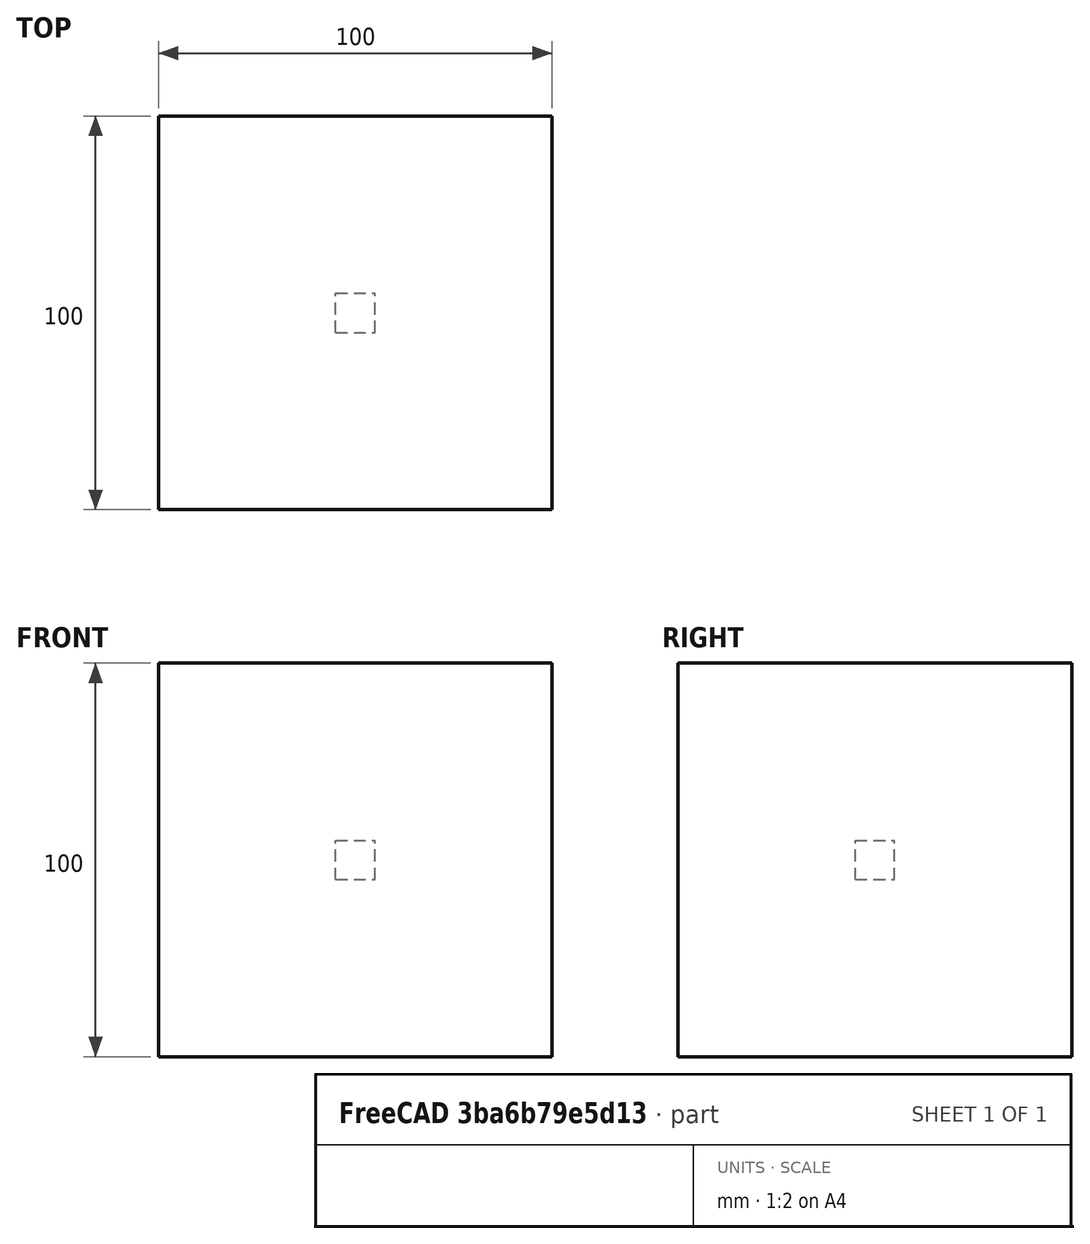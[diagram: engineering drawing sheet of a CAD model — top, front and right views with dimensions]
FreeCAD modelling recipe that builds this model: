
FCSTD DOCUMENT  (FreeCAD 0.20R29603 (Git))
Label: testCase
License: All rights reserved
LicenseURL: http://en.wikipedia.org/wiki/All_rights_reserved
objects: App::DocumentObjectGroupPython×1251, Part::FeaturePython×3, App::Part×2
note: 2 computed .brp shape members not serialized (recipe doc carries the construction recipe); baked Part::Feature solids carry a one-line shape summary decoded from their .brp

FEATURE [App::DocumentObjectGroupPython] HALFPI  # scripted group (container) (typed FeaturePython)
  name = HALFPI
  value = pi/2.
FEATURE [App::DocumentObjectGroupPython] PI  # scripted group (container) (typed FeaturePython)
  name = PI
  value = 1.*pi
FEATURE [App::DocumentObjectGroupPython] TWOPI  # scripted group (container) (typed FeaturePython)
  name = TWOPI
  value = 2.*pi
FEATURE [App::DocumentObjectGroupPython] Constants  # scripted group (container) (typed FeaturePython)
  Group = -> [HALFPI,PI,TWOPI]
FEATURE [App::DocumentObjectGroupPython] Variables  # scripted group (container) (typed FeaturePython)
FEATURE [App::DocumentObjectGroupPython] Quantities  # scripted group (container) (typed FeaturePython)
FEATURE [App::DocumentObjectGroupPython] Isotopes  # scripted group (container) (typed FeaturePython)
FEATURE [App::DocumentObjectGroupPython] Elements  # scripted group (container) (typed FeaturePython)
FEATURE [App::DocumentObjectGroupPython] Matrix  # scripted group (container) (typed FeaturePython)
FEATURE [App::DocumentObjectGroupPython] Surfaces  # scripted group (container) (typed FeaturePython)
FEATURE [App::DocumentObjectGroupPython] Opticals  # scripted group (container) (typed FeaturePython)
  Group = -> [Matrix,Surfaces]
FEATURE [App::DocumentObjectGroupPython] G4Isotopes  # scripted group (container) (typed FeaturePython)
FEATURE [App::DocumentObjectGroupPython] H_element  # scripted group (container) (typed FeaturePython)
  Z = 1
  atom_value = 1.008
  formula = H
  name = H_element
FEATURE [App::DocumentObjectGroupPython] He_element  # scripted group (container) (typed FeaturePython)
  Z = 2
  atom_value = 4.0026
  formula = He
  name = He_element
FEATURE [App::DocumentObjectGroupPython] Li_element  # scripted group (container) (typed FeaturePython)
  Z = 3
  atom_value = 6.94
  formula = Li
  name = Li_element
FEATURE [App::DocumentObjectGroupPython] Be_element  # scripted group (container) (typed FeaturePython)
  Z = 4
  atom_value = 9.01218
  formula = Be
  name = Be_element
FEATURE [App::DocumentObjectGroupPython] B_element  # scripted group (container) (typed FeaturePython)
  Z = 5
  atom_value = 10.81
  formula = B
  name = B_element
FEATURE [App::DocumentObjectGroupPython] C_element  # scripted group (container) (typed FeaturePython)
  Z = 6
  atom_value = 12.011
  formula = C
  name = C_element
FEATURE [App::DocumentObjectGroupPython] N_element  # scripted group (container) (typed FeaturePython)
  Z = 7
  atom_value = 14.007
  formula = N
  name = N_element
FEATURE [App::DocumentObjectGroupPython] O_element  # scripted group (container) (typed FeaturePython)
  Z = 8
  atom_value = 15.999
  formula = O
  name = O_element
FEATURE [App::DocumentObjectGroupPython] F_element  # scripted group (container) (typed FeaturePython)
  Z = 9
  atom_value = 18.9984
  formula = F
  name = F_element
FEATURE [App::DocumentObjectGroupPython] Ne_element  # scripted group (container) (typed FeaturePython)
  Z = 10
  atom_value = 20.1797
  formula = Ne
  name = Ne_element
FEATURE [App::DocumentObjectGroupPython] Na_element  # scripted group (container) (typed FeaturePython)
  Z = 11
  atom_value = 22.9898
  formula = Na
  name = Na_element
FEATURE [App::DocumentObjectGroupPython] Mg_element  # scripted group (container) (typed FeaturePython)
  Z = 12
  atom_value = 24.305
  formula = Mg
  name = Mg_element
FEATURE [App::DocumentObjectGroupPython] Al_element  # scripted group (container) (typed FeaturePython)
  Z = 13
  atom_value = 26.9815
  formula = Al
  name = Al_element
FEATURE [App::DocumentObjectGroupPython] Si_element  # scripted group (container) (typed FeaturePython)
  Z = 14
  atom_value = 28.085
  formula = Si
  name = Si_element
FEATURE [App::DocumentObjectGroupPython] P_element  # scripted group (container) (typed FeaturePython)
  Z = 15
  atom_value = 30.9738
  formula = P
  name = P_element
FEATURE [App::DocumentObjectGroupPython] S_element  # scripted group (container) (typed FeaturePython)
  Z = 16
  atom_value = 32.06
  formula = S
  name = S_element
FEATURE [App::DocumentObjectGroupPython] Cl_element  # scripted group (container) (typed FeaturePython)
  Z = 17
  atom_value = 35.45
  formula = Cl
  name = Cl_element
FEATURE [App::DocumentObjectGroupPython] Ar_element  # scripted group (container) (typed FeaturePython)
  Z = 18
  atom_value = 39.95
  formula = Ar
  name = Ar_element
FEATURE [App::DocumentObjectGroupPython] K_element  # scripted group (container) (typed FeaturePython)
  Z = 19
  atom_value = 39.0983
  formula = K
  name = K_element
FEATURE [App::DocumentObjectGroupPython] Ca_element  # scripted group (container) (typed FeaturePython)
  Z = 20
  atom_value = 40.078
  formula = Ca
  name = Ca_element
FEATURE [App::DocumentObjectGroupPython] Sc_element  # scripted group (container) (typed FeaturePython)
  Z = 21
  atom_value = 44.9559
  formula = Sc
  name = Sc_element
FEATURE [App::DocumentObjectGroupPython] Ti_element  # scripted group (container) (typed FeaturePython)
  Z = 22
  atom_value = 47.867
  formula = Ti
  name = Ti_element
FEATURE [App::DocumentObjectGroupPython] V_element  # scripted group (container) (typed FeaturePython)
  Z = 23
  atom_value = 50.9415
  formula = V
  name = V_element
FEATURE [App::DocumentObjectGroupPython] Cr_element  # scripted group (container) (typed FeaturePython)
  Z = 24
  atom_value = 51.9961
  formula = Cr
  name = Cr_element
FEATURE [App::DocumentObjectGroupPython] Mn_element  # scripted group (container) (typed FeaturePython)
  Z = 25
  atom_value = 54.938
  formula = Mn
  name = Mn_element
FEATURE [App::DocumentObjectGroupPython] Fe_element  # scripted group (container) (typed FeaturePython)
  Z = 26
  atom_value = 55.845
  formula = Fe
  name = Fe_element
FEATURE [App::DocumentObjectGroupPython] Co_element  # scripted group (container) (typed FeaturePython)
  Z = 27
  atom_value = 58.9332
  formula = Co
  name = Co_element
FEATURE [App::DocumentObjectGroupPython] Ni_element  # scripted group (container) (typed FeaturePython)
  Z = 28
  atom_value = 58.6934
  formula = Ni
  name = Ni_element
FEATURE [App::DocumentObjectGroupPython] Cu_element  # scripted group (container) (typed FeaturePython)
  Z = 29
  atom_value = 63.546
  formula = Cu
  name = Cu_element
FEATURE [App::DocumentObjectGroupPython] Zn_element  # scripted group (container) (typed FeaturePython)
  Z = 30
  atom_value = 65.38
  formula = Zn
  name = Zn_element
FEATURE [App::DocumentObjectGroupPython] Ga_element  # scripted group (container) (typed FeaturePython)
  Z = 31
  atom_value = 69.723
  formula = Ga
  name = Ga_element
FEATURE [App::DocumentObjectGroupPython] Ge_element  # scripted group (container) (typed FeaturePython)
  Z = 32
  atom_value = 72.63
  formula = Ge
  name = Ge_element
FEATURE [App::DocumentObjectGroupPython] As_element  # scripted group (container) (typed FeaturePython)
  Z = 33
  atom_value = 74.9216
  formula = As
  name = As_element
FEATURE [App::DocumentObjectGroupPython] Se_element  # scripted group (container) (typed FeaturePython)
  Z = 34
  atom_value = 78.971
  formula = Se
  name = Se_element
FEATURE [App::DocumentObjectGroupPython] Br_element  # scripted group (container) (typed FeaturePython)
  Z = 35
  atom_value = 79.904
  formula = Br
  name = Br_element
FEATURE [App::DocumentObjectGroupPython] Kr_element  # scripted group (container) (typed FeaturePython)
  Z = 36
  atom_value = 83.798
  formula = Kr
  name = Kr_element
FEATURE [App::DocumentObjectGroupPython] Rb_element  # scripted group (container) (typed FeaturePython)
  Z = 37
  atom_value = 85.4678
  formula = Rb
  name = Rb_element
FEATURE [App::DocumentObjectGroupPython] Sr_element  # scripted group (container) (typed FeaturePython)
  Z = 38
  atom_value = 87.62
  formula = Sr
  name = Sr_element
FEATURE [App::DocumentObjectGroupPython] Y_element  # scripted group (container) (typed FeaturePython)
  Z = 39
  atom_value = 88.9058
  formula = Y
  name = Y_element
FEATURE [App::DocumentObjectGroupPython] Zr_element  # scripted group (container) (typed FeaturePython)
  Z = 40
  atom_value = 91.224
  formula = Zr
  name = Zr_element
FEATURE [App::DocumentObjectGroupPython] Nb_element  # scripted group (container) (typed FeaturePython)
  Z = 41
  atom_value = 92.9064
  formula = Nb
  name = Nb_element
FEATURE [App::DocumentObjectGroupPython] Mo_element  # scripted group (container) (typed FeaturePython)
  Z = 42
  atom_value = 95.95
  formula = Mo
  name = Mo_element
FEATURE [App::DocumentObjectGroupPython] Tc_element  # scripted group (container) (typed FeaturePython)
  Z = 43
  atom_value = 97
  formula = Tc
  name = Tc_element
FEATURE [App::DocumentObjectGroupPython] Ru_element  # scripted group (container) (typed FeaturePython)
  Z = 44
  atom_value = 101.07
  formula = Ru
  name = Ru_element
FEATURE [App::DocumentObjectGroupPython] Rh_element  # scripted group (container) (typed FeaturePython)
  Z = 45
  atom_value = 102.905
  formula = Rh
  name = Rh_element
FEATURE [App::DocumentObjectGroupPython] Pd_element  # scripted group (container) (typed FeaturePython)
  Z = 46
  atom_value = 106.42
  formula = Pd
  name = Pd_element
FEATURE [App::DocumentObjectGroupPython] Ag_element  # scripted group (container) (typed FeaturePython)
  Z = 47
  atom_value = 107.868
  formula = Ag
  name = Ag_element
FEATURE [App::DocumentObjectGroupPython] Cd_element  # scripted group (container) (typed FeaturePython)
  Z = 48
  atom_value = 112.414
  formula = Cd
  name = Cd_element
FEATURE [App::DocumentObjectGroupPython] In_element  # scripted group (container) (typed FeaturePython)
  Z = 49
  atom_value = 114.818
  formula = In
  name = In_element
FEATURE [App::DocumentObjectGroupPython] Sn_element  # scripted group (container) (typed FeaturePython)
  Z = 50
  atom_value = 118.71
  formula = Sn
  name = Sn_element
FEATURE [App::DocumentObjectGroupPython] Sb_element  # scripted group (container) (typed FeaturePython)
  Z = 51
  atom_value = 121.76
  formula = Sb
  name = Sb_element
FEATURE [App::DocumentObjectGroupPython] Te_element  # scripted group (container) (typed FeaturePython)
  Z = 52
  atom_value = 127.6
  formula = Te
  name = Te_element
FEATURE [App::DocumentObjectGroupPython] I_element  # scripted group (container) (typed FeaturePython)
  Z = 53
  atom_value = 126.904
  formula = I
  name = I_element
FEATURE [App::DocumentObjectGroupPython] Xe_element  # scripted group (container) (typed FeaturePython)
  Z = 54
  atom_value = 131.293
  formula = Xe
  name = Xe_element
FEATURE [App::DocumentObjectGroupPython] Cs_element  # scripted group (container) (typed FeaturePython)
  Z = 55
  atom_value = 132.905
  formula = Cs
  name = Cs_element
FEATURE [App::DocumentObjectGroupPython] Ba_element  # scripted group (container) (typed FeaturePython)
  Z = 56
  atom_value = 137.327
  formula = Ba
  name = Ba_element
FEATURE [App::DocumentObjectGroupPython] La_element  # scripted group (container) (typed FeaturePython)
  Z = 57
  atom_value = 138.905
  formula = La
  name = La_element
FEATURE [App::DocumentObjectGroupPython] Ce_element  # scripted group (container) (typed FeaturePython)
  Z = 58
  atom_value = 140.116
  formula = Ce
  name = Ce_element
FEATURE [App::DocumentObjectGroupPython] Pr_element  # scripted group (container) (typed FeaturePython)
  Z = 59
  atom_value = 140.908
  formula = Pr
  name = Pr_element
FEATURE [App::DocumentObjectGroupPython] Nd_element  # scripted group (container) (typed FeaturePython)
  Z = 60
  atom_value = 144.242
  formula = Nd
  name = Nd_element
FEATURE [App::DocumentObjectGroupPython] Pm_element  # scripted group (container) (typed FeaturePython)
  Z = 61
  atom_value = 145
  formula = Pm
  name = Pm_element
FEATURE [App::DocumentObjectGroupPython] Sm_element  # scripted group (container) (typed FeaturePython)
  Z = 62
  atom_value = 150.36
  formula = Sm
  name = Sm_element
FEATURE [App::DocumentObjectGroupPython] Eu_element  # scripted group (container) (typed FeaturePython)
  Z = 63
  atom_value = 151.964
  formula = Eu
  name = Eu_element
FEATURE [App::DocumentObjectGroupPython] Gd_element  # scripted group (container) (typed FeaturePython)
  Z = 64
  atom_value = 157.25
  formula = Gd
  name = Gd_element
FEATURE [App::DocumentObjectGroupPython] Tb_element  # scripted group (container) (typed FeaturePython)
  Z = 65
  atom_value = 158.925
  formula = Tb
  name = Tb_element
FEATURE [App::DocumentObjectGroupPython] Dy_element  # scripted group (container) (typed FeaturePython)
  Z = 66
  atom_value = 162.5
  formula = Dy
  name = Dy_element
FEATURE [App::DocumentObjectGroupPython] Ho_element  # scripted group (container) (typed FeaturePython)
  Z = 67
  atom_value = 164.93
  formula = Ho
  name = Ho_element
FEATURE [App::DocumentObjectGroupPython] Er_element  # scripted group (container) (typed FeaturePython)
  Z = 68
  atom_value = 167.259
  formula = Er
  name = Er_element
FEATURE [App::DocumentObjectGroupPython] Tm_element  # scripted group (container) (typed FeaturePython)
  Z = 69
  atom_value = 168.934
  formula = Tm
  name = Tm_element
FEATURE [App::DocumentObjectGroupPython] Yb_element  # scripted group (container) (typed FeaturePython)
  Z = 70
  atom_value = 173.045
  formula = Yb
  name = Yb_element
FEATURE [App::DocumentObjectGroupPython] Lu_element  # scripted group (container) (typed FeaturePython)
  Z = 71
  atom_value = 174.967
  formula = Lu
  name = Lu_element
FEATURE [App::DocumentObjectGroupPython] Hf_element  # scripted group (container) (typed FeaturePython)
  Z = 72
  atom_value = 178.49
  formula = Hf
  name = Hf_element
FEATURE [App::DocumentObjectGroupPython] Ta_element  # scripted group (container) (typed FeaturePython)
  Z = 73
  atom_value = 180.948
  formula = Ta
  name = Ta_element
FEATURE [App::DocumentObjectGroupPython] W_element  # scripted group (container) (typed FeaturePython)
  Z = 74
  atom_value = 183.84
  formula = W
  name = W_element
FEATURE [App::DocumentObjectGroupPython] Re_element  # scripted group (container) (typed FeaturePython)
  Z = 75
  atom_value = 186.207
  formula = Re
  name = Re_element
FEATURE [App::DocumentObjectGroupPython] Os_element  # scripted group (container) (typed FeaturePython)
  Z = 76
  atom_value = 190.23
  formula = Os
  name = Os_element
FEATURE [App::DocumentObjectGroupPython] Ir_element  # scripted group (container) (typed FeaturePython)
  Z = 77
  atom_value = 192.217
  formula = Ir
  name = Ir_element
FEATURE [App::DocumentObjectGroupPython] Pt_element  # scripted group (container) (typed FeaturePython)
  Z = 78
  atom_value = 195.084
  formula = Pt
  name = Pt_element
FEATURE [App::DocumentObjectGroupPython] Au_element  # scripted group (container) (typed FeaturePython)
  Z = 79
  atom_value = 196.967
  formula = Au
  name = Au_element
FEATURE [App::DocumentObjectGroupPython] Hg_element  # scripted group (container) (typed FeaturePython)
  Z = 80
  atom_value = 200.592
  formula = Hg
  name = Hg_element
FEATURE [App::DocumentObjectGroupPython] Tl_element  # scripted group (container) (typed FeaturePython)
  Z = 81
  atom_value = 204.38
  formula = Tl
  name = Tl_element
FEATURE [App::DocumentObjectGroupPython] Pb_element  # scripted group (container) (typed FeaturePython)
  Z = 82
  atom_value = 207.2
  formula = Pb
  name = Pb_element
FEATURE [App::DocumentObjectGroupPython] Bi_element  # scripted group (container) (typed FeaturePython)
  Z = 83
  atom_value = 208.98
  formula = Bi
  name = Bi_element
FEATURE [App::DocumentObjectGroupPython] Po_element  # scripted group (container) (typed FeaturePython)
  Z = 84
  atom_value = 209
  formula = Po
  name = Po_element
FEATURE [App::DocumentObjectGroupPython] At_element  # scripted group (container) (typed FeaturePython)
  Z = 85
  atom_value = 210
  formula = At
  name = At_element
FEATURE [App::DocumentObjectGroupPython] Rn_element  # scripted group (container) (typed FeaturePython)
  Z = 86
  atom_value = 222
  formula = Rn
  name = Rn_element
FEATURE [App::DocumentObjectGroupPython] Fr_element  # scripted group (container) (typed FeaturePython)
  Z = 87
  atom_value = 223
  formula = Fr
  name = Fr_element
FEATURE [App::DocumentObjectGroupPython] Ra_element  # scripted group (container) (typed FeaturePython)
  Z = 88
  atom_value = 226
  formula = Ra
  name = Ra_element
FEATURE [App::DocumentObjectGroupPython] Ac_element  # scripted group (container) (typed FeaturePython)
  Z = 89
  atom_value = 227
  formula = Ac
  name = Ac_element
FEATURE [App::DocumentObjectGroupPython] Th_element  # scripted group (container) (typed FeaturePython)
  Z = 90
  atom_value = 232.038
  formula = Th
  name = Th_element
FEATURE [App::DocumentObjectGroupPython] Pa_element  # scripted group (container) (typed FeaturePython)
  Z = 91
  atom_value = 231.036
  formula = Pa
  name = Pa_element
FEATURE [App::DocumentObjectGroupPython] U_element  # scripted group (container) (typed FeaturePython)
  Z = 92
  atom_value = 238.029
  formula = U
  name = U_element
FEATURE [App::DocumentObjectGroupPython] Np_element  # scripted group (container) (typed FeaturePython)
  Z = 93
  atom_value = 237
  formula = Np
  name = Np_element
FEATURE [App::DocumentObjectGroupPython] Pu_element  # scripted group (container) (typed FeaturePython)
  Z = 94
  atom_value = 244
  formula = Pu
  name = Pu_element
FEATURE [App::DocumentObjectGroupPython] Am_element  # scripted group (container) (typed FeaturePython)
  Z = 95
  atom_value = 243
  formula = Am
  name = Am_element
FEATURE [App::DocumentObjectGroupPython] Cm_element  # scripted group (container) (typed FeaturePython)
  Z = 96
  atom_value = 247
  formula = Cm
  name = Cm_element
FEATURE [App::DocumentObjectGroupPython] Bk_element  # scripted group (container) (typed FeaturePython)
  Z = 97
  atom_value = 247
  formula = Bk
  name = Bk_element
FEATURE [App::DocumentObjectGroupPython] Cf_element  # scripted group (container) (typed FeaturePython)
  Z = 98
  atom_value = 251
  formula = Cf
  name = Cf_element
FEATURE [App::DocumentObjectGroupPython] G4Elements  # scripted group (container) (typed FeaturePython)
  Group = -> [H_element,He_element,Li_element,Be_element,B_element,C_element,N_element,O_element,F_element,Ne_element,Na_element,Mg_element,Al_element,Si_element,P_element,S_element,Cl_element,Ar_element,K_element,Ca_element,Sc_element,Ti_element,V_element,Cr_element,Mn_element,Fe_element,Co_element,Ni_element,Cu_element,Zn_element,Ga_element,Ge_element,As_element,Se_element,Br_element,Kr_element,Rb_element,+61 more]
FEATURE [App::DocumentObjectGroupPython] H_element001  label="H_element : 0.101"  # scripted group (container) (typed FeaturePython)
  n = 0.101327
FEATURE [App::DocumentObjectGroupPython] C_element001  label="C_element : 0.775"  # scripted group (container) (typed FeaturePython)
  n = 0.7755
FEATURE [App::DocumentObjectGroupPython] N_element001  label="N_element : 0.035"  # scripted group (container) (typed FeaturePython)
  n = 0.035057
FEATURE [App::DocumentObjectGroupPython] O_element001  label="O_element : 0.052"  # scripted group (container) (typed FeaturePython)
  n = 0.0523159
FEATURE [App::DocumentObjectGroupPython] F_element001  label="F_element : 0.017"  # scripted group (container) (typed FeaturePython)
  n = 0.017422
FEATURE [App::DocumentObjectGroupPython] Ca_element001  label="Ca_element : 0.018"  # scripted group (container) (typed FeaturePython)
  n = 0.018378
FEATURE [App::DocumentObjectGroupPython] G4_A_150_TISSUE  label="G4_A-150_TISSUE"  # scripted group (container) (typed FeaturePython)
  Dunit = g/cm3
  Dvalue = 1.127
  Group = -> [H_element001,C_element001,N_element001,O_element001,F_element001,Ca_element001]
  conduct = 2
  density = 1
  expand = 3
  formula = G4_A-150_TISSUE
  name = G4_A-150_TISSUE
  specific = 4
FEATURE [App::DocumentObjectGroupPython] C_element002  label="C_element : 3"  # scripted group (container) (typed FeaturePython)
  n = 3
  ref = C_element
FEATURE [App::DocumentObjectGroupPython] H_element002  label="H_element : 6"  # scripted group (container) (typed FeaturePython)
  n = 6
  ref = H_element
FEATURE [App::DocumentObjectGroupPython] O_element002  label="O_element : 1"  # scripted group (container) (typed FeaturePython)
  n = 1
  ref = O_element
FEATURE [App::DocumentObjectGroupPython] G4_ACETONE  # scripted group (container) (typed FeaturePython)
  Dunit = g/cm3
  Dvalue = 0.7899
  Group = -> [C_element002,H_element002,O_element002]
  conduct = 2
  density = 1
  expand = 3
  formula = G4_ACETONE
  name = G4_ACETONE
  specific = 4
FEATURE [App::DocumentObjectGroupPython] C_element003  label="C_element : 2"  # scripted group (container) (typed FeaturePython)
  n = 2
  ref = C_element
FEATURE [App::DocumentObjectGroupPython] H_element003  label="H_element : 2"  # scripted group (container) (typed FeaturePython)
  n = 2
  ref = H_element
FEATURE [App::DocumentObjectGroupPython] G4_ACETYLENE  # scripted group (container) (typed FeaturePython)
  Dunit = g/cm3
  Dvalue = 0.0010967
  Group = -> [C_element003,H_element003]
  conduct = 2
  density = 1
  expand = 3
  formula = G4_ACETYLENE
  name = G4_ACETYLENE
  specific = 4
FEATURE [App::DocumentObjectGroupPython] C_element004  label="C_element : 5"  # scripted group (container) (typed FeaturePython)
  n = 5
  ref = C_element
FEATURE [App::DocumentObjectGroupPython] H_element004  label="H_element : 5"  # scripted group (container) (typed FeaturePython)
  n = 5
  ref = H_element
FEATURE [App::DocumentObjectGroupPython] N_element002  label="N_element : 5"  # scripted group (container) (typed FeaturePython)
  n = 5
  ref = N_element
FEATURE [App::DocumentObjectGroupPython] G4_ADENINE  # scripted group (container) (typed FeaturePython)
  Dunit = g/cm3
  Dvalue = 1.6
  Group = -> [C_element004,H_element004,N_element002]
  conduct = 2
  density = 1
  expand = 3
  formula = G4_ADENINE
  name = G4_ADENINE
  specific = 4
FEATURE [App::DocumentObjectGroupPython] H_element005  label="H_element : 0.114"  # scripted group (container) (typed FeaturePython)
  n = 0.114
FEATURE [App::DocumentObjectGroupPython] C_element005  label="C_element : 0.598"  # scripted group (container) (typed FeaturePython)
  n = 0.598
FEATURE [App::DocumentObjectGroupPython] N_element003  label="N_element : 0.007"  # scripted group (container) (typed FeaturePython)
  n = 0.007
FEATURE [App::DocumentObjectGroupPython] O_element003  label="O_element : 0.278"  # scripted group (container) (typed FeaturePython)
  n = 0.278
FEATURE [App::DocumentObjectGroupPython] Na_element001  label="Na_element : 0.001"  # scripted group (container) (typed FeaturePython)
  n = 0.001
FEATURE [App::DocumentObjectGroupPython] S_element001  label="S_element : 0.001"  # scripted group (container) (typed FeaturePython)
  n = 0.001
FEATURE [App::DocumentObjectGroupPython] Cl_element001  label="Cl_element : 0.001"  # scripted group (container) (typed FeaturePython)
  n = 0.001
FEATURE [App::DocumentObjectGroupPython] G4_ADIPOSE_TISSUE_ICRP  # scripted group (container) (typed FeaturePython)
  Dunit = g/cm3
  Dvalue = 0.95
  Group = -> [H_element005,C_element005,N_element003,O_element003,Na_element001,S_element001,Cl_element001]
  conduct = 2
  density = 1
  expand = 3
  formula = G4_ADIPOSE_TISSUE_ICRP
  name = G4_ADIPOSE_TISSUE_ICRP
  specific = 4
FEATURE [App::DocumentObjectGroupPython] C_element006  label="C_element : 0.000"  # scripted group (container) (typed FeaturePython)
  n = 0.000124
FEATURE [App::DocumentObjectGroupPython] N_element004  label="N_element : 0.755"  # scripted group (container) (typed FeaturePython)
  n = 0.755268
FEATURE [App::DocumentObjectGroupPython] O_element004  label="O_element : 0.232"  # scripted group (container) (typed FeaturePython)
  n = 0.231781
FEATURE [App::DocumentObjectGroupPython] Ar_element001  label="Ar_element : 0.013"  # scripted group (container) (typed FeaturePython)
  n = 0.012827
FEATURE [App::DocumentObjectGroupPython] G4_AIR  # scripted group (container) (typed FeaturePython)
  Dunit = g/cm3
  Dvalue = 0.00120479
  Group = -> [C_element006,N_element004,O_element004,Ar_element001]
  conduct = 2
  density = 1
  expand = 3
  formula = G4_AIR
  name = G4_AIR
  specific = 4
FEATURE [App::DocumentObjectGroupPython] C_element007  label="C_element : 006"  # scripted group (container) (typed FeaturePython)
  n = 3
  ref = C_element
FEATURE [App::DocumentObjectGroupPython] H_element006  label="H_element : 7"  # scripted group (container) (typed FeaturePython)
  n = 7
  ref = H_element
FEATURE [App::DocumentObjectGroupPython] N_element005  label="N_element : 1"  # scripted group (container) (typed FeaturePython)
  n = 1
  ref = N_element
FEATURE [App::DocumentObjectGroupPython] O_element005  label="O_element : 2"  # scripted group (container) (typed FeaturePython)
  n = 2
  ref = O_element
FEATURE [App::DocumentObjectGroupPython] G4_ALANINE  # scripted group (container) (typed FeaturePython)
  Dunit = g/cm3
  Dvalue = 1.42
  Group = -> [C_element007,H_element006,N_element005,O_element005]
  conduct = 2
  density = 1
  expand = 3
  formula = G4_ALANINE
  name = G4_ALANINE
  specific = 4
FEATURE [App::DocumentObjectGroupPython] Al_element001  label="Al_element : 2"  # scripted group (container) (typed FeaturePython)
  n = 2
  ref = Al_element
FEATURE [App::DocumentObjectGroupPython] O_element006  label="O_element : 3"  # scripted group (container) (typed FeaturePython)
  n = 3
  ref = O_element
FEATURE [App::DocumentObjectGroupPython] G4_ALUMINUM_OXIDE  # scripted group (container) (typed FeaturePython)
  Dunit = g/cm3
  Dvalue = 3.97
  Group = -> [Al_element001,O_element006]
  conduct = 2
  density = 1
  expand = 3
  formula = G4_ALUMINUM_OXIDE
  name = G4_ALUMINUM_OXIDE
  specific = 4
FEATURE [App::DocumentObjectGroupPython] H_element007  label="H_element : 0.106"  # scripted group (container) (typed FeaturePython)
  n = 0.10593
FEATURE [App::DocumentObjectGroupPython] C_element008  label="C_element : 0.789"  # scripted group (container) (typed FeaturePython)
  n = 0.788974
FEATURE [App::DocumentObjectGroupPython] O_element007  label="O_element : 0.105"  # scripted group (container) (typed FeaturePython)
  n = 0.105096
FEATURE [App::DocumentObjectGroupPython] G4_AMBER  # scripted group (container) (typed FeaturePython)
  Dunit = g/cm3
  Dvalue = 1.1
  Group = -> [H_element007,C_element008,O_element007]
  conduct = 2
  density = 1
  expand = 3
  formula = G4_AMBER
  name = G4_AMBER
  specific = 4
FEATURE [App::DocumentObjectGroupPython] N_element006  label="N_element : 006"  # scripted group (container) (typed FeaturePython)
  n = 1
  ref = N_element
FEATURE [App::DocumentObjectGroupPython] H_element008  label="H_element : 3"  # scripted group (container) (typed FeaturePython)
  n = 3
  ref = H_element
FEATURE [App::DocumentObjectGroupPython] G4_AMMONIA  # scripted group (container) (typed FeaturePython)
  Dunit = g/cm3
  Dvalue = 0.000826019
  Group = -> [N_element006,H_element008]
  conduct = 2
  density = 1
  expand = 3
  formula = G4_AMMONIA
  name = G4_AMMONIA
  specific = 4
FEATURE [App::DocumentObjectGroupPython] C_element009  label="C_element : 6"  # scripted group (container) (typed FeaturePython)
  n = 6
  ref = C_element
FEATURE [App::DocumentObjectGroupPython] H_element009  label="H_element : 008"  # scripted group (container) (typed FeaturePython)
  n = 7
  ref = H_element
FEATURE [App::DocumentObjectGroupPython] N_element007  label="N_element : 007"  # scripted group (container) (typed FeaturePython)
  n = 1
  ref = N_element
FEATURE [App::DocumentObjectGroupPython] G4_ANILINE  # scripted group (container) (typed FeaturePython)
  Dunit = g/cm3
  Dvalue = 1.0235
  Group = -> [C_element009,H_element009,N_element007]
  conduct = 2
  density = 1
  expand = 3
  formula = G4_ANILINE
  name = G4_ANILINE
  specific = 4
FEATURE [App::DocumentObjectGroupPython] C_element010  label="C_element : 14"  # scripted group (container) (typed FeaturePython)
  n = 14
  ref = C_element
FEATURE [App::DocumentObjectGroupPython] H_element010  label="H_element : 10"  # scripted group (container) (typed FeaturePython)
  n = 10
  ref = H_element
FEATURE [App::DocumentObjectGroupPython] G4_ANTHRACENE  # scripted group (container) (typed FeaturePython)
  Dunit = g/cm3
  Dvalue = 1.283
  Group = -> [C_element010,H_element010]
  conduct = 2
  density = 1
  expand = 3
  formula = G4_ANTHRACENE
  name = G4_ANTHRACENE
  specific = 4
FEATURE [App::DocumentObjectGroupPython] H_element011  label="H_element : 0.065"  # scripted group (container) (typed FeaturePython)
  n = 0.0654709
FEATURE [App::DocumentObjectGroupPython] C_element011  label="C_element : 0.537"  # scripted group (container) (typed FeaturePython)
  n = 0.536944
FEATURE [App::DocumentObjectGroupPython] N_element008  label="N_element : 0.021"  # scripted group (container) (typed FeaturePython)
  n = 0.0215
FEATURE [App::DocumentObjectGroupPython] O_element008  label="O_element : 0.032"  # scripted group (container) (typed FeaturePython)
  n = 0.032085
FEATURE [App::DocumentObjectGroupPython] F_element002  label="F_element : 0.167"  # scripted group (container) (typed FeaturePython)
  n = 0.167411
FEATURE [App::DocumentObjectGroupPython] Ca_element002  label="Ca_element : 0.177"  # scripted group (container) (typed FeaturePython)
  n = 0.176589
FEATURE [App::DocumentObjectGroupPython] G4_B_100_BONE  label="G4_B-100_BONE"  # scripted group (container) (typed FeaturePython)
  Dunit = g/cm3
  Dvalue = 1.45
  Group = -> [H_element011,C_element011,N_element008,O_element008,F_element002,Ca_element002]
  conduct = 2
  density = 1
  expand = 3
  formula = G4_B-100_BONE
  name = G4_B-100_BONE
  specific = 4
FEATURE [App::DocumentObjectGroupPython] H_element012  label="H_element : 0.057"  # scripted group (container) (typed FeaturePython)
  n = 0.057441
FEATURE [App::DocumentObjectGroupPython] C_element012  label="C_element : 0.790"  # scripted group (container) (typed FeaturePython)
  n = 0.774591
FEATURE [App::DocumentObjectGroupPython] O_element009  label="O_element : 0.168"  # scripted group (container) (typed FeaturePython)
  n = 0.167968
FEATURE [App::DocumentObjectGroupPython] G4_BAKELITE  # scripted group (container) (typed FeaturePython)
  Dunit = g/cm3
  Dvalue = 1.25
  Group = -> [H_element012,C_element012,O_element009]
  conduct = 2
  density = 1
  expand = 3
  formula = G4_BAKELITE
  name = G4_BAKELITE
  specific = 4
FEATURE [App::DocumentObjectGroupPython] Ba_element001  label="Ba_element : 1"  # scripted group (container) (typed FeaturePython)
  n = 1
  ref = Ba_element
FEATURE [App::DocumentObjectGroupPython] F_element003  label="F_element : 2"  # scripted group (container) (typed FeaturePython)
  n = 2
  ref = F_element
FEATURE [App::DocumentObjectGroupPython] G4_BARIUM_FLUORIDE  # scripted group (container) (typed FeaturePython)
  Dunit = g/cm3
  Dvalue = 4.89
  Group = -> [Ba_element001,F_element003]
  conduct = 2
  density = 1
  expand = 3
  formula = G4_BARIUM_FLUORIDE
  name = G4_BARIUM_FLUORIDE
  specific = 4
FEATURE [App::DocumentObjectGroupPython] Ba_element002  label="Ba_element : 002"  # scripted group (container) (typed FeaturePython)
  n = 1
  ref = Ba_element
FEATURE [App::DocumentObjectGroupPython] S_element002  label="S_element : 1"  # scripted group (container) (typed FeaturePython)
  n = 1
  ref = S_element
FEATURE [App::DocumentObjectGroupPython] O_element010  label="O_element : 4"  # scripted group (container) (typed FeaturePython)
  n = 4
  ref = O_element
FEATURE [App::DocumentObjectGroupPython] G4_BARIUM_SULFATE  # scripted group (container) (typed FeaturePython)
  Dunit = g/cm3
  Dvalue = 4.5
  Group = -> [Ba_element002,S_element002,O_element010]
  conduct = 2
  density = 1
  expand = 3
  formula = G4_BARIUM_SULFATE
  name = G4_BARIUM_SULFATE
  specific = 4
FEATURE [App::DocumentObjectGroupPython] C_element013  label="C_element : 007"  # scripted group (container) (typed FeaturePython)
  n = 6
  ref = C_element
FEATURE [App::DocumentObjectGroupPython] H_element013  label="H_element : 009"  # scripted group (container) (typed FeaturePython)
  n = 6
  ref = H_element
FEATURE [App::DocumentObjectGroupPython] G4_BENZENE  # scripted group (container) (typed FeaturePython)
  Dunit = g/cm3
  Dvalue = 0.87865
  Group = -> [C_element013,H_element013]
  conduct = 2
  density = 1
  expand = 3
  formula = G4_BENZENE
  name = G4_BENZENE
  specific = 4
FEATURE [App::DocumentObjectGroupPython] Be_element001  label="Be_element : 1"  # scripted group (container) (typed FeaturePython)
  n = 1
  ref = Be_element
FEATURE [App::DocumentObjectGroupPython] O_element011  label="O_element : 005"  # scripted group (container) (typed FeaturePython)
  n = 1
  ref = O_element
FEATURE [App::DocumentObjectGroupPython] G4_BERYLLIUM_OXIDE  # scripted group (container) (typed FeaturePython)
  Dunit = g/cm3
  Dvalue = 3.01
  Group = -> [Be_element001,O_element011]
  conduct = 2
  density = 1
  expand = 3
  formula = G4_BERYLLIUM_OXIDE
  name = G4_BERYLLIUM_OXIDE
  specific = 4
FEATURE [App::DocumentObjectGroupPython] Bi_element001  label="Bi_element : 4"  # scripted group (container) (typed FeaturePython)
  n = 4
  ref = Bi_element
FEATURE [App::DocumentObjectGroupPython] Ge_element001  label="Ge_element : 3"  # scripted group (container) (typed FeaturePython)
  n = 3
  ref = Ge_element
FEATURE [App::DocumentObjectGroupPython] O_element012  label="O_element : 12"  # scripted group (container) (typed FeaturePython)
  n = 12
  ref = O_element
FEATURE [App::DocumentObjectGroupPython] G4_BGO  # scripted group (container) (typed FeaturePython)
  Dunit = g/cm3
  Dvalue = 7.13
  Group = -> [Bi_element001,Ge_element001,O_element012]
  conduct = 2
  density = 1
  expand = 3
  formula = G4_BGO
  name = G4_BGO
  specific = 4
FEATURE [App::DocumentObjectGroupPython] H_element014  label="H_element : 0.102"  # scripted group (container) (typed FeaturePython)
  n = 0.102
FEATURE [App::DocumentObjectGroupPython] C_element014  label="C_element : 0.110"  # scripted group (container) (typed FeaturePython)
  n = 0.11
FEATURE [App::DocumentObjectGroupPython] N_element009  label="N_element : 0.033"  # scripted group (container) (typed FeaturePython)
  n = 0.033
FEATURE [App::DocumentObjectGroupPython] O_element013  label="O_element : 0.745"  # scripted group (container) (typed FeaturePython)
  n = 0.745
FEATURE [App::DocumentObjectGroupPython] Na_element002  label="Na_element : 0.002"  # scripted group (container) (typed FeaturePython)
  n = 0.001
FEATURE [App::DocumentObjectGroupPython] P_element001  label="P_element : 0.001"  # scripted group (container) (typed FeaturePython)
  n = 0.001
FEATURE [App::DocumentObjectGroupPython] S_element003  label="S_element : 0.002"  # scripted group (container) (typed FeaturePython)
  n = 0.002
FEATURE [App::DocumentObjectGroupPython] Cl_element002  label="Cl_element : 0.003"  # scripted group (container) (typed FeaturePython)
  n = 0.003
FEATURE [App::DocumentObjectGroupPython] K_element001  label="K_element : 0.002"  # scripted group (container) (typed FeaturePython)
  n = 0.002
FEATURE [App::DocumentObjectGroupPython] Fe_element001  label="Fe_element : 0.001"  # scripted group (container) (typed FeaturePython)
  n = 0.001
FEATURE [App::DocumentObjectGroupPython] G4_BLOOD_ICRP  # scripted group (container) (typed FeaturePython)
  Dunit = g/cm3
  Dvalue = 1.06
  Group = -> [H_element014,C_element014,N_element009,O_element013,Na_element002,P_element001,S_element003,Cl_element002,K_element001,Fe_element001]
  conduct = 2
  density = 1
  expand = 3
  formula = G4_BLOOD_ICRP
  name = G4_BLOOD_ICRP
  specific = 4
FEATURE [App::DocumentObjectGroupPython] H_element015  label="H_element : 0.064"  # scripted group (container) (typed FeaturePython)
  n = 0.064
FEATURE [App::DocumentObjectGroupPython] C_element015  label="C_element : 0.278"  # scripted group (container) (typed FeaturePython)
  n = 0.278
FEATURE [App::DocumentObjectGroupPython] N_element010  label="N_element : 0.027"  # scripted group (container) (typed FeaturePython)
  n = 0.027
FEATURE [App::DocumentObjectGroupPython] O_element014  label="O_element : 0.410"  # scripted group (container) (typed FeaturePython)
  n = 0.41
FEATURE [App::DocumentObjectGroupPython] Mg_element001  label="Mg_element : 0.002"  # scripted group (container) (typed FeaturePython)
  n = 0.002
FEATURE [App::DocumentObjectGroupPython] P_element002  label="P_element : 0.070"  # scripted group (container) (typed FeaturePython)
  n = 0.07
FEATURE [App::DocumentObjectGroupPython] S_element004  label="S_element : 0.003"  # scripted group (container) (typed FeaturePython)
  n = 0.002
FEATURE [App::DocumentObjectGroupPython] Ca_element003  label="Ca_element : 0.147"  # scripted group (container) (typed FeaturePython)
  n = 0.147
FEATURE [App::DocumentObjectGroupPython] G4_BONE_COMPACT_ICRU  # scripted group (container) (typed FeaturePython)
  Dunit = g/cm3
  Dvalue = 1.85
  Group = -> [H_element015,C_element015,N_element010,O_element014,Mg_element001,P_element002,S_element004,Ca_element003]
  conduct = 2
  density = 1
  expand = 3
  formula = G4_BONE_COMPACT_ICRU
  name = G4_BONE_COMPACT_ICRU
  specific = 4
FEATURE [App::DocumentObjectGroupPython] H_element016  label="H_element : 0.034"  # scripted group (container) (typed FeaturePython)
  n = 0.034
FEATURE [App::DocumentObjectGroupPython] C_element016  label="C_element : 0.155"  # scripted group (container) (typed FeaturePython)
  n = 0.155
FEATURE [App::DocumentObjectGroupPython] N_element011  label="N_element : 0.042"  # scripted group (container) (typed FeaturePython)
  n = 0.042
FEATURE [App::DocumentObjectGroupPython] O_element015  label="O_element : 0.435"  # scripted group (container) (typed FeaturePython)
  n = 0.435
FEATURE [App::DocumentObjectGroupPython] Na_element003  label="Na_element : 0.003"  # scripted group (container) (typed FeaturePython)
  n = 0.001
FEATURE [App::DocumentObjectGroupPython] Mg_element002  label="Mg_element : 0.003"  # scripted group (container) (typed FeaturePython)
  n = 0.002
FEATURE [App::DocumentObjectGroupPython] P_element003  label="P_element : 0.103"  # scripted group (container) (typed FeaturePython)
  n = 0.103
FEATURE [App::DocumentObjectGroupPython] S_element005  label="S_element : 0.004"  # scripted group (container) (typed FeaturePython)
  n = 0.003
FEATURE [App::DocumentObjectGroupPython] Ca_element004  label="Ca_element : 0.225"  # scripted group (container) (typed FeaturePython)
  n = 0.225
FEATURE [App::DocumentObjectGroupPython] G4_BONE_CORTICAL_ICRP  # scripted group (container) (typed FeaturePython)
  Dunit = g/cm3
  Dvalue = 1.92
  Group = -> [H_element016,C_element016,N_element011,O_element015,Na_element003,Mg_element002,P_element003,S_element005,Ca_element004]
  conduct = 2
  density = 1
  expand = 3
  formula = G4_BONE_CORTICAL_ICRP
  name = G4_BONE_CORTICAL_ICRP
  specific = 4
FEATURE [App::DocumentObjectGroupPython] B_element001  label="B_element : 4"  # scripted group (container) (typed FeaturePython)
  n = 4
  ref = B_element
FEATURE [App::DocumentObjectGroupPython] C_element017  label="C_element : 1"  # scripted group (container) (typed FeaturePython)
  n = 1
  ref = C_element
FEATURE [App::DocumentObjectGroupPython] G4_BORON_CARBIDE  # scripted group (container) (typed FeaturePython)
  Dunit = g/cm3
  Dvalue = 2.52
  Group = -> [B_element001,C_element017]
  conduct = 2
  density = 1
  expand = 3
  formula = G4_BORON_CARBIDE
  name = G4_BORON_CARBIDE
  specific = 4
FEATURE [App::DocumentObjectGroupPython] B_element002  label="B_element : 2"  # scripted group (container) (typed FeaturePython)
  n = 2
  ref = B_element
FEATURE [App::DocumentObjectGroupPython] O_element016  label="O_element : 006"  # scripted group (container) (typed FeaturePython)
  n = 3
  ref = O_element
FEATURE [App::DocumentObjectGroupPython] G4_BORON_OXIDE  # scripted group (container) (typed FeaturePython)
  Dunit = g/cm3
  Dvalue = 1.812
  Group = -> [B_element002,O_element016]
  conduct = 2
  density = 1
  expand = 3
  formula = G4_BORON_OXIDE
  name = G4_BORON_OXIDE
  specific = 4
FEATURE [App::DocumentObjectGroupPython] H_element017  label="H_element : 0.107"  # scripted group (container) (typed FeaturePython)
  n = 0.107
FEATURE [App::DocumentObjectGroupPython] C_element018  label="C_element : 0.145"  # scripted group (container) (typed FeaturePython)
  n = 0.145
FEATURE [App::DocumentObjectGroupPython] N_element012  label="N_element : 0.022"  # scripted group (container) (typed FeaturePython)
  n = 0.022
FEATURE [App::DocumentObjectGroupPython] O_element017  label="O_element : 0.712"  # scripted group (container) (typed FeaturePython)
  n = 0.712
FEATURE [App::DocumentObjectGroupPython] Na_element004  label="Na_element : 0.004"  # scripted group (container) (typed FeaturePython)
  n = 0.002
FEATURE [App::DocumentObjectGroupPython] P_element004  label="P_element : 0.004"  # scripted group (container) (typed FeaturePython)
  n = 0.004
FEATURE [App::DocumentObjectGroupPython] S_element006  label="S_element : 0.005"  # scripted group (container) (typed FeaturePython)
  n = 0.002
FEATURE [App::DocumentObjectGroupPython] Cl_element003  label="Cl_element : 0.004"  # scripted group (container) (typed FeaturePython)
  n = 0.003
FEATURE [App::DocumentObjectGroupPython] K_element002  label="K_element : 0.003"  # scripted group (container) (typed FeaturePython)
  n = 0.003
FEATURE [App::DocumentObjectGroupPython] G4_BRAIN_ICRP  # scripted group (container) (typed FeaturePython)
  Dunit = g/cm3
  Dvalue = 1.04
  Group = -> [H_element017,C_element018,N_element012,O_element017,Na_element004,P_element004,S_element006,Cl_element003,K_element002]
  conduct = 2
  density = 1
  expand = 3
  formula = G4_BRAIN_ICRP
  name = G4_BRAIN_ICRP
  specific = 4
FEATURE [App::DocumentObjectGroupPython] C_element019  label="C_element : 4"  # scripted group (container) (typed FeaturePython)
  n = 4
  ref = C_element
FEATURE [App::DocumentObjectGroupPython] H_element018  label="H_element : 010"  # scripted group (container) (typed FeaturePython)
  n = 10
  ref = H_element
FEATURE [App::DocumentObjectGroupPython] G4_BUTANE  # scripted group (container) (typed FeaturePython)
  Dunit = g/cm3
  Dvalue = 0.00249343
  Group = -> [C_element019,H_element018]
  conduct = 2
  density = 1
  expand = 3
  formula = G4_BUTANE
  name = G4_BUTANE
  specific = 4
FEATURE [App::DocumentObjectGroupPython] C_element020  label="C_element : 008"  # scripted group (container) (typed FeaturePython)
  n = 4
  ref = C_element
FEATURE [App::DocumentObjectGroupPython] H_element019  label="H_element : 011"  # scripted group (container) (typed FeaturePython)
  n = 10
  ref = H_element
FEATURE [App::DocumentObjectGroupPython] O_element018  label="O_element : 007"  # scripted group (container) (typed FeaturePython)
  n = 1
  ref = O_element
FEATURE [App::DocumentObjectGroupPython] G4_N_BUTYL_ALCOHOL  label="G4_N-BUTYL_ALCOHOL"  # scripted group (container) (typed FeaturePython)
  Dunit = g/cm3
  Dvalue = 0.8098
  Group = -> [C_element020,H_element019,O_element018]
  conduct = 2
  density = 1
  expand = 3
  formula = G4_N-BUTYL_ALCOHOL
  name = G4_N-BUTYL_ALCOHOL
  specific = 4
FEATURE [App::DocumentObjectGroupPython] H_element020  label="H_element : 0.025"  # scripted group (container) (typed FeaturePython)
  n = 0.02468
FEATURE [App::DocumentObjectGroupPython] C_element021  label="C_element : 0.502"  # scripted group (container) (typed FeaturePython)
  n = 0.501611
FEATURE [App::DocumentObjectGroupPython] O_element019  label="O_element : 0.005"  # scripted group (container) (typed FeaturePython)
  n = 0.004527
FEATURE [App::DocumentObjectGroupPython] F_element004  label="F_element : 0.465"  # scripted group (container) (typed FeaturePython)
  n = 0.465209
FEATURE [App::DocumentObjectGroupPython] Si_element001  label="Si_element : 0.004"  # scripted group (container) (typed FeaturePython)
  n = 0.003973
FEATURE [App::DocumentObjectGroupPython] G4_C_552  label="G4_C-552"  # scripted group (container) (typed FeaturePython)
  Dunit = g/cm3
  Dvalue = 1.76
  Group = -> [H_element020,C_element021,O_element019,F_element004,Si_element001]
  conduct = 2
  density = 1
  expand = 3
  formula = G4_C-552
  name = G4_C-552
  specific = 4
FEATURE [App::DocumentObjectGroupPython] Cd_element001  label="Cd_element : 1"  # scripted group (container) (typed FeaturePython)
  n = 1
  ref = Cd_element
FEATURE [App::DocumentObjectGroupPython] Te_element001  label="Te_element : 1"  # scripted group (container) (typed FeaturePython)
  n = 1
  ref = Te_element
FEATURE [App::DocumentObjectGroupPython] G4_CADMIUM_TELLURIDE  # scripted group (container) (typed FeaturePython)
  Dunit = g/cm3
  Dvalue = 6.2
  Group = -> [Cd_element001,Te_element001]
  conduct = 2
  density = 1
  expand = 3
  formula = G4_CADMIUM_TELLURIDE
  name = G4_CADMIUM_TELLURIDE
  specific = 4
FEATURE [App::DocumentObjectGroupPython] Cd_element002  label="Cd_element : 002"  # scripted group (container) (typed FeaturePython)
  n = 1
  ref = Cd_element
FEATURE [App::DocumentObjectGroupPython] W_element001  label="W_element : 1"  # scripted group (container) (typed FeaturePython)
  n = 1
  ref = W_element
FEATURE [App::DocumentObjectGroupPython] O_element020  label="O_element : 008"  # scripted group (container) (typed FeaturePython)
  n = 4
  ref = O_element
FEATURE [App::DocumentObjectGroupPython] G4_CADMIUM_TUNGSTATE  # scripted group (container) (typed FeaturePython)
  Dunit = g/cm3
  Dvalue = 7.9
  Group = -> [Cd_element002,W_element001,O_element020]
  conduct = 2
  density = 1
  expand = 3
  formula = G4_CADMIUM_TUNGSTATE
  name = G4_CADMIUM_TUNGSTATE
  specific = 4
FEATURE [App::DocumentObjectGroupPython] Ca_element005  label="Ca_element : 1"  # scripted group (container) (typed FeaturePython)
  n = 1
  ref = Ca_element
FEATURE [App::DocumentObjectGroupPython] C_element022  label="C_element : 009"  # scripted group (container) (typed FeaturePython)
  n = 1
  ref = C_element
FEATURE [App::DocumentObjectGroupPython] O_element021  label="O_element : 009"  # scripted group (container) (typed FeaturePython)
  n = 3
  ref = O_element
FEATURE [App::DocumentObjectGroupPython] G4_CALCIUM_CARBONATE  # scripted group (container) (typed FeaturePython)
  Dunit = g/cm3
  Dvalue = 2.8
  Group = -> [Ca_element005,C_element022,O_element021]
  conduct = 2
  density = 1
  expand = 3
  formula = G4_CALCIUM_CARBONATE
  name = G4_CALCIUM_CARBONATE
  specific = 4
FEATURE [App::DocumentObjectGroupPython] Ca_element006  label="Ca_element : 002"  # scripted group (container) (typed FeaturePython)
  n = 1
  ref = Ca_element
FEATURE [App::DocumentObjectGroupPython] F_element005  label="F_element : 003"  # scripted group (container) (typed FeaturePython)
  n = 2
  ref = F_element
FEATURE [App::DocumentObjectGroupPython] G4_CALCIUM_FLUORIDE  # scripted group (container) (typed FeaturePython)
  Dunit = g/cm3
  Dvalue = 3.18
  Group = -> [Ca_element006,F_element005]
  conduct = 2
  density = 1
  expand = 3
  formula = G4_CALCIUM_FLUORIDE
  name = G4_CALCIUM_FLUORIDE
  specific = 4
FEATURE [App::DocumentObjectGroupPython] Ca_element007  label="Ca_element : 003"  # scripted group (container) (typed FeaturePython)
  n = 1
  ref = Ca_element
FEATURE [App::DocumentObjectGroupPython] O_element022  label="O_element : 010"  # scripted group (container) (typed FeaturePython)
  n = 1
  ref = O_element
FEATURE [App::DocumentObjectGroupPython] G4_CALCIUM_OXIDE  # scripted group (container) (typed FeaturePython)
  Dunit = g/cm3
  Dvalue = 3.3
  Group = -> [Ca_element007,O_element022]
  conduct = 2
  density = 1
  expand = 3
  formula = G4_CALCIUM_OXIDE
  name = G4_CALCIUM_OXIDE
  specific = 4
FEATURE [App::DocumentObjectGroupPython] Ca_element008  label="Ca_element : 004"  # scripted group (container) (typed FeaturePython)
  n = 1
  ref = Ca_element
FEATURE [App::DocumentObjectGroupPython] S_element007  label="S_element : 002"  # scripted group (container) (typed FeaturePython)
  n = 1
  ref = S_element
FEATURE [App::DocumentObjectGroupPython] O_element023  label="O_element : 011"  # scripted group (container) (typed FeaturePython)
  n = 4
  ref = O_element
FEATURE [App::DocumentObjectGroupPython] G4_CALCIUM_SULFATE  # scripted group (container) (typed FeaturePython)
  Dunit = g/cm3
  Dvalue = 2.96
  Group = -> [Ca_element008,S_element007,O_element023]
  conduct = 2
  density = 1
  expand = 3
  formula = G4_CALCIUM_SULFATE
  name = G4_CALCIUM_SULFATE
  specific = 4
FEATURE [App::DocumentObjectGroupPython] Ca_element009  label="Ca_element : 005"  # scripted group (container) (typed FeaturePython)
  n = 1
  ref = Ca_element
FEATURE [App::DocumentObjectGroupPython] W_element002  label="W_element : 002"  # scripted group (container) (typed FeaturePython)
  n = 1
  ref = W_element
FEATURE [App::DocumentObjectGroupPython] O_element024  label="O_element : 012"  # scripted group (container) (typed FeaturePython)
  n = 4
  ref = O_element
FEATURE [App::DocumentObjectGroupPython] G4_CALCIUM_TUNGSTATE  # scripted group (container) (typed FeaturePython)
  Dunit = g/cm3
  Dvalue = 6.062
  Group = -> [Ca_element009,W_element002,O_element024]
  conduct = 2
  density = 1
  expand = 3
  formula = G4_CALCIUM_TUNGSTATE
  name = G4_CALCIUM_TUNGSTATE
  specific = 4
FEATURE [App::DocumentObjectGroupPython] C_element023  label="C_element : 010"  # scripted group (container) (typed FeaturePython)
  n = 1
  ref = C_element
FEATURE [App::DocumentObjectGroupPython] O_element025  label="O_element : 013"  # scripted group (container) (typed FeaturePython)
  n = 2
  ref = O_element
FEATURE [App::DocumentObjectGroupPython] G4_CARBON_DIOXIDE  # scripted group (container) (typed FeaturePython)
  Dunit = g/cm3
  Dvalue = 0.00184212
  Group = -> [C_element023,O_element025]
  conduct = 2
  density = 1
  expand = 3
  formula = G4_CARBON_DIOXIDE
  name = G4_CARBON_DIOXIDE
  specific = 4
FEATURE [App::DocumentObjectGroupPython] C_element024  label="C_element : 011"  # scripted group (container) (typed FeaturePython)
  n = 1
  ref = C_element
FEATURE [App::DocumentObjectGroupPython] Cl_element004  label="Cl_element : 4"  # scripted group (container) (typed FeaturePython)
  n = 4
  ref = Cl_element
FEATURE [App::DocumentObjectGroupPython] G4_CARBON_TETRACHLORIDE  # scripted group (container) (typed FeaturePython)
  Dunit = g/cm3
  Dvalue = 1.594
  Group = -> [C_element024,Cl_element004]
  conduct = 2
  density = 1
  expand = 3
  formula = G4_CARBON_TETRACHLORIDE
  name = G4_CARBON_TETRACHLORIDE
  specific = 4
FEATURE [App::DocumentObjectGroupPython] C_element025  label="C_element : 012"  # scripted group (container) (typed FeaturePython)
  n = 6
  ref = C_element
FEATURE [App::DocumentObjectGroupPython] H_element021  label="H_element : 012"  # scripted group (container) (typed FeaturePython)
  n = 10
  ref = H_element
FEATURE [App::DocumentObjectGroupPython] O_element026  label="O_element : 5"  # scripted group (container) (typed FeaturePython)
  n = 5
  ref = O_element
FEATURE [App::DocumentObjectGroupPython] G4_CELLULOSE_CELLOPHANE  # scripted group (container) (typed FeaturePython)
  Dunit = g/cm3
  Dvalue = 1.42
  Group = -> [C_element025,H_element021,O_element026]
  conduct = 2
  density = 1
  expand = 3
  formula = G4_CELLULOSE_CELLOPHANE
  name = G4_CELLULOSE_CELLOPHANE
  specific = 4
FEATURE [App::DocumentObjectGroupPython] H_element022  label="H_element : 0.067"  # scripted group (container) (typed FeaturePython)
  n = 0.067125
FEATURE [App::DocumentObjectGroupPython] C_element026  label="C_element : 0.545"  # scripted group (container) (typed FeaturePython)
  n = 0.545403
FEATURE [App::DocumentObjectGroupPython] O_element027  label="O_element : 0.387"  # scripted group (container) (typed FeaturePython)
  n = 0.387472
FEATURE [App::DocumentObjectGroupPython] G4_CELLULOSE_BUTYRATE  # scripted group (container) (typed FeaturePython)
  Dunit = g/cm3
  Dvalue = 1.2
  Group = -> [H_element022,C_element026,O_element027]
  conduct = 2
  density = 1
  expand = 3
  formula = G4_CELLULOSE_BUTYRATE
  name = G4_CELLULOSE_BUTYRATE
  specific = 4
FEATURE [App::DocumentObjectGroupPython] H_element023  label="H_element : 0.029"  # scripted group (container) (typed FeaturePython)
  n = 0.029216
FEATURE [App::DocumentObjectGroupPython] C_element027  label="C_element : 0.271"  # scripted group (container) (typed FeaturePython)
  n = 0.271296
FEATURE [App::DocumentObjectGroupPython] N_element013  label="N_element : 0.121"  # scripted group (container) (typed FeaturePython)
  n = 0.121276
FEATURE [App::DocumentObjectGroupPython] O_element028  label="O_element : 0.578"  # scripted group (container) (typed FeaturePython)
  n = 0.578212
FEATURE [App::DocumentObjectGroupPython] G4_CELLULOSE_NITRATE  # scripted group (container) (typed FeaturePython)
  Dunit = g/cm3
  Dvalue = 1.49
  Group = -> [H_element023,C_element027,N_element013,O_element028]
  conduct = 2
  density = 1
  expand = 3
  formula = G4_CELLULOSE_NITRATE
  name = G4_CELLULOSE_NITRATE
  specific = 4
FEATURE [App::DocumentObjectGroupPython] H_element024  label="H_element : 0.108"  # scripted group (container) (typed FeaturePython)
  n = 0.107596
FEATURE [App::DocumentObjectGroupPython] N_element014  label="N_element : 0.001"  # scripted group (container) (typed FeaturePython)
  n = 0.0008
FEATURE [App::DocumentObjectGroupPython] O_element029  label="O_element : 0.875"  # scripted group (container) (typed FeaturePython)
  n = 0.874976
FEATURE [App::DocumentObjectGroupPython] S_element008  label="S_element : 0.015"  # scripted group (container) (typed FeaturePython)
  n = 0.014627
FEATURE [App::DocumentObjectGroupPython] Ce_element001  label="Ce_element : 0.002"  # scripted group (container) (typed FeaturePython)
  n = 0.002001
FEATURE [App::DocumentObjectGroupPython] G4_CERIC_SULFATE  # scripted group (container) (typed FeaturePython)
  Dunit = g/cm3
  Dvalue = 1.03
  Group = -> [H_element024,N_element014,O_element029,S_element008,Ce_element001]
  conduct = 2
  density = 1
  expand = 3
  formula = G4_CERIC_SULFATE
  name = G4_CERIC_SULFATE
  specific = 4
FEATURE [App::DocumentObjectGroupPython] Cs_element001  label="Cs_element : 1"  # scripted group (container) (typed FeaturePython)
  n = 1
  ref = Cs_element
FEATURE [App::DocumentObjectGroupPython] F_element006  label="F_element : 1"  # scripted group (container) (typed FeaturePython)
  n = 1
  ref = F_element
FEATURE [App::DocumentObjectGroupPython] G4_CESIUM_FLUORIDE  # scripted group (container) (typed FeaturePython)
  Dunit = g/cm3
  Dvalue = 4.115
  Group = -> [Cs_element001,F_element006]
  conduct = 2
  density = 1
  expand = 3
  formula = G4_CESIUM_FLUORIDE
  name = G4_CESIUM_FLUORIDE
  specific = 4
FEATURE [App::DocumentObjectGroupPython] Cs_element002  label="Cs_element : 002"  # scripted group (container) (typed FeaturePython)
  n = 1
  ref = Cs_element
FEATURE [App::DocumentObjectGroupPython] I_element001  label="I_element : 1"  # scripted group (container) (typed FeaturePython)
  n = 1
  ref = I_element
FEATURE [App::DocumentObjectGroupPython] G4_CESIUM_IODIDE  # scripted group (container) (typed FeaturePython)
  Dunit = g/cm3
  Dvalue = 4.51
  Group = -> [Cs_element002,I_element001]
  conduct = 2
  density = 1
  expand = 3
  formula = G4_CESIUM_IODIDE
  name = G4_CESIUM_IODIDE
  specific = 4
FEATURE [App::DocumentObjectGroupPython] C_element028  label="C_element : 013"  # scripted group (container) (typed FeaturePython)
  n = 6
  ref = C_element
FEATURE [App::DocumentObjectGroupPython] H_element025  label="H_element : 013"  # scripted group (container) (typed FeaturePython)
  n = 5
  ref = H_element
FEATURE [App::DocumentObjectGroupPython] Cl_element005  label="Cl_element : 1"  # scripted group (container) (typed FeaturePython)
  n = 1
  ref = Cl_element
FEATURE [App::DocumentObjectGroupPython] G4_CHLOROBENZENE  # scripted group (container) (typed FeaturePython)
  Dunit = g/cm3
  Dvalue = 1.1058
  Group = -> [C_element028,H_element025,Cl_element005]
  conduct = 2
  density = 1
  expand = 3
  formula = G4_CHLOROBENZENE
  name = G4_CHLOROBENZENE
  specific = 4
FEATURE [App::DocumentObjectGroupPython] C_element029  label="C_element : 014"  # scripted group (container) (typed FeaturePython)
  n = 1
  ref = C_element
FEATURE [App::DocumentObjectGroupPython] H_element026  label="H_element : 1"  # scripted group (container) (typed FeaturePython)
  n = 1
  ref = H_element
FEATURE [App::DocumentObjectGroupPython] Cl_element006  label="Cl_element : 3"  # scripted group (container) (typed FeaturePython)
  n = 3
  ref = Cl_element
FEATURE [App::DocumentObjectGroupPython] G4_CHLOROFORM  # scripted group (container) (typed FeaturePython)
  Dunit = g/cm3
  Dvalue = 1.4832
  Group = -> [C_element029,H_element026,Cl_element006]
  conduct = 2
  density = 1
  expand = 3
  formula = G4_CHLOROFORM
  name = G4_CHLOROFORM
  specific = 4
FEATURE [App::DocumentObjectGroupPython] H_element027  label="H_element : 0.010"  # scripted group (container) (typed FeaturePython)
  n = 0.01
FEATURE [App::DocumentObjectGroupPython] C_element030  label="C_element : 0.001"  # scripted group (container) (typed FeaturePython)
  n = 0.001
FEATURE [App::DocumentObjectGroupPython] O_element030  label="O_element : 0.529"  # scripted group (container) (typed FeaturePython)
  n = 0.529107
FEATURE [App::DocumentObjectGroupPython] Na_element005  label="Na_element : 0.016"  # scripted group (container) (typed FeaturePython)
  n = 0.016
FEATURE [App::DocumentObjectGroupPython] Mg_element003  label="Mg_element : 0.004"  # scripted group (container) (typed FeaturePython)
  n = 0.002
FEATURE [App::DocumentObjectGroupPython] Al_element002  label="Al_element : 0.034"  # scripted group (container) (typed FeaturePython)
  n = 0.033872
FEATURE [App::DocumentObjectGroupPython] Si_element002  label="Si_element : 0.337"  # scripted group (container) (typed FeaturePython)
  n = 0.337021
FEATURE [App::DocumentObjectGroupPython] K_element003  label="K_element : 0.013"  # scripted group (container) (typed FeaturePython)
  n = 0.013
FEATURE [App::DocumentObjectGroupPython] Ca_element010  label="Ca_element : 0.044"  # scripted group (container) (typed FeaturePython)
  n = 0.044
FEATURE [App::DocumentObjectGroupPython] Fe_element002  label="Fe_element : 0.014"  # scripted group (container) (typed FeaturePython)
  n = 0.014
FEATURE [App::DocumentObjectGroupPython] G4_CONCRETE  # scripted group (container) (typed FeaturePython)
  Dunit = g/cm3
  Dvalue = 2.3
  Group = -> [H_element027,C_element030,O_element030,Na_element005,Mg_element003,Al_element002,Si_element002,K_element003,Ca_element010,Fe_element002]
  conduct = 2
  density = 1
  expand = 3
  formula = G4_CONCRETE
  name = G4_CONCRETE
  specific = 4
FEATURE [App::DocumentObjectGroupPython] C_element031  label="C_element : 015"  # scripted group (container) (typed FeaturePython)
  n = 6
  ref = C_element
FEATURE [App::DocumentObjectGroupPython] H_element028  label="H_element : 12"  # scripted group (container) (typed FeaturePython)
  n = 12
  ref = H_element
FEATURE [App::DocumentObjectGroupPython] G4_CYCLOHEXANE  # scripted group (container) (typed FeaturePython)
  Dunit = g/cm3
  Dvalue = 0.779
  Group = -> [C_element031,H_element028]
  conduct = 2
  density = 1
  expand = 3
  formula = G4_CYCLOHEXANE
  name = G4_CYCLOHEXANE
  specific = 4
FEATURE [App::DocumentObjectGroupPython] C_element032  label="C_element : 016"  # scripted group (container) (typed FeaturePython)
  n = 6
  ref = C_element
FEATURE [App::DocumentObjectGroupPython] H_element029  label="H_element : 4"  # scripted group (container) (typed FeaturePython)
  n = 4
  ref = H_element
FEATURE [App::DocumentObjectGroupPython] Cl_element007  label="Cl_element : 2"  # scripted group (container) (typed FeaturePython)
  n = 2
  ref = Cl_element
FEATURE [App::DocumentObjectGroupPython] G4_1_2_DICHLOROBENZENE  label="G4_1.2-DICHLOROBENZENE"  # scripted group (container) (typed FeaturePython)
  Dunit = g/cm3
  Dvalue = 1.3048
  Group = -> [C_element032,H_element029,Cl_element007]
  conduct = 2
  density = 1
  expand = 3
  formula = G4_1.2-DICHLOROBENZENE
  name = G4_1.2-DICHLOROBENZENE
  specific = 4
FEATURE [App::DocumentObjectGroupPython] C_element033  label="C_element : 017"  # scripted group (container) (typed FeaturePython)
  n = 4
  ref = C_element
FEATURE [App::DocumentObjectGroupPython] H_element030  label="H_element : 8"  # scripted group (container) (typed FeaturePython)
  n = 8
  ref = H_element
FEATURE [App::DocumentObjectGroupPython] O_element031  label="O_element : 014"  # scripted group (container) (typed FeaturePython)
  n = 1
  ref = O_element
FEATURE [App::DocumentObjectGroupPython] Cl_element008  label="Cl_element : 005"  # scripted group (container) (typed FeaturePython)
  n = 2
  ref = Cl_element
FEATURE [App::DocumentObjectGroupPython] G4_DICHLORODIETHYL_ETHER  # scripted group (container) (typed FeaturePython)
  Dunit = g/cm3
  Dvalue = 1.2199
  Group = -> [C_element033,H_element030,O_element031,Cl_element008]
  conduct = 2
  density = 1
  expand = 3
  formula = G4_DICHLORODIETHYL_ETHER
  name = G4_DICHLORODIETHYL_ETHER
  specific = 4
FEATURE [App::DocumentObjectGroupPython] C_element034  label="C_element : 018"  # scripted group (container) (typed FeaturePython)
  n = 2
  ref = C_element
FEATURE [App::DocumentObjectGroupPython] H_element031  label="H_element : 014"  # scripted group (container) (typed FeaturePython)
  n = 4
  ref = H_element
FEATURE [App::DocumentObjectGroupPython] Cl_element009  label="Cl_element : 006"  # scripted group (container) (typed FeaturePython)
  n = 2
  ref = Cl_element
FEATURE [App::DocumentObjectGroupPython] G4_1_2_DICHLOROETHANE  label="G4_1.2-DICHLOROETHANE"  # scripted group (container) (typed FeaturePython)
  Dunit = g/cm3
  Dvalue = 1.2351
  Group = -> [C_element034,H_element031,Cl_element009]
  conduct = 2
  density = 1
  expand = 3
  formula = G4_1.2-DICHLOROETHANE
  name = G4_1.2-DICHLOROETHANE
  specific = 4
FEATURE [App::DocumentObjectGroupPython] C_element035  label="C_element : 019"  # scripted group (container) (typed FeaturePython)
  n = 4
  ref = C_element
FEATURE [App::DocumentObjectGroupPython] H_element032  label="H_element : 015"  # scripted group (container) (typed FeaturePython)
  n = 10
  ref = H_element
FEATURE [App::DocumentObjectGroupPython] O_element032  label="O_element : 015"  # scripted group (container) (typed FeaturePython)
  n = 1
  ref = O_element
FEATURE [App::DocumentObjectGroupPython] G4_DIETHYL_ETHER  # scripted group (container) (typed FeaturePython)
  Dunit = g/cm3
  Dvalue = 0.71378
  Group = -> [C_element035,H_element032,O_element032]
  conduct = 2
  density = 1
  expand = 3
  formula = G4_DIETHYL_ETHER
  name = G4_DIETHYL_ETHER
  specific = 4
FEATURE [App::DocumentObjectGroupPython] C_element036  label="C_element : 020"  # scripted group (container) (typed FeaturePython)
  n = 3
  ref = C_element
FEATURE [App::DocumentObjectGroupPython] H_element033  label="H_element : 016"  # scripted group (container) (typed FeaturePython)
  n = 7
  ref = H_element
FEATURE [App::DocumentObjectGroupPython] N_element015  label="N_element : 008"  # scripted group (container) (typed FeaturePython)
  n = 1
  ref = N_element
FEATURE [App::DocumentObjectGroupPython] O_element033  label="O_element : 016"  # scripted group (container) (typed FeaturePython)
  n = 1
  ref = O_element
FEATURE [App::DocumentObjectGroupPython] G4_N_N_DIMETHYL_FORMAMIDE  label="G4_N.N-DIMETHYL_FORMAMIDE"  # scripted group (container) (typed FeaturePython)
  Dunit = g/cm3
  Dvalue = 0.9487
  Group = -> [C_element036,H_element033,N_element015,O_element033]
  conduct = 2
  density = 1
  expand = 3
  formula = G4_N.N-DIMETHYL_FORMAMIDE
  name = G4_N.N-DIMETHYL_FORMAMIDE
  specific = 4
FEATURE [App::DocumentObjectGroupPython] C_element037  label="C_element : 021"  # scripted group (container) (typed FeaturePython)
  n = 2
  ref = C_element
FEATURE [App::DocumentObjectGroupPython] H_element034  label="H_element : 017"  # scripted group (container) (typed FeaturePython)
  n = 6
  ref = H_element
FEATURE [App::DocumentObjectGroupPython] O_element034  label="O_element : 017"  # scripted group (container) (typed FeaturePython)
  n = 1
  ref = O_element
FEATURE [App::DocumentObjectGroupPython] S_element009  label="S_element : 003"  # scripted group (container) (typed FeaturePython)
  n = 1
  ref = S_element
FEATURE [App::DocumentObjectGroupPython] G4_DIMETHYL_SULFOXIDE  # scripted group (container) (typed FeaturePython)
  Dunit = g/cm3
  Dvalue = 1.1014
  Group = -> [C_element037,H_element034,O_element034,S_element009]
  conduct = 2
  density = 1
  expand = 3
  formula = G4_DIMETHYL_SULFOXIDE
  name = G4_DIMETHYL_SULFOXIDE
  specific = 4
FEATURE [App::DocumentObjectGroupPython] C_element038  label="C_element : 022"  # scripted group (container) (typed FeaturePython)
  n = 2
  ref = C_element
FEATURE [App::DocumentObjectGroupPython] H_element035  label="H_element : 018"  # scripted group (container) (typed FeaturePython)
  n = 6
  ref = H_element
FEATURE [App::DocumentObjectGroupPython] G4_ETHANE  # scripted group (container) (typed FeaturePython)
  Dunit = g/cm3
  Dvalue = 0.00125324
  Group = -> [C_element038,H_element035]
  conduct = 2
  density = 1
  expand = 3
  formula = G4_ETHANE
  name = G4_ETHANE
  specific = 4
FEATURE [App::DocumentObjectGroupPython] C_element039  label="C_element : 023"  # scripted group (container) (typed FeaturePython)
  n = 2
  ref = C_element
FEATURE [App::DocumentObjectGroupPython] H_element036  label="H_element : 019"  # scripted group (container) (typed FeaturePython)
  n = 6
  ref = H_element
FEATURE [App::DocumentObjectGroupPython] O_element035  label="O_element : 018"  # scripted group (container) (typed FeaturePython)
  n = 1
  ref = O_element
FEATURE [App::DocumentObjectGroupPython] G4_ETHYL_ALCOHOL  # scripted group (container) (typed FeaturePython)
  Dunit = g/cm3
  Dvalue = 0.7893
  Group = -> [C_element039,H_element036,O_element035]
  conduct = 2
  density = 1
  expand = 3
  formula = G4_ETHYL_ALCOHOL
  name = G4_ETHYL_ALCOHOL
  specific = 4
FEATURE [App::DocumentObjectGroupPython] H_element037  label="H_element : 0.090"  # scripted group (container) (typed FeaturePython)
  n = 0.090027
FEATURE [App::DocumentObjectGroupPython] C_element040  label="C_element : 0.585"  # scripted group (container) (typed FeaturePython)
  n = 0.585182
FEATURE [App::DocumentObjectGroupPython] O_element036  label="O_element : 0.325"  # scripted group (container) (typed FeaturePython)
  n = 0.324791
FEATURE [App::DocumentObjectGroupPython] G4_ETHYL_CELLULOSE  # scripted group (container) (typed FeaturePython)
  Dunit = g/cm3
  Dvalue = 1.13
  Group = -> [H_element037,C_element040,O_element036]
  conduct = 2
  density = 1
  expand = 3
  formula = G4_ETHYL_CELLULOSE
  name = G4_ETHYL_CELLULOSE
  specific = 4
FEATURE [App::DocumentObjectGroupPython] C_element041  label="C_element : 024"  # scripted group (container) (typed FeaturePython)
  n = 2
  ref = C_element
FEATURE [App::DocumentObjectGroupPython] H_element038  label="H_element : 020"  # scripted group (container) (typed FeaturePython)
  n = 4
  ref = H_element
FEATURE [App::DocumentObjectGroupPython] G4_ETHYLENE  # scripted group (container) (typed FeaturePython)
  Dunit = g/cm3
  Dvalue = 0.00117497
  Group = -> [C_element041,H_element038]
  conduct = 2
  density = 1
  expand = 3
  formula = G4_ETHYLENE
  name = G4_ETHYLENE
  specific = 4
FEATURE [App::DocumentObjectGroupPython] H_element039  label="H_element : 0.096"  # scripted group (container) (typed FeaturePython)
  n = 0.096
FEATURE [App::DocumentObjectGroupPython] C_element042  label="C_element : 0.195"  # scripted group (container) (typed FeaturePython)
  n = 0.195
FEATURE [App::DocumentObjectGroupPython] N_element016  label="N_element : 0.057"  # scripted group (container) (typed FeaturePython)
  n = 0.057
FEATURE [App::DocumentObjectGroupPython] O_element037  label="O_element : 0.646"  # scripted group (container) (typed FeaturePython)
  n = 0.646
FEATURE [App::DocumentObjectGroupPython] Na_element006  label="Na_element : 0.017"  # scripted group (container) (typed FeaturePython)
  n = 0.001
FEATURE [App::DocumentObjectGroupPython] P_element005  label="P_element : 0.104"  # scripted group (container) (typed FeaturePython)
  n = 0.001
FEATURE [App::DocumentObjectGroupPython] S_element010  label="S_element : 0.016"  # scripted group (container) (typed FeaturePython)
  n = 0.003
FEATURE [App::DocumentObjectGroupPython] Cl_element010  label="Cl_element : 0.005"  # scripted group (container) (typed FeaturePython)
  n = 0.001
FEATURE [App::DocumentObjectGroupPython] G4_EYE_LENS_ICRP  # scripted group (container) (typed FeaturePython)
  Dunit = g/cm3
  Dvalue = 1.07
  Group = -> [H_element039,C_element042,N_element016,O_element037,Na_element006,P_element005,S_element010,Cl_element010]
  conduct = 2
  density = 1
  expand = 3
  formula = G4_EYE_LENS_ICRP
  name = G4_EYE_LENS_ICRP
  specific = 4
FEATURE [App::DocumentObjectGroupPython] Fe_element003  label="Fe_element : 2"  # scripted group (container) (typed FeaturePython)
  n = 2
  ref = Fe_element
FEATURE [App::DocumentObjectGroupPython] O_element038  label="O_element : 019"  # scripted group (container) (typed FeaturePython)
  n = 3
  ref = O_element
FEATURE [App::DocumentObjectGroupPython] G4_FERRIC_OXIDE  # scripted group (container) (typed FeaturePython)
  Dunit = g/cm3
  Dvalue = 5.2
  Group = -> [Fe_element003,O_element038]
  conduct = 2
  density = 1
  expand = 3
  formula = G4_FERRIC_OXIDE
  name = G4_FERRIC_OXIDE
  specific = 4
FEATURE [App::DocumentObjectGroupPython] Fe_element004  label="Fe_element : 1"  # scripted group (container) (typed FeaturePython)
  n = 1
  ref = Fe_element
FEATURE [App::DocumentObjectGroupPython] B_element003  label="B_element : 1"  # scripted group (container) (typed FeaturePython)
  n = 1
  ref = B_element
FEATURE [App::DocumentObjectGroupPython] G4_FERROBORIDE  # scripted group (container) (typed FeaturePython)
  Dunit = g/cm3
  Dvalue = 7.15
  Group = -> [Fe_element004,B_element003]
  conduct = 2
  density = 1
  expand = 3
  formula = G4_FERROBORIDE
  name = G4_FERROBORIDE
  specific = 4
FEATURE [App::DocumentObjectGroupPython] Fe_element005  label="Fe_element : 003"  # scripted group (container) (typed FeaturePython)
  n = 1
  ref = Fe_element
FEATURE [App::DocumentObjectGroupPython] O_element039  label="O_element : 020"  # scripted group (container) (typed FeaturePython)
  n = 1
  ref = O_element
FEATURE [App::DocumentObjectGroupPython] G4_FERROUS_OXIDE  # scripted group (container) (typed FeaturePython)
  Dunit = g/cm3
  Dvalue = 5.7
  Group = -> [Fe_element005,O_element039]
  conduct = 2
  density = 1
  expand = 3
  formula = G4_FERROUS_OXIDE
  name = G4_FERROUS_OXIDE
  specific = 4
FEATURE [App::DocumentObjectGroupPython] H_element040  label="H_element : 0.115"  # scripted group (container) (typed FeaturePython)
  n = 0.108259
FEATURE [App::DocumentObjectGroupPython] N_element017  label="N_element : 0.000"  # scripted group (container) (typed FeaturePython)
  n = 2.7e-05
FEATURE [App::DocumentObjectGroupPython] O_element040  label="O_element : 0.879"  # scripted group (container) (typed FeaturePython)
  n = 0.878636
FEATURE [App::DocumentObjectGroupPython] Na_element007  label="Na_element : 0.000"  # scripted group (container) (typed FeaturePython)
  n = 2.2e-05
FEATURE [App::DocumentObjectGroupPython] S_element011  label="S_element : 0.013"  # scripted group (container) (typed FeaturePython)
  n = 0.012968
FEATURE [App::DocumentObjectGroupPython] Cl_element011  label="Cl_element : 0.000"  # scripted group (container) (typed FeaturePython)
  n = 3.4e-05
FEATURE [App::DocumentObjectGroupPython] Fe_element006  label="Fe_element : 0.000"  # scripted group (container) (typed FeaturePython)
  n = 5.4e-05
FEATURE [App::DocumentObjectGroupPython] G4_FERROUS_SULFATE  # scripted group (container) (typed FeaturePython)
  Dunit = g/cm3
  Dvalue = 1.024
  Group = -> [H_element040,N_element017,O_element040,Na_element007,S_element011,Cl_element011,Fe_element006]
  conduct = 2
  density = 1
  expand = 3
  formula = G4_FERROUS_SULFATE
  name = G4_FERROUS_SULFATE
  specific = 4
FEATURE [App::DocumentObjectGroupPython] C_element043  label="C_element : 0.099"  # scripted group (container) (typed FeaturePython)
  n = 0.099335
FEATURE [App::DocumentObjectGroupPython] F_element007  label="F_element : 0.314"  # scripted group (container) (typed FeaturePython)
  n = 0.314247
FEATURE [App::DocumentObjectGroupPython] Cl_element012  label="Cl_element : 0.586"  # scripted group (container) (typed FeaturePython)
  n = 0.586418
FEATURE [App::DocumentObjectGroupPython] G4_FREON_12  label="G4_FREON-12"  # scripted group (container) (typed FeaturePython)
  Dunit = g/cm3
  Dvalue = 1.12
  Group = -> [C_element043,F_element007,Cl_element012]
  conduct = 2
  density = 1
  expand = 3
  formula = G4_FREON-12
  name = G4_FREON-12
  specific = 4
FEATURE [App::DocumentObjectGroupPython] C_element044  label="C_element : 0.057"  # scripted group (container) (typed FeaturePython)
  n = 0.057245
FEATURE [App::DocumentObjectGroupPython] F_element008  label="F_element : 0.181"  # scripted group (container) (typed FeaturePython)
  n = 0.181096
FEATURE [App::DocumentObjectGroupPython] Br_element001  label="Br_element : 0.762"  # scripted group (container) (typed FeaturePython)
  n = 0.761659
FEATURE [App::DocumentObjectGroupPython] G4_FREON_12B2  label="G4_FREON-12B2"  # scripted group (container) (typed FeaturePython)
  Dunit = g/cm3
  Dvalue = 1.8
  Group = -> [C_element044,F_element008,Br_element001]
  conduct = 2
  density = 1
  expand = 3
  formula = G4_FREON-12B2
  name = G4_FREON-12B2
  specific = 4
FEATURE [App::DocumentObjectGroupPython] C_element045  label="C_element : 0.115"  # scripted group (container) (typed FeaturePython)
  n = 0.114983
FEATURE [App::DocumentObjectGroupPython] F_element009  label="F_element : 0.546"  # scripted group (container) (typed FeaturePython)
  n = 0.545621
FEATURE [App::DocumentObjectGroupPython] Cl_element013  label="Cl_element : 0.339"  # scripted group (container) (typed FeaturePython)
  n = 0.339396
FEATURE [App::DocumentObjectGroupPython] G4_FREON_13  label="G4_FREON-13"  # scripted group (container) (typed FeaturePython)
  Dunit = g/cm3
  Dvalue = 0.95
  Group = -> [C_element045,F_element009,Cl_element013]
  conduct = 2
  density = 1
  expand = 3
  formula = G4_FREON-13
  name = G4_FREON-13
  specific = 4
FEATURE [App::DocumentObjectGroupPython] C_element046  label="C_element : 025"  # scripted group (container) (typed FeaturePython)
  n = 1
  ref = C_element
FEATURE [App::DocumentObjectGroupPython] F_element010  label="F_element : 3"  # scripted group (container) (typed FeaturePython)
  n = 3
  ref = F_element
FEATURE [App::DocumentObjectGroupPython] Br_element002  label="Br_element : 1"  # scripted group (container) (typed FeaturePython)
  n = 1
  ref = Br_element
FEATURE [App::DocumentObjectGroupPython] G4_FREON_13B1  label="G4_FREON-13B1"  # scripted group (container) (typed FeaturePython)
  Dunit = g/cm3
  Dvalue = 1.5
  Group = -> [C_element046,F_element010,Br_element002]
  conduct = 2
  density = 1
  expand = 3
  formula = G4_FREON-13B1
  name = G4_FREON-13B1
  specific = 4
FEATURE [App::DocumentObjectGroupPython] C_element047  label="C_element : 0.061"  # scripted group (container) (typed FeaturePython)
  n = 0.061309
FEATURE [App::DocumentObjectGroupPython] F_element011  label="F_element : 0.291"  # scripted group (container) (typed FeaturePython)
  n = 0.290924
FEATURE [App::DocumentObjectGroupPython] I_element002  label="I_element : 0.648"  # scripted group (container) (typed FeaturePython)
  n = 0.647767
FEATURE [App::DocumentObjectGroupPython] G4_FREON_13I1  label="G4_FREON-13I1"  # scripted group (container) (typed FeaturePython)
  Dunit = g/cm3
  Dvalue = 1.8
  Group = -> [C_element047,F_element011,I_element002]
  conduct = 2
  density = 1
  expand = 3
  formula = G4_FREON-13I1
  name = G4_FREON-13I1
  specific = 4
FEATURE [App::DocumentObjectGroupPython] Gd_element001  label="Gd_element : 2"  # scripted group (container) (typed FeaturePython)
  n = 2
  ref = Gd_element
FEATURE [App::DocumentObjectGroupPython] O_element041  label="O_element : 021"  # scripted group (container) (typed FeaturePython)
  n = 2
  ref = O_element
FEATURE [App::DocumentObjectGroupPython] S_element012  label="S_element : 004"  # scripted group (container) (typed FeaturePython)
  n = 1
  ref = S_element
FEATURE [App::DocumentObjectGroupPython] G4_GADOLINIUM_OXYSULFIDE  # scripted group (container) (typed FeaturePython)
  Dunit = g/cm3
  Dvalue = 7.44
  Group = -> [Gd_element001,O_element041,S_element012]
  conduct = 2
  density = 1
  expand = 3
  formula = G4_GADOLINIUM_OXYSULFIDE
  name = G4_GADOLINIUM_OXYSULFIDE
  specific = 4
FEATURE [App::DocumentObjectGroupPython] Ga_element001  label="Ga_element : 1"  # scripted group (container) (typed FeaturePython)
  n = 1
  ref = Ga_element
FEATURE [App::DocumentObjectGroupPython] As_element001  label="As_element : 1"  # scripted group (container) (typed FeaturePython)
  n = 1
  ref = As_element
FEATURE [App::DocumentObjectGroupPython] G4_GALLIUM_ARSENIDE  # scripted group (container) (typed FeaturePython)
  Dunit = g/cm3
  Dvalue = 5.31
  Group = -> [Ga_element001,As_element001]
  conduct = 2
  density = 1
  expand = 3
  formula = G4_GALLIUM_ARSENIDE
  name = G4_GALLIUM_ARSENIDE
  specific = 4
FEATURE [App::DocumentObjectGroupPython] H_element041  label="H_element : 0.081"  # scripted group (container) (typed FeaturePython)
  n = 0.08118
FEATURE [App::DocumentObjectGroupPython] C_element048  label="C_element : 0.416"  # scripted group (container) (typed FeaturePython)
  n = 0.41606
FEATURE [App::DocumentObjectGroupPython] N_element018  label="N_element : 0.111"  # scripted group (container) (typed FeaturePython)
  n = 0.11124
FEATURE [App::DocumentObjectGroupPython] O_element042  label="O_element : 0.381"  # scripted group (container) (typed FeaturePython)
  n = 0.38064
FEATURE [App::DocumentObjectGroupPython] S_element013  label="S_element : 0.011"  # scripted group (container) (typed FeaturePython)
  n = 0.01088
FEATURE [App::DocumentObjectGroupPython] G4_GEL_PHOTO_EMULSION  # scripted group (container) (typed FeaturePython)
  Dunit = g/cm3
  Dvalue = 1.2914
  Group = -> [H_element041,C_element048,N_element018,O_element042,S_element013]
  conduct = 2
  density = 1
  expand = 3
  formula = G4_GEL_PHOTO_EMULSION
  name = G4_GEL_PHOTO_EMULSION
  specific = 4
FEATURE [App::DocumentObjectGroupPython] B_element004  label="B_element : 0.040"  # scripted group (container) (typed FeaturePython)
  n = 0.0400639
FEATURE [App::DocumentObjectGroupPython] O_element043  label="O_element : 0.540"  # scripted group (container) (typed FeaturePython)
  n = 0.539561
FEATURE [App::DocumentObjectGroupPython] Na_element008  label="Na_element : 0.028"  # scripted group (container) (typed FeaturePython)
  n = 0.0281909
FEATURE [App::DocumentObjectGroupPython] Al_element003  label="Al_element : 0.012"  # scripted group (container) (typed FeaturePython)
  n = 0.011644
FEATURE [App::DocumentObjectGroupPython] Si_element003  label="Si_element : 0.377"  # scripted group (container) (typed FeaturePython)
  n = 0.377219
FEATURE [App::DocumentObjectGroupPython] K_element004  label="K_element : 0.014"  # scripted group (container) (typed FeaturePython)
  n = 0.00332099
FEATURE [App::DocumentObjectGroupPython] G4_Pyrex_Glass  # scripted group (container) (typed FeaturePython)
  Dunit = g/cm3
  Dvalue = 2.23
  Group = -> [B_element004,O_element043,Na_element008,Al_element003,Si_element003,K_element004]
  conduct = 2
  density = 1
  expand = 3
  formula = G4_Pyrex_Glass
  name = G4_Pyrex_Glass
  specific = 4
FEATURE [App::DocumentObjectGroupPython] O_element044  label="O_element : 0.156"  # scripted group (container) (typed FeaturePython)
  n = 0.156453
FEATURE [App::DocumentObjectGroupPython] Si_element004  label="Si_element : 0.081"  # scripted group (container) (typed FeaturePython)
  n = 0.080866
FEATURE [App::DocumentObjectGroupPython] Ti_element001  label="Ti_element : 0.008"  # scripted group (container) (typed FeaturePython)
  n = 0.008092
FEATURE [App::DocumentObjectGroupPython] As_element002  label="As_element : 0.003"  # scripted group (container) (typed FeaturePython)
  n = 0.002651
FEATURE [App::DocumentObjectGroupPython] Pb_element001  label="Pb_element : 0.752"  # scripted group (container) (typed FeaturePython)
  n = 0.751938
FEATURE [App::DocumentObjectGroupPython] G4_GLASS_LEAD  # scripted group (container) (typed FeaturePython)
  Dunit = g/cm3
  Dvalue = 6.22
  Group = -> [O_element044,Si_element004,Ti_element001,As_element002,Pb_element001]
  conduct = 2
  density = 1
  expand = 3
  formula = G4_GLASS_LEAD
  name = G4_GLASS_LEAD
  specific = 4
FEATURE [App::DocumentObjectGroupPython] O_element045  label="O_element : 0.460"  # scripted group (container) (typed FeaturePython)
  n = 0.4598
FEATURE [App::DocumentObjectGroupPython] Na_element009  label="Na_element : 0.096"  # scripted group (container) (typed FeaturePython)
  n = 0.0964411
FEATURE [App::DocumentObjectGroupPython] Si_element005  label="Si_element : 0.378"  # scripted group (container) (typed FeaturePython)
  n = 0.336553
FEATURE [App::DocumentObjectGroupPython] Ca_element011  label="Ca_element : 0.107"  # scripted group (container) (typed FeaturePython)
  n = 0.107205
FEATURE [App::DocumentObjectGroupPython] G4_GLASS_PLATE  # scripted group (container) (typed FeaturePython)
  Dunit = g/cm3
  Dvalue = 2.4
  Group = -> [O_element045,Na_element009,Si_element005,Ca_element011]
  conduct = 2
  density = 1
  expand = 3
  formula = G4_GLASS_PLATE
  name = G4_GLASS_PLATE
  specific = 4
FEATURE [App::DocumentObjectGroupPython] C_element049  label="C_element : 026"  # scripted group (container) (typed FeaturePython)
  n = 5
  ref = C_element
FEATURE [App::DocumentObjectGroupPython] H_element042  label="H_element : 021"  # scripted group (container) (typed FeaturePython)
  n = 10
  ref = H_element
FEATURE [App::DocumentObjectGroupPython] N_element019  label="N_element : 2"  # scripted group (container) (typed FeaturePython)
  n = 2
  ref = N_element
FEATURE [App::DocumentObjectGroupPython] O_element046  label="O_element : 022"  # scripted group (container) (typed FeaturePython)
  n = 3
  ref = O_element
FEATURE [App::DocumentObjectGroupPython] G4_GLUTAMINE  # scripted group (container) (typed FeaturePython)
  Dunit = g/cm3
  Dvalue = 1.46
  Group = -> [C_element049,H_element042,N_element019,O_element046]
  conduct = 2
  density = 1
  expand = 3
  formula = G4_GLUTAMINE
  name = G4_GLUTAMINE
  specific = 4
FEATURE [App::DocumentObjectGroupPython] C_element050  label="C_element : 027"  # scripted group (container) (typed FeaturePython)
  n = 3
  ref = C_element
FEATURE [App::DocumentObjectGroupPython] H_element043  label="H_element : 022"  # scripted group (container) (typed FeaturePython)
  n = 8
  ref = H_element
FEATURE [App::DocumentObjectGroupPython] O_element047  label="O_element : 023"  # scripted group (container) (typed FeaturePython)
  n = 3
  ref = O_element
FEATURE [App::DocumentObjectGroupPython] G4_GLYCEROL  # scripted group (container) (typed FeaturePython)
  Dunit = g/cm3
  Dvalue = 1.2613
  Group = -> [C_element050,H_element043,O_element047]
  conduct = 2
  density = 1
  expand = 3
  formula = G4_GLYCEROL
  name = G4_GLYCEROL
  specific = 4
FEATURE [App::DocumentObjectGroupPython] C_element051  label="C_element : 028"  # scripted group (container) (typed FeaturePython)
  n = 5
  ref = C_element
FEATURE [App::DocumentObjectGroupPython] H_element044  label="H_element : 023"  # scripted group (container) (typed FeaturePython)
  n = 5
  ref = H_element
FEATURE [App::DocumentObjectGroupPython] N_element020  label="N_element : 009"  # scripted group (container) (typed FeaturePython)
  n = 5
  ref = N_element
FEATURE [App::DocumentObjectGroupPython] O_element048  label="O_element : 024"  # scripted group (container) (typed FeaturePython)
  n = 1
  ref = O_element
FEATURE [App::DocumentObjectGroupPython] G4_GUANINE  # scripted group (container) (typed FeaturePython)
  Dunit = g/cm3
  Dvalue = 2.2
  Group = -> [C_element051,H_element044,N_element020,O_element048]
  conduct = 2
  density = 1
  expand = 3
  formula = G4_GUANINE
  name = G4_GUANINE
  specific = 4
FEATURE [App::DocumentObjectGroupPython] Ca_element012  label="Ca_element : 006"  # scripted group (container) (typed FeaturePython)
  n = 1
  ref = Ca_element
FEATURE [App::DocumentObjectGroupPython] S_element014  label="S_element : 005"  # scripted group (container) (typed FeaturePython)
  n = 1
  ref = S_element
FEATURE [App::DocumentObjectGroupPython] O_element049  label="O_element : 6"  # scripted group (container) (typed FeaturePython)
  n = 6
  ref = O_element
FEATURE [App::DocumentObjectGroupPython] H_element045  label="H_element : 024"  # scripted group (container) (typed FeaturePython)
  n = 4
  ref = H_element
FEATURE [App::DocumentObjectGroupPython] G4_GYPSUM  # scripted group (container) (typed FeaturePython)
  Dunit = g/cm3
  Dvalue = 2.32
  Group = -> [Ca_element012,S_element014,O_element049,H_element045]
  conduct = 2
  density = 1
  expand = 3
  formula = G4_GYPSUM
  name = G4_GYPSUM
  specific = 4
FEATURE [App::DocumentObjectGroupPython] C_element052  label="C_element : 7"  # scripted group (container) (typed FeaturePython)
  n = 7
  ref = C_element
FEATURE [App::DocumentObjectGroupPython] H_element046  label="H_element : 16"  # scripted group (container) (typed FeaturePython)
  n = 16
  ref = H_element
FEATURE [App::DocumentObjectGroupPython] G4_N_HEPTANE  label="G4_N-HEPTANE"  # scripted group (container) (typed FeaturePython)
  Dunit = g/cm3
  Dvalue = 0.68376
  Group = -> [C_element052,H_element046]
  conduct = 2
  density = 1
  expand = 3
  formula = G4_N-HEPTANE
  name = G4_N-HEPTANE
  specific = 4
FEATURE [App::DocumentObjectGroupPython] C_element053  label="C_element : 029"  # scripted group (container) (typed FeaturePython)
  n = 6
  ref = C_element
FEATURE [App::DocumentObjectGroupPython] H_element047  label="H_element : 14"  # scripted group (container) (typed FeaturePython)
  n = 14
  ref = H_element
FEATURE [App::DocumentObjectGroupPython] G4_N_HEXANE  label="G4_N-HEXANE"  # scripted group (container) (typed FeaturePython)
  Dunit = g/cm3
  Dvalue = 0.6603
  Group = -> [C_element053,H_element047]
  conduct = 2
  density = 1
  expand = 3
  formula = G4_N-HEXANE
  name = G4_N-HEXANE
  specific = 4
FEATURE [App::DocumentObjectGroupPython] C_element054  label="C_element : 22"  # scripted group (container) (typed FeaturePython)
  n = 22
  ref = C_element
FEATURE [App::DocumentObjectGroupPython] H_element048  label="H_element : 025"  # scripted group (container) (typed FeaturePython)
  n = 10
  ref = H_element
FEATURE [App::DocumentObjectGroupPython] N_element021  label="N_element : 010"  # scripted group (container) (typed FeaturePython)
  n = 2
  ref = N_element
FEATURE [App::DocumentObjectGroupPython] O_element050  label="O_element : 025"  # scripted group (container) (typed FeaturePython)
  n = 5
  ref = O_element
FEATURE [App::DocumentObjectGroupPython] G4_KAPTON  # scripted group (container) (typed FeaturePython)
  Dunit = g/cm3
  Dvalue = 1.42
  Group = -> [C_element054,H_element048,N_element021,O_element050]
  conduct = 2
  density = 1
  expand = 3
  formula = G4_KAPTON
  name = G4_KAPTON
  specific = 4
FEATURE [App::DocumentObjectGroupPython] La_element001  label="La_element : 1"  # scripted group (container) (typed FeaturePython)
  n = 1
  ref = La_element
FEATURE [App::DocumentObjectGroupPython] Br_element003  label="Br_element : 002"  # scripted group (container) (typed FeaturePython)
  n = 1
  ref = Br_element
FEATURE [App::DocumentObjectGroupPython] O_element051  label="O_element : 026"  # scripted group (container) (typed FeaturePython)
  n = 1
  ref = O_element
FEATURE [App::DocumentObjectGroupPython] G4_LANTHANUM_OXYBROMIDE  # scripted group (container) (typed FeaturePython)
  Dunit = g/cm3
  Dvalue = 6.28
  Group = -> [La_element001,Br_element003,O_element051]
  conduct = 2
  density = 1
  expand = 3
  formula = G4_LANTHANUM_OXYBROMIDE
  name = G4_LANTHANUM_OXYBROMIDE
  specific = 4
FEATURE [App::DocumentObjectGroupPython] La_element002  label="La_element : 2"  # scripted group (container) (typed FeaturePython)
  n = 2
  ref = La_element
FEATURE [App::DocumentObjectGroupPython] O_element052  label="O_element : 027"  # scripted group (container) (typed FeaturePython)
  n = 2
  ref = O_element
FEATURE [App::DocumentObjectGroupPython] S_element015  label="S_element : 006"  # scripted group (container) (typed FeaturePython)
  n = 1
  ref = S_element
FEATURE [App::DocumentObjectGroupPython] G4_LANTHANUM_OXYSULFIDE  # scripted group (container) (typed FeaturePython)
  Dunit = g/cm3
  Dvalue = 5.86
  Group = -> [La_element002,O_element052,S_element015]
  conduct = 2
  density = 1
  expand = 3
  formula = G4_LANTHANUM_OXYSULFIDE
  name = G4_LANTHANUM_OXYSULFIDE
  specific = 4
FEATURE [App::DocumentObjectGroupPython] O_element053  label="O_element : 0.072"  # scripted group (container) (typed FeaturePython)
  n = 0.071682
FEATURE [App::DocumentObjectGroupPython] Pb_element002  label="Pb_element : 0.928"  # scripted group (container) (typed FeaturePython)
  n = 0.928318
FEATURE [App::DocumentObjectGroupPython] G4_LEAD_OXIDE  # scripted group (container) (typed FeaturePython)
  Dunit = g/cm3
  Dvalue = 9.53
  Group = -> [O_element053,Pb_element002]
  conduct = 2
  density = 1
  expand = 3
  formula = G4_LEAD_OXIDE
  name = G4_LEAD_OXIDE
  specific = 4
FEATURE [App::DocumentObjectGroupPython] Li_element001  label="Li_element : 1"  # scripted group (container) (typed FeaturePython)
  n = 1
  ref = Li_element
FEATURE [App::DocumentObjectGroupPython] N_element022  label="N_element : 011"  # scripted group (container) (typed FeaturePython)
  n = 1
  ref = N_element
FEATURE [App::DocumentObjectGroupPython] H_element049  label="H_element : 026"  # scripted group (container) (typed FeaturePython)
  n = 2
  ref = H_element
FEATURE [App::DocumentObjectGroupPython] G4_LITHIUM_AMIDE  # scripted group (container) (typed FeaturePython)
  Dunit = g/cm3
  Dvalue = 1.178
  Group = -> [Li_element001,N_element022,H_element049]
  conduct = 2
  density = 1
  expand = 3
  formula = G4_LITHIUM_AMIDE
  name = G4_LITHIUM_AMIDE
  specific = 4
FEATURE [App::DocumentObjectGroupPython] Li_element002  label="Li_element : 2"  # scripted group (container) (typed FeaturePython)
  n = 2
  ref = Li_element
FEATURE [App::DocumentObjectGroupPython] C_element055  label="C_element : 030"  # scripted group (container) (typed FeaturePython)
  n = 1
  ref = C_element
FEATURE [App::DocumentObjectGroupPython] O_element054  label="O_element : 028"  # scripted group (container) (typed FeaturePython)
  n = 3
  ref = O_element
FEATURE [App::DocumentObjectGroupPython] G4_LITHIUM_CARBONATE  # scripted group (container) (typed FeaturePython)
  Dunit = g/cm3
  Dvalue = 2.11
  Group = -> [Li_element002,C_element055,O_element054]
  conduct = 2
  density = 1
  expand = 3
  formula = G4_LITHIUM_CARBONATE
  name = G4_LITHIUM_CARBONATE
  specific = 4
FEATURE [App::DocumentObjectGroupPython] Li_element003  label="Li_element : 003"  # scripted group (container) (typed FeaturePython)
  n = 1
  ref = Li_element
FEATURE [App::DocumentObjectGroupPython] F_element012  label="F_element : 004"  # scripted group (container) (typed FeaturePython)
  n = 1
  ref = F_element
FEATURE [App::DocumentObjectGroupPython] G4_LITHIUM_FLUORIDE  # scripted group (container) (typed FeaturePython)
  Dunit = g/cm3
  Dvalue = 2.635
  Group = -> [Li_element003,F_element012]
  conduct = 2
  density = 1
  expand = 3
  formula = G4_LITHIUM_FLUORIDE
  name = G4_LITHIUM_FLUORIDE
  specific = 4
FEATURE [App::DocumentObjectGroupPython] Li_element004  label="Li_element : 004"  # scripted group (container) (typed FeaturePython)
  n = 1
  ref = Li_element
FEATURE [App::DocumentObjectGroupPython] H_element050  label="H_element : 027"  # scripted group (container) (typed FeaturePython)
  n = 1
  ref = H_element
FEATURE [App::DocumentObjectGroupPython] G4_LITHIUM_HYDRIDE  # scripted group (container) (typed FeaturePython)
  Dunit = g/cm3
  Dvalue = 0.82
  Group = -> [Li_element004,H_element050]
  conduct = 2
  density = 1
  expand = 3
  formula = G4_LITHIUM_HYDRIDE
  name = G4_LITHIUM_HYDRIDE
  specific = 4
FEATURE [App::DocumentObjectGroupPython] Li_element005  label="Li_element : 005"  # scripted group (container) (typed FeaturePython)
  n = 1
  ref = Li_element
FEATURE [App::DocumentObjectGroupPython] I_element003  label="I_element : 002"  # scripted group (container) (typed FeaturePython)
  n = 1
  ref = I_element
FEATURE [App::DocumentObjectGroupPython] G4_LITHIUM_IODIDE  # scripted group (container) (typed FeaturePython)
  Dunit = g/cm3
  Dvalue = 3.494
  Group = -> [Li_element005,I_element003]
  conduct = 2
  density = 1
  expand = 3
  formula = G4_LITHIUM_IODIDE
  name = G4_LITHIUM_IODIDE
  specific = 4
FEATURE [App::DocumentObjectGroupPython] Li_element006  label="Li_element : 006"  # scripted group (container) (typed FeaturePython)
  n = 2
  ref = Li_element
FEATURE [App::DocumentObjectGroupPython] O_element055  label="O_element : 029"  # scripted group (container) (typed FeaturePython)
  n = 1
  ref = O_element
FEATURE [App::DocumentObjectGroupPython] G4_LITHIUM_OXIDE  # scripted group (container) (typed FeaturePython)
  Dunit = g/cm3
  Dvalue = 2.013
  Group = -> [Li_element006,O_element055]
  conduct = 2
  density = 1
  expand = 3
  formula = G4_LITHIUM_OXIDE
  name = G4_LITHIUM_OXIDE
  specific = 4
FEATURE [App::DocumentObjectGroupPython] Li_element007  label="Li_element : 007"  # scripted group (container) (typed FeaturePython)
  n = 2
  ref = Li_element
FEATURE [App::DocumentObjectGroupPython] B_element005  label="B_element : 005"  # scripted group (container) (typed FeaturePython)
  n = 4
  ref = B_element
FEATURE [App::DocumentObjectGroupPython] O_element056  label="O_element : 7"  # scripted group (container) (typed FeaturePython)
  n = 7
  ref = O_element
FEATURE [App::DocumentObjectGroupPython] G4_LITHIUM_TETRABORATE  # scripted group (container) (typed FeaturePython)
  Dunit = g/cm3
  Dvalue = 2.44
  Group = -> [Li_element007,B_element005,O_element056]
  conduct = 2
  density = 1
  expand = 3
  formula = G4_LITHIUM_TETRABORATE
  name = G4_LITHIUM_TETRABORATE
  specific = 4
FEATURE [App::DocumentObjectGroupPython] H_element051  label="H_element : 0.105"  # scripted group (container) (typed FeaturePython)
  n = 0.105
FEATURE [App::DocumentObjectGroupPython] C_element056  label="C_element : 0.083"  # scripted group (container) (typed FeaturePython)
  n = 0.083
FEATURE [App::DocumentObjectGroupPython] N_element023  label="N_element : 0.023"  # scripted group (container) (typed FeaturePython)
  n = 0.023
FEATURE [App::DocumentObjectGroupPython] O_element057  label="O_element : 0.779"  # scripted group (container) (typed FeaturePython)
  n = 0.779
FEATURE [App::DocumentObjectGroupPython] Na_element010  label="Na_element : 0.097"  # scripted group (container) (typed FeaturePython)
  n = 0.002
FEATURE [App::DocumentObjectGroupPython] P_element006  label="P_element : 0.105"  # scripted group (container) (typed FeaturePython)
  n = 0.001
FEATURE [App::DocumentObjectGroupPython] S_element016  label="S_element : 0.017"  # scripted group (container) (typed FeaturePython)
  n = 0.002
FEATURE [App::DocumentObjectGroupPython] Cl_element014  label="Cl_element : 0.587"  # scripted group (container) (typed FeaturePython)
  n = 0.003
FEATURE [App::DocumentObjectGroupPython] K_element005  label="K_element : 0.015"  # scripted group (container) (typed FeaturePython)
  n = 0.002
FEATURE [App::DocumentObjectGroupPython] G4_LUNG_ICRP  # scripted group (container) (typed FeaturePython)
  Dunit = g/cm3
  Dvalue = 1.04
  Group = -> [H_element051,C_element056,N_element023,O_element057,Na_element010,P_element006,S_element016,Cl_element014,K_element005]
  conduct = 2
  density = 1
  expand = 3
  formula = G4_LUNG_ICRP
  name = G4_LUNG_ICRP
  specific = 4
FEATURE [App::DocumentObjectGroupPython] H_element052  label="H_element : 0.116"  # scripted group (container) (typed FeaturePython)
  n = 0.114318
FEATURE [App::DocumentObjectGroupPython] C_element057  label="C_element : 0.656"  # scripted group (container) (typed FeaturePython)
  n = 0.655824
FEATURE [App::DocumentObjectGroupPython] O_element058  label="O_element : 0.092"  # scripted group (container) (typed FeaturePython)
  n = 0.0921831
FEATURE [App::DocumentObjectGroupPython] Mg_element004  label="Mg_element : 0.135"  # scripted group (container) (typed FeaturePython)
  n = 0.134792
FEATURE [App::DocumentObjectGroupPython] Ca_element013  label="Ca_element : 0.003"  # scripted group (container) (typed FeaturePython)
  n = 0.002883
FEATURE [App::DocumentObjectGroupPython] G4_M3_WAX  # scripted group (container) (typed FeaturePython)
  Dunit = g/cm3
  Dvalue = 1.05
  Group = -> [H_element052,C_element057,O_element058,Mg_element004,Ca_element013]
  conduct = 2
  density = 1
  expand = 3
  formula = G4_M3_WAX
  name = G4_M3_WAX
  specific = 4
FEATURE [App::DocumentObjectGroupPython] Mg_element005  label="Mg_element : 1"  # scripted group (container) (typed FeaturePython)
  n = 1
  ref = Mg_element
FEATURE [App::DocumentObjectGroupPython] C_element058  label="C_element : 031"  # scripted group (container) (typed FeaturePython)
  n = 1
  ref = C_element
FEATURE [App::DocumentObjectGroupPython] O_element059  label="O_element : 030"  # scripted group (container) (typed FeaturePython)
  n = 3
  ref = O_element
FEATURE [App::DocumentObjectGroupPython] G4_MAGNESIUM_CARBONATE  # scripted group (container) (typed FeaturePython)
  Dunit = g/cm3
  Dvalue = 2.958
  Group = -> [Mg_element005,C_element058,O_element059]
  conduct = 2
  density = 1
  expand = 3
  formula = G4_MAGNESIUM_CARBONATE
  name = G4_MAGNESIUM_CARBONATE
  specific = 4
FEATURE [App::DocumentObjectGroupPython] Mg_element006  label="Mg_element : 002"  # scripted group (container) (typed FeaturePython)
  n = 1
  ref = Mg_element
FEATURE [App::DocumentObjectGroupPython] F_element013  label="F_element : 005"  # scripted group (container) (typed FeaturePython)
  n = 2
  ref = F_element
FEATURE [App::DocumentObjectGroupPython] G4_MAGNESIUM_FLUORIDE  # scripted group (container) (typed FeaturePython)
  Dunit = g/cm3
  Dvalue = 3
  Group = -> [Mg_element006,F_element013]
  conduct = 2
  density = 1
  expand = 3
  formula = G4_MAGNESIUM_FLUORIDE
  name = G4_MAGNESIUM_FLUORIDE
  specific = 4
FEATURE [App::DocumentObjectGroupPython] Mg_element007  label="Mg_element : 003"  # scripted group (container) (typed FeaturePython)
  n = 1
  ref = Mg_element
FEATURE [App::DocumentObjectGroupPython] O_element060  label="O_element : 031"  # scripted group (container) (typed FeaturePython)
  n = 1
  ref = O_element
FEATURE [App::DocumentObjectGroupPython] G4_MAGNESIUM_OXIDE  # scripted group (container) (typed FeaturePython)
  Dunit = g/cm3
  Dvalue = 3.58
  Group = -> [Mg_element007,O_element060]
  conduct = 2
  density = 1
  expand = 3
  formula = G4_MAGNESIUM_OXIDE
  name = G4_MAGNESIUM_OXIDE
  specific = 4
FEATURE [App::DocumentObjectGroupPython] Mg_element008  label="Mg_element : 004"  # scripted group (container) (typed FeaturePython)
  n = 1
  ref = Mg_element
FEATURE [App::DocumentObjectGroupPython] B_element006  label="B_element : 006"  # scripted group (container) (typed FeaturePython)
  n = 4
  ref = B_element
FEATURE [App::DocumentObjectGroupPython] O_element061  label="O_element : 032"  # scripted group (container) (typed FeaturePython)
  n = 7
  ref = O_element
FEATURE [App::DocumentObjectGroupPython] G4_MAGNESIUM_TETRABORATE  # scripted group (container) (typed FeaturePython)
  Dunit = g/cm3
  Dvalue = 2.53
  Group = -> [Mg_element008,B_element006,O_element061]
  conduct = 2
  density = 1
  expand = 3
  formula = G4_MAGNESIUM_TETRABORATE
  name = G4_MAGNESIUM_TETRABORATE
  specific = 4
FEATURE [App::DocumentObjectGroupPython] Hg_element001  label="Hg_element : 1"  # scripted group (container) (typed FeaturePython)
  n = 1
  ref = Hg_element
FEATURE [App::DocumentObjectGroupPython] I_element004  label="I_element : 2"  # scripted group (container) (typed FeaturePython)
  n = 2
  ref = I_element
FEATURE [App::DocumentObjectGroupPython] G4_MERCURIC_IODIDE  # scripted group (container) (typed FeaturePython)
  Dunit = g/cm3
  Dvalue = 6.36
  Group = -> [Hg_element001,I_element004]
  conduct = 2
  density = 1
  expand = 3
  formula = G4_MERCURIC_IODIDE
  name = G4_MERCURIC_IODIDE
  specific = 4
FEATURE [App::DocumentObjectGroupPython] C_element059  label="C_element : 032"  # scripted group (container) (typed FeaturePython)
  n = 1
  ref = C_element
FEATURE [App::DocumentObjectGroupPython] H_element053  label="H_element : 028"  # scripted group (container) (typed FeaturePython)
  n = 4
  ref = H_element
FEATURE [App::DocumentObjectGroupPython] G4_METHANE  # scripted group (container) (typed FeaturePython)
  Dunit = g/cm3
  Dvalue = 0.000667151
  Group = -> [C_element059,H_element053]
  conduct = 2
  density = 1
  expand = 3
  formula = G4_METHANE
  name = G4_METHANE
  specific = 4
FEATURE [App::DocumentObjectGroupPython] C_element060  label="C_element : 033"  # scripted group (container) (typed FeaturePython)
  n = 1
  ref = C_element
FEATURE [App::DocumentObjectGroupPython] H_element054  label="H_element : 029"  # scripted group (container) (typed FeaturePython)
  n = 4
  ref = H_element
FEATURE [App::DocumentObjectGroupPython] O_element062  label="O_element : 033"  # scripted group (container) (typed FeaturePython)
  n = 1
  ref = O_element
FEATURE [App::DocumentObjectGroupPython] G4_METHANOL  # scripted group (container) (typed FeaturePython)
  Dunit = g/cm3
  Dvalue = 0.7914
  Group = -> [C_element060,H_element054,O_element062]
  conduct = 2
  density = 1
  expand = 3
  formula = G4_METHANOL
  name = G4_METHANOL
  specific = 4
FEATURE [App::DocumentObjectGroupPython] H_element055  label="H_element : 0.134"  # scripted group (container) (typed FeaturePython)
  n = 0.13404
FEATURE [App::DocumentObjectGroupPython] C_element061  label="C_element : 0.778"  # scripted group (container) (typed FeaturePython)
  n = 0.77796
FEATURE [App::DocumentObjectGroupPython] O_element063  label="O_element : 0.035"  # scripted group (container) (typed FeaturePython)
  n = 0.03502
FEATURE [App::DocumentObjectGroupPython] Mg_element009  label="Mg_element : 0.039"  # scripted group (container) (typed FeaturePython)
  n = 0.038594
FEATURE [App::DocumentObjectGroupPython] Ti_element002  label="Ti_element : 0.014"  # scripted group (container) (typed FeaturePython)
  n = 0.014386
FEATURE [App::DocumentObjectGroupPython] G4_MIX_D_WAX  # scripted group (container) (typed FeaturePython)
  Dunit = g/cm3
  Dvalue = 0.99
  Group = -> [H_element055,C_element061,O_element063,Mg_element009,Ti_element002]
  conduct = 2
  density = 1
  expand = 3
  formula = G4_MIX_D_WAX
  name = G4_MIX_D_WAX
  specific = 4
FEATURE [App::DocumentObjectGroupPython] H_element056  label="H_element : 0.135"  # scripted group (container) (typed FeaturePython)
  n = 0.081192
FEATURE [App::DocumentObjectGroupPython] C_element062  label="C_element : 0.583"  # scripted group (container) (typed FeaturePython)
  n = 0.583442
FEATURE [App::DocumentObjectGroupPython] N_element024  label="N_element : 0.018"  # scripted group (container) (typed FeaturePython)
  n = 0.017798
FEATURE [App::DocumentObjectGroupPython] O_element064  label="O_element : 0.186"  # scripted group (container) (typed FeaturePython)
  n = 0.186381
FEATURE [App::DocumentObjectGroupPython] Mg_element010  label="Mg_element : 0.130"  # scripted group (container) (typed FeaturePython)
  n = 0.130287
FEATURE [App::DocumentObjectGroupPython] Cl_element015  label="Cl_element : 0.588"  # scripted group (container) (typed FeaturePython)
  n = 0.0009
FEATURE [App::DocumentObjectGroupPython] G4_MS20_TISSUE  # scripted group (container) (typed FeaturePython)
  Dunit = g/cm3
  Dvalue = 1
  Group = -> [H_element056,C_element062,N_element024,O_element064,Mg_element010,Cl_element015]
  conduct = 2
  density = 1
  expand = 3
  formula = G4_MS20_TISSUE
  name = G4_MS20_TISSUE
  specific = 4
FEATURE [App::DocumentObjectGroupPython] H_element057  label="H_element : 0.136"  # scripted group (container) (typed FeaturePython)
  n = 0.102
FEATURE [App::DocumentObjectGroupPython] C_element063  label="C_element : 0.143"  # scripted group (container) (typed FeaturePython)
  n = 0.143
FEATURE [App::DocumentObjectGroupPython] N_element025  label="N_element : 0.034"  # scripted group (container) (typed FeaturePython)
  n = 0.034
FEATURE [App::DocumentObjectGroupPython] O_element065  label="O_element : 0.710"  # scripted group (container) (typed FeaturePython)
  n = 0.71
FEATURE [App::DocumentObjectGroupPython] Na_element011  label="Na_element : 0.098"  # scripted group (container) (typed FeaturePython)
  n = 0.001
FEATURE [App::DocumentObjectGroupPython] P_element007  label="P_element : 0.002"  # scripted group (container) (typed FeaturePython)
  n = 0.002
FEATURE [App::DocumentObjectGroupPython] S_element017  label="S_element : 0.018"  # scripted group (container) (typed FeaturePython)
  n = 0.003
FEATURE [App::DocumentObjectGroupPython] Cl_element016  label="Cl_element : 0.589"  # scripted group (container) (typed FeaturePython)
  n = 0.001
FEATURE [App::DocumentObjectGroupPython] K_element006  label="K_element : 0.004"  # scripted group (container) (typed FeaturePython)
  n = 0.004
FEATURE [App::DocumentObjectGroupPython] G4_MUSCLE_SKELETAL_ICRP  # scripted group (container) (typed FeaturePython)
  Dunit = g/cm3
  Dvalue = 1.05
  Group = -> [H_element057,C_element063,N_element025,O_element065,Na_element011,P_element007,S_element017,Cl_element016,K_element006]
  conduct = 2
  density = 1
  expand = 3
  formula = G4_MUSCLE_SKELETAL_ICRP
  name = G4_MUSCLE_SKELETAL_ICRP
  specific = 4
FEATURE [App::DocumentObjectGroupPython] H_element058  label="H_element : 0.137"  # scripted group (container) (typed FeaturePython)
  n = 0.102102
FEATURE [App::DocumentObjectGroupPython] C_element064  label="C_element : 0.123"  # scripted group (container) (typed FeaturePython)
  n = 0.123123
FEATURE [App::DocumentObjectGroupPython] N_element026  label="N_element : 0.756"  # scripted group (container) (typed FeaturePython)
  n = 0.035035
FEATURE [App::DocumentObjectGroupPython] O_element066  label="O_element : 0.730"  # scripted group (container) (typed FeaturePython)
  n = 0.72973
FEATURE [App::DocumentObjectGroupPython] Na_element012  label="Na_element : 0.099"  # scripted group (container) (typed FeaturePython)
  n = 0.001001
FEATURE [App::DocumentObjectGroupPython] P_element008  label="P_element : 0.106"  # scripted group (container) (typed FeaturePython)
  n = 0.002002
FEATURE [App::DocumentObjectGroupPython] S_element018  label="S_element : 0.019"  # scripted group (container) (typed FeaturePython)
  n = 0.004004
FEATURE [App::DocumentObjectGroupPython] K_element007  label="K_element : 0.016"  # scripted group (container) (typed FeaturePython)
  n = 0.003003
FEATURE [App::DocumentObjectGroupPython] G4_MUSCLE_STRIATED_ICRU  # scripted group (container) (typed FeaturePython)
  Dunit = g/cm3
  Dvalue = 1.04
  Group = -> [H_element058,C_element064,N_element026,O_element066,Na_element012,P_element008,S_element018,K_element007]
  conduct = 2
  density = 1
  expand = 3
  formula = G4_MUSCLE_STRIATED_ICRU
  name = G4_MUSCLE_STRIATED_ICRU
  specific = 4
FEATURE [App::DocumentObjectGroupPython] H_element059  label="H_element : 0.098"  # scripted group (container) (typed FeaturePython)
  n = 0.0982341
FEATURE [App::DocumentObjectGroupPython] C_element065  label="C_element : 0.156"  # scripted group (container) (typed FeaturePython)
  n = 0.156214
FEATURE [App::DocumentObjectGroupPython] N_element027  label="N_element : 0.757"  # scripted group (container) (typed FeaturePython)
  n = 0.035451
FEATURE [App::DocumentObjectGroupPython] O_element067  label="O_element : 0.880"  # scripted group (container) (typed FeaturePython)
  n = 0.710101
FEATURE [App::DocumentObjectGroupPython] G4_MUSCLE_WITH_SUCROSE  # scripted group (container) (typed FeaturePython)
  Dunit = g/cm3
  Dvalue = 1.11
  Group = -> [H_element059,C_element065,N_element027,O_element067]
  conduct = 2
  density = 1
  expand = 3
  formula = G4_MUSCLE_WITH_SUCROSE
  name = G4_MUSCLE_WITH_SUCROSE
  specific = 4
FEATURE [App::DocumentObjectGroupPython] H_element060  label="H_element : 0.138"  # scripted group (container) (typed FeaturePython)
  n = 0.101969
FEATURE [App::DocumentObjectGroupPython] C_element066  label="C_element : 0.120"  # scripted group (container) (typed FeaturePython)
  n = 0.120058
FEATURE [App::DocumentObjectGroupPython] N_element028  label="N_element : 0.758"  # scripted group (container) (typed FeaturePython)
  n = 0.035451
FEATURE [App::DocumentObjectGroupPython] O_element068  label="O_element : 0.743"  # scripted group (container) (typed FeaturePython)
  n = 0.742522
FEATURE [App::DocumentObjectGroupPython] G4_MUSCLE_WITHOUT_SUCROSE  # scripted group (container) (typed FeaturePython)
  Dunit = g/cm3
  Dvalue = 1.07
  Group = -> [H_element060,C_element066,N_element028,O_element068]
  conduct = 2
  density = 1
  expand = 3
  formula = G4_MUSCLE_WITHOUT_SUCROSE
  name = G4_MUSCLE_WITHOUT_SUCROSE
  specific = 4
FEATURE [App::DocumentObjectGroupPython] C_element067  label="C_element : 10"  # scripted group (container) (typed FeaturePython)
  n = 10
  ref = C_element
FEATURE [App::DocumentObjectGroupPython] H_element061  label="H_element : 030"  # scripted group (container) (typed FeaturePython)
  n = 8
  ref = H_element
FEATURE [App::DocumentObjectGroupPython] G4_NAPHTHALENE  # scripted group (container) (typed FeaturePython)
  Dunit = g/cm3
  Dvalue = 1.145
  Group = -> [C_element067,H_element061]
  conduct = 2
  density = 1
  expand = 3
  formula = G4_NAPHTHALENE
  name = G4_NAPHTHALENE
  specific = 4
FEATURE [App::DocumentObjectGroupPython] C_element068  label="C_element : 034"  # scripted group (container) (typed FeaturePython)
  n = 6
  ref = C_element
FEATURE [App::DocumentObjectGroupPython] H_element062  label="H_element : 031"  # scripted group (container) (typed FeaturePython)
  n = 5
  ref = H_element
FEATURE [App::DocumentObjectGroupPython] N_element029  label="N_element : 012"  # scripted group (container) (typed FeaturePython)
  n = 1
  ref = N_element
FEATURE [App::DocumentObjectGroupPython] O_element069  label="O_element : 034"  # scripted group (container) (typed FeaturePython)
  n = 2
  ref = O_element
FEATURE [App::DocumentObjectGroupPython] G4_NITROBENZENE  # scripted group (container) (typed FeaturePython)
  Dunit = g/cm3
  Dvalue = 1.19867
  Group = -> [C_element068,H_element062,N_element029,O_element069]
  conduct = 2
  density = 1
  expand = 3
  formula = G4_NITROBENZENE
  name = G4_NITROBENZENE
  specific = 4
FEATURE [App::DocumentObjectGroupPython] N_element030  label="N_element : 013"  # scripted group (container) (typed FeaturePython)
  n = 2
  ref = N_element
FEATURE [App::DocumentObjectGroupPython] O_element070  label="O_element : 035"  # scripted group (container) (typed FeaturePython)
  n = 1
  ref = O_element
FEATURE [App::DocumentObjectGroupPython] G4_NITROUS_OXIDE  # scripted group (container) (typed FeaturePython)
  Dunit = g/cm3
  Dvalue = 0.00183094
  Group = -> [N_element030,O_element070]
  conduct = 2
  density = 1
  expand = 3
  formula = G4_NITROUS_OXIDE
  name = G4_NITROUS_OXIDE
  specific = 4
FEATURE [App::DocumentObjectGroupPython] H_element063  label="H_element : 0.104"  # scripted group (container) (typed FeaturePython)
  n = 0.103509
FEATURE [App::DocumentObjectGroupPython] C_element069  label="C_element : 0.648"  # scripted group (container) (typed FeaturePython)
  n = 0.648416
FEATURE [App::DocumentObjectGroupPython] N_element031  label="N_element : 0.100"  # scripted group (container) (typed FeaturePython)
  n = 0.0995361
FEATURE [App::DocumentObjectGroupPython] O_element071  label="O_element : 0.149"  # scripted group (container) (typed FeaturePython)
  n = 0.148539
FEATURE [App::DocumentObjectGroupPython] G4_NYLON_8062  label="G4_NYLON-8062"  # scripted group (container) (typed FeaturePython)
  Dunit = g/cm3
  Dvalue = 1.08
  Group = -> [H_element063,C_element069,N_element031,O_element071]
  conduct = 2
  density = 1
  expand = 3
  formula = G4_NYLON-8062
  name = G4_NYLON-8062
  specific = 4
FEATURE [App::DocumentObjectGroupPython] C_element070  label="C_element : 035"  # scripted group (container) (typed FeaturePython)
  n = 6
  ref = C_element
FEATURE [App::DocumentObjectGroupPython] H_element064  label="H_element : 11"  # scripted group (container) (typed FeaturePython)
  n = 11
  ref = H_element
FEATURE [App::DocumentObjectGroupPython] N_element032  label="N_element : 014"  # scripted group (container) (typed FeaturePython)
  n = 1
  ref = N_element
FEATURE [App::DocumentObjectGroupPython] O_element072  label="O_element : 036"  # scripted group (container) (typed FeaturePython)
  n = 1
  ref = O_element
FEATURE [App::DocumentObjectGroupPython] G4_NYLON_6_6  label="G4_NYLON-6-6"  # scripted group (container) (typed FeaturePython)
  Dunit = g/cm3
  Dvalue = 1.14
  Group = -> [C_element070,H_element064,N_element032,O_element072]
  conduct = 2
  density = 1
  expand = 3
  formula = G4_NYLON-6-6
  name = G4_NYLON-6-6
  specific = 4
FEATURE [App::DocumentObjectGroupPython] H_element065  label="H_element : 0.139"  # scripted group (container) (typed FeaturePython)
  n = 0.107062
FEATURE [App::DocumentObjectGroupPython] C_element071  label="C_element : 0.680"  # scripted group (container) (typed FeaturePython)
  n = 0.680449
FEATURE [App::DocumentObjectGroupPython] N_element033  label="N_element : 0.099"  # scripted group (container) (typed FeaturePython)
  n = 0.099189
FEATURE [App::DocumentObjectGroupPython] O_element073  label="O_element : 0.113"  # scripted group (container) (typed FeaturePython)
  n = 0.1133
FEATURE [App::DocumentObjectGroupPython] G4_NYLON_6_10  label="G4_NYLON-6-10"  # scripted group (container) (typed FeaturePython)
  Dunit = g/cm3
  Dvalue = 1.14
  Group = -> [H_element065,C_element071,N_element033,O_element073]
  conduct = 2
  density = 1
  expand = 3
  formula = G4_NYLON-6-10
  name = G4_NYLON-6-10
  specific = 4
FEATURE [App::DocumentObjectGroupPython] H_element066  label="H_element : 0.140"  # scripted group (container) (typed FeaturePython)
  n = 0.115476
FEATURE [App::DocumentObjectGroupPython] C_element072  label="C_element : 0.721"  # scripted group (container) (typed FeaturePython)
  n = 0.720818
FEATURE [App::DocumentObjectGroupPython] N_element034  label="N_element : 0.076"  # scripted group (container) (typed FeaturePython)
  n = 0.0764169
FEATURE [App::DocumentObjectGroupPython] O_element074  label="O_element : 0.087"  # scripted group (container) (typed FeaturePython)
  n = 0.0872889
FEATURE [App::DocumentObjectGroupPython] G4_NYLON_11_RILSAN  label="G4_NYLON-11_RILSAN"  # scripted group (container) (typed FeaturePython)
  Dunit = g/cm3
  Dvalue = 1.425
  Group = -> [H_element066,C_element072,N_element034,O_element074]
  conduct = 2
  density = 1
  expand = 3
  formula = G4_NYLON-11_RILSAN
  name = G4_NYLON-11_RILSAN
  specific = 4
FEATURE [App::DocumentObjectGroupPython] C_element073  label="C_element : 8"  # scripted group (container) (typed FeaturePython)
  n = 8
  ref = C_element
FEATURE [App::DocumentObjectGroupPython] H_element067  label="H_element : 18"  # scripted group (container) (typed FeaturePython)
  n = 18
  ref = H_element
FEATURE [App::DocumentObjectGroupPython] G4_OCTANE  # scripted group (container) (typed FeaturePython)
  Dunit = g/cm3
  Dvalue = 0.7026
  Group = -> [C_element073,H_element067]
  conduct = 2
  density = 1
  expand = 3
  formula = G4_OCTANE
  name = G4_OCTANE
  specific = 4
FEATURE [App::DocumentObjectGroupPython] C_element074  label="C_element : 25"  # scripted group (container) (typed FeaturePython)
  n = 25
  ref = C_element
FEATURE [App::DocumentObjectGroupPython] H_element068  label="H_element : 52"  # scripted group (container) (typed FeaturePython)
  n = 52
  ref = H_element
FEATURE [App::DocumentObjectGroupPython] G4_PARAFFIN  # scripted group (container) (typed FeaturePython)
  Dunit = g/cm3
  Dvalue = 0.93
  Group = -> [C_element074,H_element068]
  conduct = 2
  density = 1
  expand = 3
  formula = G4_PARAFFIN
  name = G4_PARAFFIN
  specific = 4
FEATURE [App::DocumentObjectGroupPython] C_element075  label="C_element : 036"  # scripted group (container) (typed FeaturePython)
  n = 5
  ref = C_element
FEATURE [App::DocumentObjectGroupPython] H_element069  label="H_element : 032"  # scripted group (container) (typed FeaturePython)
  n = 12
  ref = H_element
FEATURE [App::DocumentObjectGroupPython] G4_N_PENTANE  label="G4_N-PENTANE"  # scripted group (container) (typed FeaturePython)
  Dunit = g/cm3
  Dvalue = 0.6262
  Group = -> [C_element075,H_element069]
  conduct = 2
  density = 1
  expand = 3
  formula = G4_N-PENTANE
  name = G4_N-PENTANE
  specific = 4
FEATURE [App::DocumentObjectGroupPython] H_element070  label="H_element : 0.014"  # scripted group (container) (typed FeaturePython)
  n = 0.0141
FEATURE [App::DocumentObjectGroupPython] C_element076  label="C_element : 0.072"  # scripted group (container) (typed FeaturePython)
  n = 0.072261
FEATURE [App::DocumentObjectGroupPython] N_element035  label="N_element : 0.019"  # scripted group (container) (typed FeaturePython)
  n = 0.01932
FEATURE [App::DocumentObjectGroupPython] O_element075  label="O_element : 0.066"  # scripted group (container) (typed FeaturePython)
  n = 0.066101
FEATURE [App::DocumentObjectGroupPython] S_element019  label="S_element : 0.020"  # scripted group (container) (typed FeaturePython)
  n = 0.00189
FEATURE [App::DocumentObjectGroupPython] Br_element004  label="Br_element : 0.349"  # scripted group (container) (typed FeaturePython)
  n = 0.349103
FEATURE [App::DocumentObjectGroupPython] Ag_element001  label="Ag_element : 0.474"  # scripted group (container) (typed FeaturePython)
  n = 0.474105
FEATURE [App::DocumentObjectGroupPython] I_element005  label="I_element : 0.003"  # scripted group (container) (typed FeaturePython)
  n = 0.00312
FEATURE [App::DocumentObjectGroupPython] G4_PHOTO_EMULSION  # scripted group (container) (typed FeaturePython)
  Dunit = g/cm3
  Dvalue = 3.815
  Group = -> [H_element070,C_element076,N_element035,O_element075,S_element019,Br_element004,Ag_element001,I_element005]
  conduct = 2
  density = 1
  expand = 3
  formula = G4_PHOTO_EMULSION
  name = G4_PHOTO_EMULSION
  specific = 4
FEATURE [App::DocumentObjectGroupPython] C_element077  label="C_element : 9"  # scripted group (container) (typed FeaturePython)
  n = 9
  ref = C_element
FEATURE [App::DocumentObjectGroupPython] H_element071  label="H_element : 033"  # scripted group (container) (typed FeaturePython)
  n = 10
  ref = H_element
FEATURE [App::DocumentObjectGroupPython] G4_PLASTIC_SC_VINYLTOLUENE  # scripted group (container) (typed FeaturePython)
  Dunit = g/cm3
  Dvalue = 1.032
  Group = -> [C_element077,H_element071]
  conduct = 2
  density = 1
  expand = 3
  formula = G4_PLASTIC_SC_VINYLTOLUENE
  name = G4_PLASTIC_SC_VINYLTOLUENE
  specific = 4
FEATURE [App::DocumentObjectGroupPython] Pu_element001  label="Pu_element : 1"  # scripted group (container) (typed FeaturePython)
  n = 1
  ref = Pu_element
FEATURE [App::DocumentObjectGroupPython] O_element076  label="O_element : 037"  # scripted group (container) (typed FeaturePython)
  n = 2
  ref = O_element
FEATURE [App::DocumentObjectGroupPython] G4_PLUTONIUM_DIOXIDE  # scripted group (container) (typed FeaturePython)
  Dunit = g/cm3
  Dvalue = 11.46
  Group = -> [Pu_element001,O_element076]
  conduct = 2
  density = 1
  expand = 3
  formula = G4_PLUTONIUM_DIOXIDE
  name = G4_PLUTONIUM_DIOXIDE
  specific = 4
FEATURE [App::DocumentObjectGroupPython] C_element078  label="C_element : 037"  # scripted group (container) (typed FeaturePython)
  n = 3
  ref = C_element
FEATURE [App::DocumentObjectGroupPython] H_element072  label="H_element : 034"  # scripted group (container) (typed FeaturePython)
  n = 3
  ref = H_element
FEATURE [App::DocumentObjectGroupPython] N_element036  label="N_element : 015"  # scripted group (container) (typed FeaturePython)
  n = 1
  ref = N_element
FEATURE [App::DocumentObjectGroupPython] G4_POLYACRYLONITRILE  # scripted group (container) (typed FeaturePython)
  Dunit = g/cm3
  Dvalue = 1.17
  Group = -> [C_element078,H_element072,N_element036]
  conduct = 2
  density = 1
  expand = 3
  formula = G4_POLYACRYLONITRILE
  name = G4_POLYACRYLONITRILE
  specific = 4
FEATURE [App::DocumentObjectGroupPython] C_element079  label="C_element : 16"  # scripted group (container) (typed FeaturePython)
  n = 16
  ref = C_element
FEATURE [App::DocumentObjectGroupPython] H_element073  label="H_element : 035"  # scripted group (container) (typed FeaturePython)
  n = 14
  ref = H_element
FEATURE [App::DocumentObjectGroupPython] O_element077  label="O_element : 038"  # scripted group (container) (typed FeaturePython)
  n = 3
  ref = O_element
FEATURE [App::DocumentObjectGroupPython] G4_POLYCARBONATE  # scripted group (container) (typed FeaturePython)
  Dunit = g/cm3
  Dvalue = 1.2
  Group = -> [C_element079,H_element073,O_element077]
  conduct = 2
  density = 1
  expand = 3
  formula = G4_POLYCARBONATE
  name = G4_POLYCARBONATE
  specific = 4
FEATURE [App::DocumentObjectGroupPython] C_element080  label="C_element : 038"  # scripted group (container) (typed FeaturePython)
  n = 8
  ref = C_element
FEATURE [App::DocumentObjectGroupPython] H_element074  label="H_element : 036"  # scripted group (container) (typed FeaturePython)
  n = 7
  ref = H_element
FEATURE [App::DocumentObjectGroupPython] Cl_element017  label="Cl_element : 007"  # scripted group (container) (typed FeaturePython)
  n = 1
  ref = Cl_element
FEATURE [App::DocumentObjectGroupPython] G4_POLYCHLOROSTYRENE  # scripted group (container) (typed FeaturePython)
  Dunit = g/cm3
  Dvalue = 1.3
  Group = -> [C_element080,H_element074,Cl_element017]
  conduct = 2
  density = 1
  expand = 3
  formula = G4_POLYCHLOROSTYRENE
  name = G4_POLYCHLOROSTYRENE
  specific = 4
FEATURE [App::DocumentObjectGroupPython] C_element081  label="C_element : 039"  # scripted group (container) (typed FeaturePython)
  n = 1
  ref = C_element
FEATURE [App::DocumentObjectGroupPython] H_element075  label="H_element : 037"  # scripted group (container) (typed FeaturePython)
  n = 2
  ref = H_element
FEATURE [App::DocumentObjectGroupPython] G4_POLYETHYLENE  # scripted group (container) (typed FeaturePython)
  Dunit = g/cm3
  Dvalue = 0.94
  Group = -> [C_element081,H_element075]
  conduct = 2
  density = 1
  expand = 3
  formula = G4_POLYETHYLENE
  name = G4_POLYETHYLENE
  specific = 4
FEATURE [App::DocumentObjectGroupPython] C_element082  label="C_element : 040"  # scripted group (container) (typed FeaturePython)
  n = 10
  ref = C_element
FEATURE [App::DocumentObjectGroupPython] H_element076  label="H_element : 038"  # scripted group (container) (typed FeaturePython)
  n = 8
  ref = H_element
FEATURE [App::DocumentObjectGroupPython] O_element078  label="O_element : 039"  # scripted group (container) (typed FeaturePython)
  n = 4
  ref = O_element
FEATURE [App::DocumentObjectGroupPython] G4_MYLAR  # scripted group (container) (typed FeaturePython)
  Dunit = g/cm3
  Dvalue = 1.4
  Group = -> [C_element082,H_element076,O_element078]
  conduct = 2
  density = 1
  expand = 3
  formula = G4_MYLAR
  name = G4_MYLAR
  specific = 4
FEATURE [App::DocumentObjectGroupPython] C_element083  label="C_element : 041"  # scripted group (container) (typed FeaturePython)
  n = 5
  ref = C_element
FEATURE [App::DocumentObjectGroupPython] H_element077  label="H_element : 039"  # scripted group (container) (typed FeaturePython)
  n = 8
  ref = H_element
FEATURE [App::DocumentObjectGroupPython] O_element079  label="O_element : 040"  # scripted group (container) (typed FeaturePython)
  n = 2
  ref = O_element
FEATURE [App::DocumentObjectGroupPython] G4_PLEXIGLASS  # scripted group (container) (typed FeaturePython)
  Dunit = g/cm3
  Dvalue = 1.19
  Group = -> [C_element083,H_element077,O_element079]
  conduct = 2
  density = 1
  expand = 3
  formula = G4_PLEXIGLASS
  name = G4_PLEXIGLASS
  specific = 4
FEATURE [App::DocumentObjectGroupPython] C_element084  label="C_element : 042"  # scripted group (container) (typed FeaturePython)
  n = 1
  ref = C_element
FEATURE [App::DocumentObjectGroupPython] H_element078  label="H_element : 040"  # scripted group (container) (typed FeaturePython)
  n = 2
  ref = H_element
FEATURE [App::DocumentObjectGroupPython] O_element080  label="O_element : 041"  # scripted group (container) (typed FeaturePython)
  n = 1
  ref = O_element
FEATURE [App::DocumentObjectGroupPython] G4_POLYOXYMETHYLENE  # scripted group (container) (typed FeaturePython)
  Dunit = g/cm3
  Dvalue = 1.425
  Group = -> [C_element084,H_element078,O_element080]
  conduct = 2
  density = 1
  expand = 3
  formula = G4_POLYOXYMETHYLENE
  name = G4_POLYOXYMETHYLENE
  specific = 4
FEATURE [App::DocumentObjectGroupPython] C_element085  label="C_element : 043"  # scripted group (container) (typed FeaturePython)
  n = 2
  ref = C_element
FEATURE [App::DocumentObjectGroupPython] H_element079  label="H_element : 041"  # scripted group (container) (typed FeaturePython)
  n = 4
  ref = H_element
FEATURE [App::DocumentObjectGroupPython] G4_POLYPROPYLENE  # scripted group (container) (typed FeaturePython)
  Dunit = g/cm3
  Dvalue = 0.9
  Group = -> [C_element085,H_element079]
  conduct = 2
  density = 1
  expand = 3
  formula = G4_POLYPROPYLENE
  name = G4_POLYPROPYLENE
  specific = 4
FEATURE [App::DocumentObjectGroupPython] C_element086  label="C_element : 044"  # scripted group (container) (typed FeaturePython)
  n = 8
  ref = C_element
FEATURE [App::DocumentObjectGroupPython] H_element080  label="H_element : 042"  # scripted group (container) (typed FeaturePython)
  n = 8
  ref = H_element
FEATURE [App::DocumentObjectGroupPython] G4_POLYSTYRENE  # scripted group (container) (typed FeaturePython)
  Dunit = g/cm3
  Dvalue = 1.06
  Group = -> [C_element086,H_element080]
  conduct = 2
  density = 1
  expand = 3
  formula = G4_POLYSTYRENE
  name = G4_POLYSTYRENE
  specific = 4
FEATURE [App::DocumentObjectGroupPython] C_element087  label="C_element : 045"  # scripted group (container) (typed FeaturePython)
  n = 2
  ref = C_element
FEATURE [App::DocumentObjectGroupPython] F_element014  label="F_element : 4"  # scripted group (container) (typed FeaturePython)
  n = 4
  ref = F_element
FEATURE [App::DocumentObjectGroupPython] G4_TEFLON  # scripted group (container) (typed FeaturePython)
  Dunit = g/cm3
  Dvalue = 2.2
  Group = -> [C_element087,F_element014]
  conduct = 2
  density = 1
  expand = 3
  formula = G4_TEFLON
  name = G4_TEFLON
  specific = 4
FEATURE [App::DocumentObjectGroupPython] C_element088  label="C_element : 046"  # scripted group (container) (typed FeaturePython)
  n = 2
  ref = C_element
FEATURE [App::DocumentObjectGroupPython] F_element015  label="F_element : 006"  # scripted group (container) (typed FeaturePython)
  n = 3
  ref = F_element
FEATURE [App::DocumentObjectGroupPython] Cl_element018  label="Cl_element : 008"  # scripted group (container) (typed FeaturePython)
  n = 1
  ref = Cl_element
FEATURE [App::DocumentObjectGroupPython] G4_POLYTRIFLUOROCHLOROETHYLENE  # scripted group (container) (typed FeaturePython)
  Dunit = g/cm3
  Dvalue = 2.1
  Group = -> [C_element088,F_element015,Cl_element018]
  conduct = 2
  density = 1
  expand = 3
  formula = G4_POLYTRIFLUOROCHLOROETHYLENE
  name = G4_POLYTRIFLUOROCHLOROETHYLENE
  specific = 4
FEATURE [App::DocumentObjectGroupPython] C_element089  label="C_element : 047"  # scripted group (container) (typed FeaturePython)
  n = 4
  ref = C_element
FEATURE [App::DocumentObjectGroupPython] H_element081  label="H_element : 043"  # scripted group (container) (typed FeaturePython)
  n = 6
  ref = H_element
FEATURE [App::DocumentObjectGroupPython] O_element081  label="O_element : 042"  # scripted group (container) (typed FeaturePython)
  n = 2
  ref = O_element
FEATURE [App::DocumentObjectGroupPython] G4_POLYVINYL_ACETATE  # scripted group (container) (typed FeaturePython)
  Dunit = g/cm3
  Dvalue = 1.19
  Group = -> [C_element089,H_element081,O_element081]
  conduct = 2
  density = 1
  expand = 3
  formula = G4_POLYVINYL_ACETATE
  name = G4_POLYVINYL_ACETATE
  specific = 4
FEATURE [App::DocumentObjectGroupPython] C_element090  label="C_element : 048"  # scripted group (container) (typed FeaturePython)
  n = 2
  ref = C_element
FEATURE [App::DocumentObjectGroupPython] H_element082  label="H_element : 044"  # scripted group (container) (typed FeaturePython)
  n = 4
  ref = H_element
FEATURE [App::DocumentObjectGroupPython] O_element082  label="O_element : 043"  # scripted group (container) (typed FeaturePython)
  n = 1
  ref = O_element
FEATURE [App::DocumentObjectGroupPython] G4_POLYVINYL_ALCOHOL  # scripted group (container) (typed FeaturePython)
  Dunit = g/cm3
  Dvalue = 1.3
  Group = -> [C_element090,H_element082,O_element082]
  conduct = 2
  density = 1
  expand = 3
  formula = G4_POLYVINYL_ALCOHOL
  name = G4_POLYVINYL_ALCOHOL
  specific = 4
FEATURE [App::DocumentObjectGroupPython] C_element091  label="C_element : 049"  # scripted group (container) (typed FeaturePython)
  n = 8
  ref = C_element
FEATURE [App::DocumentObjectGroupPython] H_element083  label="H_element : 045"  # scripted group (container) (typed FeaturePython)
  n = 14
  ref = H_element
FEATURE [App::DocumentObjectGroupPython] O_element083  label="O_element : 044"  # scripted group (container) (typed FeaturePython)
  n = 2
  ref = O_element
FEATURE [App::DocumentObjectGroupPython] G4_POLYVINYL_BUTYRAL  # scripted group (container) (typed FeaturePython)
  Dunit = g/cm3
  Dvalue = 1.12
  Group = -> [C_element091,H_element083,O_element083]
  conduct = 2
  density = 1
  expand = 3
  formula = G4_POLYVINYL_BUTYRAL
  name = G4_POLYVINYL_BUTYRAL
  specific = 4
FEATURE [App::DocumentObjectGroupPython] C_element092  label="C_element : 050"  # scripted group (container) (typed FeaturePython)
  n = 2
  ref = C_element
FEATURE [App::DocumentObjectGroupPython] H_element084  label="H_element : 046"  # scripted group (container) (typed FeaturePython)
  n = 3
  ref = H_element
FEATURE [App::DocumentObjectGroupPython] Cl_element019  label="Cl_element : 009"  # scripted group (container) (typed FeaturePython)
  n = 1
  ref = Cl_element
FEATURE [App::DocumentObjectGroupPython] G4_POLYVINYL_CHLORIDE  # scripted group (container) (typed FeaturePython)
  Dunit = g/cm3
  Dvalue = 1.3
  Group = -> [C_element092,H_element084,Cl_element019]
  conduct = 2
  density = 1
  expand = 3
  formula = G4_POLYVINYL_CHLORIDE
  name = G4_POLYVINYL_CHLORIDE
  specific = 4
FEATURE [App::DocumentObjectGroupPython] C_element093  label="C_element : 051"  # scripted group (container) (typed FeaturePython)
  n = 2
  ref = C_element
FEATURE [App::DocumentObjectGroupPython] H_element085  label="H_element : 047"  # scripted group (container) (typed FeaturePython)
  n = 2
  ref = H_element
FEATURE [App::DocumentObjectGroupPython] Cl_element020  label="Cl_element : 010"  # scripted group (container) (typed FeaturePython)
  n = 2
  ref = Cl_element
FEATURE [App::DocumentObjectGroupPython] G4_POLYVINYLIDENE_CHLORIDE  # scripted group (container) (typed FeaturePython)
  Dunit = g/cm3
  Dvalue = 1.7
  Group = -> [C_element093,H_element085,Cl_element020]
  conduct = 2
  density = 1
  expand = 3
  formula = G4_POLYVINYLIDENE_CHLORIDE
  name = G4_POLYVINYLIDENE_CHLORIDE
  specific = 4
FEATURE [App::DocumentObjectGroupPython] C_element094  label="C_element : 052"  # scripted group (container) (typed FeaturePython)
  n = 2
  ref = C_element
FEATURE [App::DocumentObjectGroupPython] H_element086  label="H_element : 048"  # scripted group (container) (typed FeaturePython)
  n = 2
  ref = H_element
FEATURE [App::DocumentObjectGroupPython] F_element016  label="F_element : 007"  # scripted group (container) (typed FeaturePython)
  n = 2
  ref = F_element
FEATURE [App::DocumentObjectGroupPython] G4_POLYVINYLIDENE_FLUORIDE  # scripted group (container) (typed FeaturePython)
  Dunit = g/cm3
  Dvalue = 1.76
  Group = -> [C_element094,H_element086,F_element016]
  conduct = 2
  density = 1
  expand = 3
  formula = G4_POLYVINYLIDENE_FLUORIDE
  name = G4_POLYVINYLIDENE_FLUORIDE
  specific = 4
FEATURE [App::DocumentObjectGroupPython] C_element095  label="C_element : 053"  # scripted group (container) (typed FeaturePython)
  n = 6
  ref = C_element
FEATURE [App::DocumentObjectGroupPython] H_element087  label="H_element : 9"  # scripted group (container) (typed FeaturePython)
  n = 9
  ref = H_element
FEATURE [App::DocumentObjectGroupPython] N_element037  label="N_element : 016"  # scripted group (container) (typed FeaturePython)
  n = 1
  ref = N_element
FEATURE [App::DocumentObjectGroupPython] O_element084  label="O_element : 045"  # scripted group (container) (typed FeaturePython)
  n = 1
  ref = O_element
FEATURE [App::DocumentObjectGroupPython] G4_POLYVINYL_PYRROLIDONE  # scripted group (container) (typed FeaturePython)
  Dunit = g/cm3
  Dvalue = 1.25
  Group = -> [C_element095,H_element087,N_element037,O_element084]
  conduct = 2
  density = 1
  expand = 3
  formula = G4_POLYVINYL_PYRROLIDONE
  name = G4_POLYVINYL_PYRROLIDONE
  specific = 4
FEATURE [App::DocumentObjectGroupPython] K_element008  label="K_element : 1"  # scripted group (container) (typed FeaturePython)
  n = 1
  ref = K_element
FEATURE [App::DocumentObjectGroupPython] I_element006  label="I_element : 003"  # scripted group (container) (typed FeaturePython)
  n = 1
  ref = I_element
FEATURE [App::DocumentObjectGroupPython] G4_POTASSIUM_IODIDE  # scripted group (container) (typed FeaturePython)
  Dunit = g/cm3
  Dvalue = 3.13
  Group = -> [K_element008,I_element006]
  conduct = 2
  density = 1
  expand = 3
  formula = G4_POTASSIUM_IODIDE
  name = G4_POTASSIUM_IODIDE
  specific = 4
FEATURE [App::DocumentObjectGroupPython] K_element009  label="K_element : 2"  # scripted group (container) (typed FeaturePython)
  n = 2
  ref = K_element
FEATURE [App::DocumentObjectGroupPython] O_element085  label="O_element : 046"  # scripted group (container) (typed FeaturePython)
  n = 1
  ref = O_element
FEATURE [App::DocumentObjectGroupPython] G4_POTASSIUM_OXIDE  # scripted group (container) (typed FeaturePython)
  Dunit = g/cm3
  Dvalue = 2.32
  Group = -> [K_element009,O_element085]
  conduct = 2
  density = 1
  expand = 3
  formula = G4_POTASSIUM_OXIDE
  name = G4_POTASSIUM_OXIDE
  specific = 4
FEATURE [App::DocumentObjectGroupPython] C_element096  label="C_element : 054"  # scripted group (container) (typed FeaturePython)
  n = 3
  ref = C_element
FEATURE [App::DocumentObjectGroupPython] H_element088  label="H_element : 049"  # scripted group (container) (typed FeaturePython)
  n = 8
  ref = H_element
FEATURE [App::DocumentObjectGroupPython] G4_PROPANE  # scripted group (container) (typed FeaturePython)
  Dunit = g/cm3
  Dvalue = 0.00187939
  Group = -> [C_element096,H_element088]
  conduct = 2
  density = 1
  expand = 3
  formula = G4_PROPANE
  name = G4_PROPANE
  specific = 4
FEATURE [App::DocumentObjectGroupPython] C_element097  label="C_element : 055"  # scripted group (container) (typed FeaturePython)
  n = 3
  ref = C_element
FEATURE [App::DocumentObjectGroupPython] H_element089  label="H_element : 050"  # scripted group (container) (typed FeaturePython)
  n = 8
  ref = H_element
FEATURE [App::DocumentObjectGroupPython] G4_lPROPANE  # scripted group (container) (typed FeaturePython)
  Dunit = g/cm3
  Dvalue = 0.43
  Group = -> [C_element097,H_element089]
  conduct = 2
  density = 1
  expand = 3
  formula = G4_lPROPANE
  name = G4_lPROPANE
  specific = 4
FEATURE [App::DocumentObjectGroupPython] C_element098  label="C_element : 056"  # scripted group (container) (typed FeaturePython)
  n = 3
  ref = C_element
FEATURE [App::DocumentObjectGroupPython] H_element090  label="H_element : 051"  # scripted group (container) (typed FeaturePython)
  n = 8
  ref = H_element
FEATURE [App::DocumentObjectGroupPython] O_element086  label="O_element : 047"  # scripted group (container) (typed FeaturePython)
  n = 1
  ref = O_element
FEATURE [App::DocumentObjectGroupPython] G4_N_PROPYL_ALCOHOL  label="G4_N-PROPYL_ALCOHOL"  # scripted group (container) (typed FeaturePython)
  Dunit = g/cm3
  Dvalue = 0.8035
  Group = -> [C_element098,H_element090,O_element086]
  conduct = 2
  density = 1
  expand = 3
  formula = G4_N-PROPYL_ALCOHOL
  name = G4_N-PROPYL_ALCOHOL
  specific = 4
FEATURE [App::DocumentObjectGroupPython] C_element099  label="C_element : 057"  # scripted group (container) (typed FeaturePython)
  n = 5
  ref = C_element
FEATURE [App::DocumentObjectGroupPython] H_element091  label="H_element : 052"  # scripted group (container) (typed FeaturePython)
  n = 5
  ref = H_element
FEATURE [App::DocumentObjectGroupPython] N_element038  label="N_element : 017"  # scripted group (container) (typed FeaturePython)
  n = 1
  ref = N_element
FEATURE [App::DocumentObjectGroupPython] G4_PYRIDINE  # scripted group (container) (typed FeaturePython)
  Dunit = g/cm3
  Dvalue = 0.9819
  Group = -> [C_element099,H_element091,N_element038]
  conduct = 2
  density = 1
  expand = 3
  formula = G4_PYRIDINE
  name = G4_PYRIDINE
  specific = 4
FEATURE [App::DocumentObjectGroupPython] H_element092  label="H_element : 0.144"  # scripted group (container) (typed FeaturePython)
  n = 0.143711
FEATURE [App::DocumentObjectGroupPython] C_element100  label="C_element : 0.856"  # scripted group (container) (typed FeaturePython)
  n = 0.856289
FEATURE [App::DocumentObjectGroupPython] G4_RUBBER_BUTYL  # scripted group (container) (typed FeaturePython)
  Dunit = g/cm3
  Dvalue = 0.92
  Group = -> [H_element092,C_element100]
  conduct = 2
  density = 1
  expand = 3
  formula = G4_RUBBER_BUTYL
  name = G4_RUBBER_BUTYL
  specific = 4
FEATURE [App::DocumentObjectGroupPython] H_element093  label="H_element : 0.118"  # scripted group (container) (typed FeaturePython)
  n = 0.118371
FEATURE [App::DocumentObjectGroupPython] C_element101  label="C_element : 0.882"  # scripted group (container) (typed FeaturePython)
  n = 0.881629
FEATURE [App::DocumentObjectGroupPython] G4_RUBBER_NATURAL  # scripted group (container) (typed FeaturePython)
  Dunit = g/cm3
  Dvalue = 0.92
  Group = -> [H_element093,C_element101]
  conduct = 2
  density = 1
  expand = 3
  formula = G4_RUBBER_NATURAL
  name = G4_RUBBER_NATURAL
  specific = 4
FEATURE [App::DocumentObjectGroupPython] H_element094  label="H_element : 0.145"  # scripted group (container) (typed FeaturePython)
  n = 0.05692
FEATURE [App::DocumentObjectGroupPython] C_element102  label="C_element : 0.543"  # scripted group (container) (typed FeaturePython)
  n = 0.542646
FEATURE [App::DocumentObjectGroupPython] Cl_element021  label="Cl_element : 0.400"  # scripted group (container) (typed FeaturePython)
  n = 0.400434
FEATURE [App::DocumentObjectGroupPython] G4_RUBBER_NEOPRENE  # scripted group (container) (typed FeaturePython)
  Dunit = g/cm3
  Dvalue = 1.23
  Group = -> [H_element094,C_element102,Cl_element021]
  conduct = 2
  density = 1
  expand = 3
  formula = G4_RUBBER_NEOPRENE
  name = G4_RUBBER_NEOPRENE
  specific = 4
FEATURE [App::DocumentObjectGroupPython] Si_element006  label="Si_element : 1"  # scripted group (container) (typed FeaturePython)
  n = 1
  ref = Si_element
FEATURE [App::DocumentObjectGroupPython] O_element087  label="O_element : 048"  # scripted group (container) (typed FeaturePython)
  n = 2
  ref = O_element
FEATURE [App::DocumentObjectGroupPython] G4_SILICON_DIOXIDE  # scripted group (container) (typed FeaturePython)
  Dunit = g/cm3
  Dvalue = 2.32
  Group = -> [Si_element006,O_element087]
  conduct = 2
  density = 1
  expand = 3
  formula = G4_SILICON_DIOXIDE
  name = G4_SILICON_DIOXIDE
  specific = 4
FEATURE [App::DocumentObjectGroupPython] Ag_element002  label="Ag_element : 1"  # scripted group (container) (typed FeaturePython)
  n = 1
  ref = Ag_element
FEATURE [App::DocumentObjectGroupPython] Br_element005  label="Br_element : 003"  # scripted group (container) (typed FeaturePython)
  n = 1
  ref = Br_element
FEATURE [App::DocumentObjectGroupPython] G4_SILVER_BROMIDE  # scripted group (container) (typed FeaturePython)
  Dunit = g/cm3
  Dvalue = 6.473
  Group = -> [Ag_element002,Br_element005]
  conduct = 2
  density = 1
  expand = 3
  formula = G4_SILVER_BROMIDE
  name = G4_SILVER_BROMIDE
  specific = 4
FEATURE [App::DocumentObjectGroupPython] Ag_element003  label="Ag_element : 002"  # scripted group (container) (typed FeaturePython)
  n = 1
  ref = Ag_element
FEATURE [App::DocumentObjectGroupPython] Cl_element022  label="Cl_element : 011"  # scripted group (container) (typed FeaturePython)
  n = 1
  ref = Cl_element
FEATURE [App::DocumentObjectGroupPython] G4_SILVER_CHLORIDE  # scripted group (container) (typed FeaturePython)
  Dunit = g/cm3
  Dvalue = 5.56
  Group = -> [Ag_element003,Cl_element022]
  conduct = 2
  density = 1
  expand = 3
  formula = G4_SILVER_CHLORIDE
  name = G4_SILVER_CHLORIDE
  specific = 4
FEATURE [App::DocumentObjectGroupPython] Br_element006  label="Br_element : 0.423"  # scripted group (container) (typed FeaturePython)
  n = 0.422895
FEATURE [App::DocumentObjectGroupPython] Ag_element004  label="Ag_element : 0.574"  # scripted group (container) (typed FeaturePython)
  n = 0.573748
FEATURE [App::DocumentObjectGroupPython] I_element007  label="I_element : 0.649"  # scripted group (container) (typed FeaturePython)
  n = 0.003357
FEATURE [App::DocumentObjectGroupPython] G4_SILVER_HALIDES  # scripted group (container) (typed FeaturePython)
  Dunit = g/cm3
  Dvalue = 6.47
  Group = -> [Br_element006,Ag_element004,I_element007]
  conduct = 2
  density = 1
  expand = 3
  formula = G4_SILVER_HALIDES
  name = G4_SILVER_HALIDES
  specific = 4
FEATURE [App::DocumentObjectGroupPython] Ag_element005  label="Ag_element : 003"  # scripted group (container) (typed FeaturePython)
  n = 1
  ref = Ag_element
FEATURE [App::DocumentObjectGroupPython] I_element008  label="I_element : 004"  # scripted group (container) (typed FeaturePython)
  n = 1
  ref = I_element
FEATURE [App::DocumentObjectGroupPython] G4_SILVER_IODIDE  # scripted group (container) (typed FeaturePython)
  Dunit = g/cm3
  Dvalue = 6.01
  Group = -> [Ag_element005,I_element008]
  conduct = 2
  density = 1
  expand = 3
  formula = G4_SILVER_IODIDE
  name = G4_SILVER_IODIDE
  specific = 4
FEATURE [App::DocumentObjectGroupPython] H_element095  label="H_element : 0.100"  # scripted group (container) (typed FeaturePython)
  n = 0.1
FEATURE [App::DocumentObjectGroupPython] C_element103  label="C_element : 0.204"  # scripted group (container) (typed FeaturePython)
  n = 0.204
FEATURE [App::DocumentObjectGroupPython] N_element039  label="N_element : 0.759"  # scripted group (container) (typed FeaturePython)
  n = 0.042
FEATURE [App::DocumentObjectGroupPython] O_element088  label="O_element : 0.645"  # scripted group (container) (typed FeaturePython)
  n = 0.645
FEATURE [App::DocumentObjectGroupPython] Na_element013  label="Na_element : 0.100"  # scripted group (container) (typed FeaturePython)
  n = 0.002
FEATURE [App::DocumentObjectGroupPython] P_element009  label="P_element : 0.107"  # scripted group (container) (typed FeaturePython)
  n = 0.001
FEATURE [App::DocumentObjectGroupPython] S_element020  label="S_element : 0.021"  # scripted group (container) (typed FeaturePython)
  n = 0.002
FEATURE [App::DocumentObjectGroupPython] Cl_element023  label="Cl_element : 0.590"  # scripted group (container) (typed FeaturePython)
  n = 0.003
FEATURE [App::DocumentObjectGroupPython] K_element010  label="K_element : 0.001"  # scripted group (container) (typed FeaturePython)
  n = 0.001
FEATURE [App::DocumentObjectGroupPython] G4_SKIN_ICRP  # scripted group (container) (typed FeaturePython)
  Dunit = g/cm3
  Dvalue = 1.09
  Group = -> [H_element095,C_element103,N_element039,O_element088,Na_element013,P_element009,S_element020,Cl_element023,K_element010]
  conduct = 2
  density = 1
  expand = 3
  formula = G4_SKIN_ICRP
  name = G4_SKIN_ICRP
  specific = 4
FEATURE [App::DocumentObjectGroupPython] Na_element014  label="Na_element : 2"  # scripted group (container) (typed FeaturePython)
  n = 2
  ref = Na_element
FEATURE [App::DocumentObjectGroupPython] C_element104  label="C_element : 058"  # scripted group (container) (typed FeaturePython)
  n = 1
  ref = C_element
FEATURE [App::DocumentObjectGroupPython] O_element089  label="O_element : 049"  # scripted group (container) (typed FeaturePython)
  n = 3
  ref = O_element
FEATURE [App::DocumentObjectGroupPython] G4_SODIUM_CARBONATE  # scripted group (container) (typed FeaturePython)
  Dunit = g/cm3
  Dvalue = 2.532
  Group = -> [Na_element014,C_element104,O_element089]
  conduct = 2
  density = 1
  expand = 3
  formula = G4_SODIUM_CARBONATE
  name = G4_SODIUM_CARBONATE
  specific = 4
FEATURE [App::DocumentObjectGroupPython] Na_element015  label="Na_element : 1"  # scripted group (container) (typed FeaturePython)
  n = 1
  ref = Na_element
FEATURE [App::DocumentObjectGroupPython] I_element009  label="I_element : 005"  # scripted group (container) (typed FeaturePython)
  n = 1
  ref = I_element
FEATURE [App::DocumentObjectGroupPython] G4_SODIUM_IODIDE  # scripted group (container) (typed FeaturePython)
  Dunit = g/cm3
  Dvalue = 3.667
  Group = -> [Na_element015,I_element009]
  conduct = 2
  density = 1
  expand = 3
  formula = G4_SODIUM_IODIDE
  name = G4_SODIUM_IODIDE
  specific = 4
FEATURE [App::DocumentObjectGroupPython] Na_element016  label="Na_element : 003"  # scripted group (container) (typed FeaturePython)
  n = 2
  ref = Na_element
FEATURE [App::DocumentObjectGroupPython] O_element090  label="O_element : 050"  # scripted group (container) (typed FeaturePython)
  n = 1
  ref = O_element
FEATURE [App::DocumentObjectGroupPython] G4_SODIUM_MONOXIDE  # scripted group (container) (typed FeaturePython)
  Dunit = g/cm3
  Dvalue = 2.27
  Group = -> [Na_element016,O_element090]
  conduct = 2
  density = 1
  expand = 3
  formula = G4_SODIUM_MONOXIDE
  name = G4_SODIUM_MONOXIDE
  specific = 4
FEATURE [App::DocumentObjectGroupPython] Na_element017  label="Na_element : 004"  # scripted group (container) (typed FeaturePython)
  n = 1
  ref = Na_element
FEATURE [App::DocumentObjectGroupPython] N_element040  label="N_element : 018"  # scripted group (container) (typed FeaturePython)
  n = 1
  ref = N_element
FEATURE [App::DocumentObjectGroupPython] O_element091  label="O_element : 051"  # scripted group (container) (typed FeaturePython)
  n = 3
  ref = O_element
FEATURE [App::DocumentObjectGroupPython] G4_SODIUM_NITRATE  # scripted group (container) (typed FeaturePython)
  Dunit = g/cm3
  Dvalue = 2.261
  Group = -> [Na_element017,N_element040,O_element091]
  conduct = 2
  density = 1
  expand = 3
  formula = G4_SODIUM_NITRATE
  name = G4_SODIUM_NITRATE
  specific = 4
FEATURE [App::DocumentObjectGroupPython] C_element105  label="C_element : 059"  # scripted group (container) (typed FeaturePython)
  n = 14
  ref = C_element
FEATURE [App::DocumentObjectGroupPython] H_element096  label="H_element : 053"  # scripted group (container) (typed FeaturePython)
  n = 12
  ref = H_element
FEATURE [App::DocumentObjectGroupPython] G4_STILBENE  # scripted group (container) (typed FeaturePython)
  Dunit = g/cm3
  Dvalue = 0.9707
  Group = -> [C_element105,H_element096]
  conduct = 2
  density = 1
  expand = 3
  formula = G4_STILBENE
  name = G4_STILBENE
  specific = 4
FEATURE [App::DocumentObjectGroupPython] C_element106  label="C_element : 12"  # scripted group (container) (typed FeaturePython)
  n = 12
  ref = C_element
FEATURE [App::DocumentObjectGroupPython] H_element097  label="H_element : 22"  # scripted group (container) (typed FeaturePython)
  n = 22
  ref = H_element
FEATURE [App::DocumentObjectGroupPython] O_element092  label="O_element : 11"  # scripted group (container) (typed FeaturePython)
  n = 11
  ref = O_element
FEATURE [App::DocumentObjectGroupPython] G4_SUCROSE  # scripted group (container) (typed FeaturePython)
  Dunit = g/cm3
  Dvalue = 1.5805
  Group = -> [C_element106,H_element097,O_element092]
  conduct = 2
  density = 1
  expand = 3
  formula = G4_SUCROSE
  name = G4_SUCROSE
  specific = 4
FEATURE [App::DocumentObjectGroupPython] C_element107  label="C_element : 18"  # scripted group (container) (typed FeaturePython)
  n = 18
  ref = C_element
FEATURE [App::DocumentObjectGroupPython] H_element098  label="H_element : 054"  # scripted group (container) (typed FeaturePython)
  n = 14
  ref = H_element
FEATURE [App::DocumentObjectGroupPython] G4_TERPHENYL  # scripted group (container) (typed FeaturePython)
  Dunit = g/cm3
  Dvalue = 1.24
  Group = -> [C_element107,H_element098]
  conduct = 2
  density = 1
  expand = 3
  formula = G4_TERPHENYL
  name = G4_TERPHENYL
  specific = 4
FEATURE [App::DocumentObjectGroupPython] H_element099  label="H_element : 0.146"  # scripted group (container) (typed FeaturePython)
  n = 0.106
FEATURE [App::DocumentObjectGroupPython] C_element108  label="C_element : 0.883"  # scripted group (container) (typed FeaturePython)
  n = 0.099
FEATURE [App::DocumentObjectGroupPython] N_element041  label="N_element : 0.020"  # scripted group (container) (typed FeaturePython)
  n = 0.02
FEATURE [App::DocumentObjectGroupPython] O_element093  label="O_element : 0.766"  # scripted group (container) (typed FeaturePython)
  n = 0.766
FEATURE [App::DocumentObjectGroupPython] Na_element018  label="Na_element : 0.101"  # scripted group (container) (typed FeaturePython)
  n = 0.002
FEATURE [App::DocumentObjectGroupPython] P_element010  label="P_element : 0.108"  # scripted group (container) (typed FeaturePython)
  n = 0.001
FEATURE [App::DocumentObjectGroupPython] S_element021  label="S_element : 0.022"  # scripted group (container) (typed FeaturePython)
  n = 0.002
FEATURE [App::DocumentObjectGroupPython] Cl_element024  label="Cl_element : 0.002"  # scripted group (container) (typed FeaturePython)
  n = 0.002
FEATURE [App::DocumentObjectGroupPython] K_element011  label="K_element : 0.017"  # scripted group (container) (typed FeaturePython)
  n = 0.002
FEATURE [App::DocumentObjectGroupPython] G4_TESTIS_ICRP  # scripted group (container) (typed FeaturePython)
  Dunit = g/cm3
  Dvalue = 1.04
  Group = -> [H_element099,C_element108,N_element041,O_element093,Na_element018,P_element010,S_element021,Cl_element024,K_element011]
  conduct = 2
  density = 1
  expand = 3
  formula = G4_TESTIS_ICRP
  name = G4_TESTIS_ICRP
  specific = 4
FEATURE [App::DocumentObjectGroupPython] C_element109  label="C_element : 060"  # scripted group (container) (typed FeaturePython)
  n = 2
  ref = C_element
FEATURE [App::DocumentObjectGroupPython] Cl_element025  label="Cl_element : 012"  # scripted group (container) (typed FeaturePython)
  n = 4
  ref = Cl_element
FEATURE [App::DocumentObjectGroupPython] G4_TETRACHLOROETHYLENE  # scripted group (container) (typed FeaturePython)
  Dunit = g/cm3
  Dvalue = 1.625
  Group = -> [C_element109,Cl_element025]
  conduct = 2
  density = 1
  expand = 3
  formula = G4_TETRACHLOROETHYLENE
  name = G4_TETRACHLOROETHYLENE
  specific = 4
FEATURE [App::DocumentObjectGroupPython] Tl_element001  label="Tl_element : 1"  # scripted group (container) (typed FeaturePython)
  n = 1
  ref = Tl_element
FEATURE [App::DocumentObjectGroupPython] Cl_element026  label="Cl_element : 013"  # scripted group (container) (typed FeaturePython)
  n = 1
  ref = Cl_element
FEATURE [App::DocumentObjectGroupPython] G4_THALLIUM_CHLORIDE  # scripted group (container) (typed FeaturePython)
  Dunit = g/cm3
  Dvalue = 7.004
  Group = -> [Tl_element001,Cl_element026]
  conduct = 2
  density = 1
  expand = 3
  formula = G4_THALLIUM_CHLORIDE
  name = G4_THALLIUM_CHLORIDE
  specific = 4
FEATURE [App::DocumentObjectGroupPython] H_element100  label="H_element : 0.147"  # scripted group (container) (typed FeaturePython)
  n = 0.105
FEATURE [App::DocumentObjectGroupPython] C_element110  label="C_element : 0.256"  # scripted group (container) (typed FeaturePython)
  n = 0.256
FEATURE [App::DocumentObjectGroupPython] N_element042  label="N_element : 0.760"  # scripted group (container) (typed FeaturePython)
  n = 0.027
FEATURE [App::DocumentObjectGroupPython] O_element094  label="O_element : 0.602"  # scripted group (container) (typed FeaturePython)
  n = 0.602
FEATURE [App::DocumentObjectGroupPython] Na_element019  label="Na_element : 0.102"  # scripted group (container) (typed FeaturePython)
  n = 0.001
FEATURE [App::DocumentObjectGroupPython] P_element011  label="P_element : 0.109"  # scripted group (container) (typed FeaturePython)
  n = 0.002
FEATURE [App::DocumentObjectGroupPython] S_element022  label="S_element : 0.023"  # scripted group (container) (typed FeaturePython)
  n = 0.003
FEATURE [App::DocumentObjectGroupPython] Cl_element027  label="Cl_element : 0.591"  # scripted group (container) (typed FeaturePython)
  n = 0.002
FEATURE [App::DocumentObjectGroupPython] K_element012  label="K_element : 0.018"  # scripted group (container) (typed FeaturePython)
  n = 0.002
FEATURE [App::DocumentObjectGroupPython] G4_TISSUE_SOFT_ICRP  # scripted group (container) (typed FeaturePython)
  Dunit = g/cm3
  Dvalue = 1.03
  Group = -> [H_element100,C_element110,N_element042,O_element094,Na_element019,P_element011,S_element022,Cl_element027,K_element012]
  conduct = 2
  density = 1
  expand = 3
  formula = G4_TISSUE_SOFT_ICRP
  name = G4_TISSUE_SOFT_ICRP
  specific = 4
FEATURE [App::DocumentObjectGroupPython] H_element101  label="H_element : 0.148"  # scripted group (container) (typed FeaturePython)
  n = 0.101
FEATURE [App::DocumentObjectGroupPython] C_element111  label="C_element : 0.111"  # scripted group (container) (typed FeaturePython)
  n = 0.111
FEATURE [App::DocumentObjectGroupPython] N_element043  label="N_element : 0.026"  # scripted group (container) (typed FeaturePython)
  n = 0.026
FEATURE [App::DocumentObjectGroupPython] O_element095  label="O_element : 0.762"  # scripted group (container) (typed FeaturePython)
  n = 0.762
FEATURE [App::DocumentObjectGroupPython] G4_TISSUE_SOFT_ICRU_4  label="G4_TISSUE_SOFT_ICRU-4"  # scripted group (container) (typed FeaturePython)
  Dunit = g/cm3
  Dvalue = 1
  Group = -> [H_element101,C_element111,N_element043,O_element095]
  conduct = 2
  density = 1
  expand = 3
  formula = G4_TISSUE_SOFT_ICRU-4
  name = G4_TISSUE_SOFT_ICRU-4
  specific = 4
FEATURE [App::DocumentObjectGroupPython] H_element102  label="H_element : 0.149"  # scripted group (container) (typed FeaturePython)
  n = 0.101869
FEATURE [App::DocumentObjectGroupPython] C_element112  label="C_element : 0.456"  # scripted group (container) (typed FeaturePython)
  n = 0.456179
FEATURE [App::DocumentObjectGroupPython] N_element044  label="N_element : 0.761"  # scripted group (container) (typed FeaturePython)
  n = 0.035172
FEATURE [App::DocumentObjectGroupPython] O_element096  label="O_element : 0.407"  # scripted group (container) (typed FeaturePython)
  n = 0.40678
FEATURE [App::DocumentObjectGroupPython] G4_TISSUE_METHANE  label="G4_TISSUE-METHANE"  # scripted group (container) (typed FeaturePython)
  Dunit = g/cm3
  Dvalue = 0.00106409
  Group = -> [H_element102,C_element112,N_element044,O_element096]
  conduct = 2
  density = 1
  expand = 3
  formula = G4_TISSUE-METHANE
  name = G4_TISSUE-METHANE
  specific = 4
FEATURE [App::DocumentObjectGroupPython] H_element103  label="H_element : 0.103"  # scripted group (container) (typed FeaturePython)
  n = 0.102672
FEATURE [App::DocumentObjectGroupPython] C_element113  label="C_element : 0.569"  # scripted group (container) (typed FeaturePython)
  n = 0.56894
FEATURE [App::DocumentObjectGroupPython] N_element045  label="N_element : 0.762"  # scripted group (container) (typed FeaturePython)
  n = 0.035022
FEATURE [App::DocumentObjectGroupPython] O_element097  label="O_element : 0.293"  # scripted group (container) (typed FeaturePython)
  n = 0.293366
FEATURE [App::DocumentObjectGroupPython] G4_TISSUE_PROPANE  label="G4_TISSUE-PROPANE"  # scripted group (container) (typed FeaturePython)
  Dunit = g/cm3
  Dvalue = 0.00182628
  Group = -> [H_element103,C_element113,N_element045,O_element097]
  conduct = 2
  density = 1
  expand = 3
  formula = G4_TISSUE-PROPANE
  name = G4_TISSUE-PROPANE
  specific = 4
FEATURE [App::DocumentObjectGroupPython] Ti_element003  label="Ti_element : 1"  # scripted group (container) (typed FeaturePython)
  n = 1
  ref = Ti_element
FEATURE [App::DocumentObjectGroupPython] O_element098  label="O_element : 052"  # scripted group (container) (typed FeaturePython)
  n = 2
  ref = O_element
FEATURE [App::DocumentObjectGroupPython] G4_TITANIUM_DIOXIDE  # scripted group (container) (typed FeaturePython)
  Dunit = g/cm3
  Dvalue = 4.26
  Group = -> [Ti_element003,O_element098]
  conduct = 2
  density = 1
  expand = 3
  formula = G4_TITANIUM_DIOXIDE
  name = G4_TITANIUM_DIOXIDE
  specific = 4
FEATURE [App::DocumentObjectGroupPython] C_element114  label="C_element : 061"  # scripted group (container) (typed FeaturePython)
  n = 7
  ref = C_element
FEATURE [App::DocumentObjectGroupPython] H_element104  label="H_element : 055"  # scripted group (container) (typed FeaturePython)
  n = 8
  ref = H_element
FEATURE [App::DocumentObjectGroupPython] G4_TOLUENE  # scripted group (container) (typed FeaturePython)
  Dunit = g/cm3
  Dvalue = 0.8669
  Group = -> [C_element114,H_element104]
  conduct = 2
  density = 1
  expand = 3
  formula = G4_TOLUENE
  name = G4_TOLUENE
  specific = 4
FEATURE [App::DocumentObjectGroupPython] C_element115  label="C_element : 062"  # scripted group (container) (typed FeaturePython)
  n = 2
  ref = C_element
FEATURE [App::DocumentObjectGroupPython] H_element105  label="H_element : 056"  # scripted group (container) (typed FeaturePython)
  n = 1
  ref = H_element
FEATURE [App::DocumentObjectGroupPython] Cl_element028  label="Cl_element : 014"  # scripted group (container) (typed FeaturePython)
  n = 3
  ref = Cl_element
FEATURE [App::DocumentObjectGroupPython] G4_TRICHLOROETHYLENE  # scripted group (container) (typed FeaturePython)
  Dunit = g/cm3
  Dvalue = 1.46
  Group = -> [C_element115,H_element105,Cl_element028]
  conduct = 2
  density = 1
  expand = 3
  formula = G4_TRICHLOROETHYLENE
  name = G4_TRICHLOROETHYLENE
  specific = 4
FEATURE [App::DocumentObjectGroupPython] C_element116  label="C_element : 063"  # scripted group (container) (typed FeaturePython)
  n = 6
  ref = C_element
FEATURE [App::DocumentObjectGroupPython] H_element106  label="H_element : 15"  # scripted group (container) (typed FeaturePython)
  n = 15
  ref = H_element
FEATURE [App::DocumentObjectGroupPython] O_element099  label="O_element : 053"  # scripted group (container) (typed FeaturePython)
  n = 4
  ref = O_element
FEATURE [App::DocumentObjectGroupPython] P_element012  label="P_element : 1"  # scripted group (container) (typed FeaturePython)
  n = 1
  ref = P_element
FEATURE [App::DocumentObjectGroupPython] G4_TRIETHYL_PHOSPHATE  # scripted group (container) (typed FeaturePython)
  Dunit = g/cm3
  Dvalue = 1.07
  Group = -> [C_element116,H_element106,O_element099,P_element012]
  conduct = 2
  density = 1
  expand = 3
  formula = G4_TRIETHYL_PHOSPHATE
  name = G4_TRIETHYL_PHOSPHATE
  specific = 4
FEATURE [App::DocumentObjectGroupPython] W_element003  label="W_element : 003"  # scripted group (container) (typed FeaturePython)
  n = 1
  ref = W_element
FEATURE [App::DocumentObjectGroupPython] F_element017  label="F_element : 6"  # scripted group (container) (typed FeaturePython)
  n = 6
  ref = F_element
FEATURE [App::DocumentObjectGroupPython] G4_TUNGSTEN_HEXAFLUORIDE  # scripted group (container) (typed FeaturePython)
  Dunit = g/cm3
  Dvalue = 2.4
  Group = -> [W_element003,F_element017]
  conduct = 2
  density = 1
  expand = 3
  formula = G4_TUNGSTEN_HEXAFLUORIDE
  name = G4_TUNGSTEN_HEXAFLUORIDE
  specific = 4
FEATURE [App::DocumentObjectGroupPython] U_element001  label="U_element : 1"  # scripted group (container) (typed FeaturePython)
  n = 1
  ref = U_element
FEATURE [App::DocumentObjectGroupPython] C_element117  label="C_element : 064"  # scripted group (container) (typed FeaturePython)
  n = 2
  ref = C_element
FEATURE [App::DocumentObjectGroupPython] G4_URANIUM_DICARBIDE  # scripted group (container) (typed FeaturePython)
  Dunit = g/cm3
  Dvalue = 11.28
  Group = -> [U_element001,C_element117]
  conduct = 2
  density = 1
  expand = 3
  formula = G4_URANIUM_DICARBIDE
  name = G4_URANIUM_DICARBIDE
  specific = 4
FEATURE [App::DocumentObjectGroupPython] U_element002  label="U_element : 002"  # scripted group (container) (typed FeaturePython)
  n = 1
  ref = U_element
FEATURE [App::DocumentObjectGroupPython] C_element118  label="C_element : 065"  # scripted group (container) (typed FeaturePython)
  n = 1
  ref = C_element
FEATURE [App::DocumentObjectGroupPython] G4_URANIUM_MONOCARBIDE  # scripted group (container) (typed FeaturePython)
  Dunit = g/cm3
  Dvalue = 13.63
  Group = -> [U_element002,C_element118]
  conduct = 2
  density = 1
  expand = 3
  formula = G4_URANIUM_MONOCARBIDE
  name = G4_URANIUM_MONOCARBIDE
  specific = 4
FEATURE [App::DocumentObjectGroupPython] U_element003  label="U_element : 003"  # scripted group (container) (typed FeaturePython)
  n = 1
  ref = U_element
FEATURE [App::DocumentObjectGroupPython] O_element100  label="O_element : 054"  # scripted group (container) (typed FeaturePython)
  n = 2
  ref = O_element
FEATURE [App::DocumentObjectGroupPython] G4_URANIUM_OXIDE  # scripted group (container) (typed FeaturePython)
  Dunit = g/cm3
  Dvalue = 10.96
  Group = -> [U_element003,O_element100]
  conduct = 2
  density = 1
  expand = 3
  formula = G4_URANIUM_OXIDE
  name = G4_URANIUM_OXIDE
  specific = 4
FEATURE [App::DocumentObjectGroupPython] C_element119  label="C_element : 066"  # scripted group (container) (typed FeaturePython)
  n = 1
  ref = C_element
FEATURE [App::DocumentObjectGroupPython] H_element107  label="H_element : 057"  # scripted group (container) (typed FeaturePython)
  n = 4
  ref = H_element
FEATURE [App::DocumentObjectGroupPython] N_element046  label="N_element : 019"  # scripted group (container) (typed FeaturePython)
  n = 2
  ref = N_element
FEATURE [App::DocumentObjectGroupPython] O_element101  label="O_element : 055"  # scripted group (container) (typed FeaturePython)
  n = 1
  ref = O_element
FEATURE [App::DocumentObjectGroupPython] G4_UREA  # scripted group (container) (typed FeaturePython)
  Dunit = g/cm3
  Dvalue = 1.323
  Group = -> [C_element119,H_element107,N_element046,O_element101]
  conduct = 2
  density = 1
  expand = 3
  formula = G4_UREA
  name = G4_UREA
  specific = 4
FEATURE [App::DocumentObjectGroupPython] C_element120  label="C_element : 067"  # scripted group (container) (typed FeaturePython)
  n = 5
  ref = C_element
FEATURE [App::DocumentObjectGroupPython] H_element108  label="H_element : 058"  # scripted group (container) (typed FeaturePython)
  n = 11
  ref = H_element
FEATURE [App::DocumentObjectGroupPython] N_element047  label="N_element : 020"  # scripted group (container) (typed FeaturePython)
  n = 1
  ref = N_element
FEATURE [App::DocumentObjectGroupPython] O_element102  label="O_element : 056"  # scripted group (container) (typed FeaturePython)
  n = 2
  ref = O_element
FEATURE [App::DocumentObjectGroupPython] G4_VALINE  # scripted group (container) (typed FeaturePython)
  Dunit = g/cm3
  Dvalue = 1.23
  Group = -> [C_element120,H_element108,N_element047,O_element102]
  conduct = 2
  density = 1
  expand = 3
  formula = G4_VALINE
  name = G4_VALINE
  specific = 4
FEATURE [App::DocumentObjectGroupPython] H_element109  label="H_element : 0.009"  # scripted group (container) (typed FeaturePython)
  n = 0.009417
FEATURE [App::DocumentObjectGroupPython] C_element121  label="C_element : 0.281"  # scripted group (container) (typed FeaturePython)
  n = 0.280555
FEATURE [App::DocumentObjectGroupPython] F_element018  label="F_element : 0.710"  # scripted group (container) (typed FeaturePython)
  n = 0.710028
FEATURE [App::DocumentObjectGroupPython] G4_VITON  # scripted group (container) (typed FeaturePython)
  Dunit = g/cm3
  Dvalue = 1.8
  Group = -> [H_element109,C_element121,F_element018]
  conduct = 2
  density = 1
  expand = 3
  formula = G4_VITON
  name = G4_VITON
  specific = 4
FEATURE [App::DocumentObjectGroupPython] H_element110  label="H_element : 059"  # scripted group (container) (typed FeaturePython)
  n = 2
  ref = H_element
FEATURE [App::DocumentObjectGroupPython] O_element103  label="O_element : 057"  # scripted group (container) (typed FeaturePython)
  n = 1
  ref = O_element
FEATURE [App::DocumentObjectGroupPython] G4_WATER  # scripted group (container) (typed FeaturePython)
  Dunit = g/cm3
  Dvalue = 1
  Group = -> [H_element110,O_element103]
  conduct = 2
  density = 1
  expand = 3
  formula = G4_WATER
  name = G4_WATER
  specific = 4
FEATURE [App::DocumentObjectGroupPython] H_element111  label="H_element : 060"  # scripted group (container) (typed FeaturePython)
  n = 2
  ref = H_element
FEATURE [App::DocumentObjectGroupPython] O_element104  label="O_element : 058"  # scripted group (container) (typed FeaturePython)
  n = 1
  ref = O_element
FEATURE [App::DocumentObjectGroupPython] G4_WATER_VAPOR  # scripted group (container) (typed FeaturePython)
  Dunit = g/cm3
  Dvalue = 0.000756182
  Group = -> [H_element111,O_element104]
  conduct = 2
  density = 1
  expand = 3
  formula = G4_WATER_VAPOR
  name = G4_WATER_VAPOR
  specific = 4
FEATURE [App::DocumentObjectGroupPython] C_element122  label="C_element : 068"  # scripted group (container) (typed FeaturePython)
  n = 8
  ref = C_element
FEATURE [App::DocumentObjectGroupPython] H_element112  label="H_element : 061"  # scripted group (container) (typed FeaturePython)
  n = 10
  ref = H_element
FEATURE [App::DocumentObjectGroupPython] G4_XYLENE  # scripted group (container) (typed FeaturePython)
  Dunit = g/cm3
  Dvalue = 0.87
  Group = -> [C_element122,H_element112]
  conduct = 2
  density = 1
  expand = 3
  formula = G4_XYLENE
  name = G4_XYLENE
  specific = 4
FEATURE [App::DocumentObjectGroupPython] C_element123  label="C_element : 069"  # scripted group (container) (typed FeaturePython)
  n = 1
  ref = C_element
FEATURE [App::DocumentObjectGroupPython] G4_GRAPHITE  # scripted group (container) (typed FeaturePython)
  Dunit = g/cm3
  Dvalue = 2.21
  Group = -> [C_element123]
  conduct = 2
  density = 1
  expand = 3
  formula = G4_GRAPHITE
  name = G4_GRAPHITE
  specific = 4
FEATURE [App::DocumentObjectGroupPython] NIST  # scripted group (container) (typed FeaturePython)
  Group = -> [G4_A_150_TISSUE,G4_ACETONE,G4_ACETYLENE,G4_ADENINE,G4_ADIPOSE_TISSUE_ICRP,G4_AIR,G4_ALANINE,G4_ALUMINUM_OXIDE,G4_AMBER,G4_AMMONIA,G4_ANILINE,G4_ANTHRACENE,G4_B_100_BONE,G4_BAKELITE,G4_BARIUM_FLUORIDE,G4_BARIUM_SULFATE,G4_BENZENE,G4_BERYLLIUM_OXIDE,G4_BGO,G4_BLOOD_ICRP,G4_BONE_COMPACT_ICRU,G4_BONE_CORTICAL_ICRP,G4_BORON_CARBIDE,G4_BORON_OXIDE,G4_BRAIN_ICRP,G4_BUTANE,G4_N_BUTYL_ALCOHOL,G4_C_552,+152 more]
FEATURE [App::DocumentObjectGroupPython] H_element113  label="H_element : 062"  # scripted group (container) (typed FeaturePython)
  n = 1
  ref = H_element
FEATURE [App::DocumentObjectGroupPython] G4_H  # scripted group (container) (typed FeaturePython)
  Dunit = g/cm3
  Dvalue = 8.3748e-05
  Group = -> [H_element113]
  conduct = 2
  density = 1
  expand = 3
  formula = H
  name = G4_H
  specific = 4
FEATURE [App::DocumentObjectGroupPython] He_element001  label="He_element : 1"  # scripted group (container) (typed FeaturePython)
  n = 1
  ref = He_element
FEATURE [App::DocumentObjectGroupPython] G4_He  # scripted group (container) (typed FeaturePython)
  Dunit = g/cm3
  Dvalue = 0.000166322
  Group = -> [He_element001]
  conduct = 2
  density = 1
  expand = 3
  formula = He
  name = G4_He
  specific = 4
FEATURE [App::DocumentObjectGroupPython] Li_element008  label="Li_element : 008"  # scripted group (container) (typed FeaturePython)
  n = 1
  ref = Li_element
FEATURE [App::DocumentObjectGroupPython] G4_Li  # scripted group (container) (typed FeaturePython)
  Dunit = g/cm3
  Dvalue = 0.534
  Group = -> [Li_element008]
  conduct = 2
  density = 1
  expand = 3
  formula = Li
  name = G4_Li
  specific = 4
FEATURE [App::DocumentObjectGroupPython] Be_element002  label="Be_element : 002"  # scripted group (container) (typed FeaturePython)
  n = 1
  ref = Be_element
FEATURE [App::DocumentObjectGroupPython] G4_Be  # scripted group (container) (typed FeaturePython)
  Dunit = g/cm3
  Dvalue = 1.848
  Group = -> [Be_element002]
  conduct = 2
  density = 1
  expand = 3
  formula = Be
  name = G4_Be
  specific = 4
FEATURE [App::DocumentObjectGroupPython] B_element007  label="B_element : 007"  # scripted group (container) (typed FeaturePython)
  n = 1
  ref = B_element
FEATURE [App::DocumentObjectGroupPython] G4_B  # scripted group (container) (typed FeaturePython)
  Dunit = g/cm3
  Dvalue = 2.37
  Group = -> [B_element007]
  conduct = 2
  density = 1
  expand = 3
  formula = B
  name = G4_B
  specific = 4
FEATURE [App::DocumentObjectGroupPython] C_element124  label="C_element : 070"  # scripted group (container) (typed FeaturePython)
  n = 1
  ref = C_element
FEATURE [App::DocumentObjectGroupPython] G4_C  # scripted group (container) (typed FeaturePython)
  Dunit = g/cm3
  Dvalue = 2
  Group = -> [C_element124]
  conduct = 2
  density = 1
  expand = 3
  formula = C
  name = G4_C
  specific = 4
FEATURE [App::DocumentObjectGroupPython] N_element048  label="N_element : 021"  # scripted group (container) (typed FeaturePython)
  n = 1
  ref = N_element
FEATURE [App::DocumentObjectGroupPython] G4_N  # scripted group (container) (typed FeaturePython)
  Dunit = g/cm3
  Dvalue = 0.0011652
  Group = -> [N_element048]
  conduct = 2
  density = 1
  expand = 3
  formula = N
  name = G4_N
  specific = 4
FEATURE [App::DocumentObjectGroupPython] O_element105  label="O_element : 059"  # scripted group (container) (typed FeaturePython)
  n = 1
  ref = O_element
FEATURE [App::DocumentObjectGroupPython] G4_O  # scripted group (container) (typed FeaturePython)
  Dunit = g/cm3
  Dvalue = 0.00133151
  Group = -> [O_element105]
  conduct = 2
  density = 1
  expand = 3
  formula = O
  name = G4_O
  specific = 4
FEATURE [App::DocumentObjectGroupPython] F_element019  label="F_element : 008"  # scripted group (container) (typed FeaturePython)
  n = 1
  ref = F_element
FEATURE [App::DocumentObjectGroupPython] G4_F  # scripted group (container) (typed FeaturePython)
  Dunit = g/cm3
  Dvalue = 0.00158029
  Group = -> [F_element019]
  conduct = 2
  density = 1
  expand = 3
  formula = F
  name = G4_F
  specific = 4
FEATURE [App::DocumentObjectGroupPython] Ne_element001  label="Ne_element : 1"  # scripted group (container) (typed FeaturePython)
  n = 1
  ref = Ne_element
FEATURE [App::DocumentObjectGroupPython] G4_Ne  # scripted group (container) (typed FeaturePython)
  Dunit = g/cm3
  Dvalue = 0.000838505
  Group = -> [Ne_element001]
  conduct = 2
  density = 1
  expand = 3
  formula = Ne
  name = G4_Ne
  specific = 4
FEATURE [App::DocumentObjectGroupPython] Na_element020  label="Na_element : 005"  # scripted group (container) (typed FeaturePython)
  n = 1
  ref = Na_element
FEATURE [App::DocumentObjectGroupPython] G4_Na  # scripted group (container) (typed FeaturePython)
  Dunit = g/cm3
  Dvalue = 0.971
  Group = -> [Na_element020]
  conduct = 2
  density = 1
  expand = 3
  formula = Na
  name = G4_Na
  specific = 4
FEATURE [App::DocumentObjectGroupPython] Mg_element011  label="Mg_element : 005"  # scripted group (container) (typed FeaturePython)
  n = 1
  ref = Mg_element
FEATURE [App::DocumentObjectGroupPython] G4_Mg  # scripted group (container) (typed FeaturePython)
  Dunit = g/cm3
  Dvalue = 1.74
  Group = -> [Mg_element011]
  conduct = 2
  density = 1
  expand = 3
  formula = Mg
  name = G4_Mg
  specific = 4
FEATURE [App::DocumentObjectGroupPython] Al_element004  label="Al_element : 1"  # scripted group (container) (typed FeaturePython)
  n = 1
  ref = Al_element
FEATURE [App::DocumentObjectGroupPython] G4_Al  # scripted group (container) (typed FeaturePython)
  Dunit = g/cm3
  Dvalue = 2.699
  Group = -> [Al_element004]
  conduct = 2
  density = 1
  expand = 3
  formula = Al
  name = G4_Al
  specific = 4
FEATURE [App::DocumentObjectGroupPython] Si_element007  label="Si_element : 002"  # scripted group (container) (typed FeaturePython)
  n = 1
  ref = Si_element
FEATURE [App::DocumentObjectGroupPython] G4_Si  # scripted group (container) (typed FeaturePython)
  Dunit = g/cm3
  Dvalue = 2.33
  Group = -> [Si_element007]
  conduct = 2
  density = 1
  expand = 3
  formula = Si
  name = G4_Si
  specific = 4
FEATURE [App::DocumentObjectGroupPython] P_element013  label="P_element : 002"  # scripted group (container) (typed FeaturePython)
  n = 1
  ref = P_element
FEATURE [App::DocumentObjectGroupPython] G4_P  # scripted group (container) (typed FeaturePython)
  Dunit = g/cm3
  Dvalue = 2.2
  Group = -> [P_element013]
  conduct = 2
  density = 1
  expand = 3
  formula = P
  name = G4_P
  specific = 4
FEATURE [App::DocumentObjectGroupPython] S_element023  label="S_element : 007"  # scripted group (container) (typed FeaturePython)
  n = 1
  ref = S_element
FEATURE [App::DocumentObjectGroupPython] G4_S  # scripted group (container) (typed FeaturePython)
  Dunit = g/cm3
  Dvalue = 2
  Group = -> [S_element023]
  conduct = 2
  density = 1
  expand = 3
  formula = S
  name = G4_S
  specific = 4
FEATURE [App::DocumentObjectGroupPython] Cl_element029  label="Cl_element : 015"  # scripted group (container) (typed FeaturePython)
  n = 1
  ref = Cl_element
FEATURE [App::DocumentObjectGroupPython] G4_Cl  # scripted group (container) (typed FeaturePython)
  Dunit = g/cm3
  Dvalue = 0.00299473
  Group = -> [Cl_element029]
  conduct = 2
  density = 1
  expand = 3
  formula = Cl
  name = G4_Cl
  specific = 4
FEATURE [App::DocumentObjectGroupPython] Ar_element002  label="Ar_element : 1"  # scripted group (container) (typed FeaturePython)
  n = 1
  ref = Ar_element
FEATURE [App::DocumentObjectGroupPython] G4_Ar  # scripted group (container) (typed FeaturePython)
  Dunit = g/cm3
  Dvalue = 0.00166201
  Group = -> [Ar_element002]
  conduct = 2
  density = 1
  expand = 3
  formula = Ar
  name = G4_Ar
  specific = 4
FEATURE [App::DocumentObjectGroupPython] K_element013  label="K_element : 003"  # scripted group (container) (typed FeaturePython)
  n = 1
  ref = K_element
FEATURE [App::DocumentObjectGroupPython] G4_K  # scripted group (container) (typed FeaturePython)
  Dunit = g/cm3
  Dvalue = 0.862
  Group = -> [K_element013]
  conduct = 2
  density = 1
  expand = 3
  formula = K
  name = G4_K
  specific = 4
FEATURE [App::DocumentObjectGroupPython] Ca_element014  label="Ca_element : 007"  # scripted group (container) (typed FeaturePython)
  n = 1
  ref = Ca_element
FEATURE [App::DocumentObjectGroupPython] G4_Ca  # scripted group (container) (typed FeaturePython)
  Dunit = g/cm3
  Dvalue = 1.55
  Group = -> [Ca_element014]
  conduct = 2
  density = 1
  expand = 3
  formula = Ca
  name = G4_Ca
  specific = 4
FEATURE [App::DocumentObjectGroupPython] Sc_element001  label="Sc_element : 1"  # scripted group (container) (typed FeaturePython)
  n = 1
  ref = Sc_element
FEATURE [App::DocumentObjectGroupPython] G4_Sc  # scripted group (container) (typed FeaturePython)
  Dunit = g/cm3
  Dvalue = 2.989
  Group = -> [Sc_element001]
  conduct = 2
  density = 1
  expand = 3
  formula = Sc
  name = G4_Sc
  specific = 4
FEATURE [App::DocumentObjectGroupPython] Ti_element004  label="Ti_element : 002"  # scripted group (container) (typed FeaturePython)
  n = 1
  ref = Ti_element
FEATURE [App::DocumentObjectGroupPython] G4_Ti  # scripted group (container) (typed FeaturePython)
  Dunit = g/cm3
  Dvalue = 4.54
  Group = -> [Ti_element004]
  conduct = 2
  density = 1
  expand = 3
  formula = Ti
  name = G4_Ti
  specific = 4
FEATURE [App::DocumentObjectGroupPython] V_element001  label="V_element : 1"  # scripted group (container) (typed FeaturePython)
  n = 1
  ref = V_element
FEATURE [App::DocumentObjectGroupPython] G4_V  # scripted group (container) (typed FeaturePython)
  Dunit = g/cm3
  Dvalue = 6.11
  Group = -> [V_element001]
  conduct = 2
  density = 1
  expand = 3
  formula = V
  name = G4_V
  specific = 4
FEATURE [App::DocumentObjectGroupPython] Cr_element001  label="Cr_element : 1"  # scripted group (container) (typed FeaturePython)
  n = 1
  ref = Cr_element
FEATURE [App::DocumentObjectGroupPython] G4_Cr  # scripted group (container) (typed FeaturePython)
  Dunit = g/cm3
  Dvalue = 7.18
  Group = -> [Cr_element001]
  conduct = 2
  density = 1
  expand = 3
  formula = Cr
  name = G4_Cr
  specific = 4
FEATURE [App::DocumentObjectGroupPython] Mn_element001  label="Mn_element : 1"  # scripted group (container) (typed FeaturePython)
  n = 1
  ref = Mn_element
FEATURE [App::DocumentObjectGroupPython] G4_Mn  # scripted group (container) (typed FeaturePython)
  Dunit = g/cm3
  Dvalue = 7.44
  Group = -> [Mn_element001]
  conduct = 2
  density = 1
  expand = 3
  formula = Mn
  name = G4_Mn
  specific = 4
FEATURE [App::DocumentObjectGroupPython] Fe_element007  label="Fe_element : 004"  # scripted group (container) (typed FeaturePython)
  n = 1
  ref = Fe_element
FEATURE [App::DocumentObjectGroupPython] G4_Fe  # scripted group (container) (typed FeaturePython)
  Dunit = g/cm3
  Dvalue = 7.874
  Group = -> [Fe_element007]
  conduct = 2
  density = 1
  expand = 3
  formula = Fe
  name = G4_Fe
  specific = 4
FEATURE [App::DocumentObjectGroupPython] Co_element001  label="Co_element : 1"  # scripted group (container) (typed FeaturePython)
  n = 1
  ref = Co_element
FEATURE [App::DocumentObjectGroupPython] G4_Co  # scripted group (container) (typed FeaturePython)
  Dunit = g/cm3
  Dvalue = 8.9
  Group = -> [Co_element001]
  conduct = 2
  density = 1
  expand = 3
  formula = Co
  name = G4_Co
  specific = 4
FEATURE [App::DocumentObjectGroupPython] Ni_element001  label="Ni_element : 1"  # scripted group (container) (typed FeaturePython)
  n = 1
  ref = Ni_element
FEATURE [App::DocumentObjectGroupPython] G4_Ni  # scripted group (container) (typed FeaturePython)
  Dunit = g/cm3
  Dvalue = 8.902
  Group = -> [Ni_element001]
  conduct = 2
  density = 1
  expand = 3
  formula = Ni
  name = G4_Ni
  specific = 4
FEATURE [App::DocumentObjectGroupPython] Cu_element001  label="Cu_element : 1"  # scripted group (container) (typed FeaturePython)
  n = 1
  ref = Cu_element
FEATURE [App::DocumentObjectGroupPython] G4_Cu  # scripted group (container) (typed FeaturePython)
  Dunit = g/cm3
  Dvalue = 8.96
  Group = -> [Cu_element001]
  conduct = 2
  density = 1
  expand = 3
  formula = Cu
  name = G4_Cu
  specific = 4
FEATURE [App::DocumentObjectGroupPython] Zn_element001  label="Zn_element : 1"  # scripted group (container) (typed FeaturePython)
  n = 1
  ref = Zn_element
FEATURE [App::DocumentObjectGroupPython] G4_Zn  # scripted group (container) (typed FeaturePython)
  Dunit = g/cm3
  Dvalue = 7.133
  Group = -> [Zn_element001]
  conduct = 2
  density = 1
  expand = 3
  formula = Zn
  name = G4_Zn
  specific = 4
FEATURE [App::DocumentObjectGroupPython] Ga_element002  label="Ga_element : 002"  # scripted group (container) (typed FeaturePython)
  n = 1
  ref = Ga_element
FEATURE [App::DocumentObjectGroupPython] G4_Ga  # scripted group (container) (typed FeaturePython)
  Dunit = g/cm3
  Dvalue = 5.904
  Group = -> [Ga_element002]
  conduct = 2
  density = 1
  expand = 3
  formula = Ga
  name = G4_Ga
  specific = 4
FEATURE [App::DocumentObjectGroupPython] Ge_element002  label="Ge_element : 1"  # scripted group (container) (typed FeaturePython)
  n = 1
  ref = Ge_element
FEATURE [App::DocumentObjectGroupPython] G4_Ge  # scripted group (container) (typed FeaturePython)
  Dunit = g/cm3
  Dvalue = 5.323
  Group = -> [Ge_element002]
  conduct = 2
  density = 1
  expand = 3
  formula = Ge
  name = G4_Ge
  specific = 4
FEATURE [App::DocumentObjectGroupPython] As_element003  label="As_element : 002"  # scripted group (container) (typed FeaturePython)
  n = 1
  ref = As_element
FEATURE [App::DocumentObjectGroupPython] G4_As  # scripted group (container) (typed FeaturePython)
  Dunit = g/cm3
  Dvalue = 5.73
  Group = -> [As_element003]
  conduct = 2
  density = 1
  expand = 3
  formula = As
  name = G4_As
  specific = 4
FEATURE [App::DocumentObjectGroupPython] Se_element001  label="Se_element : 1"  # scripted group (container) (typed FeaturePython)
  n = 1
  ref = Se_element
FEATURE [App::DocumentObjectGroupPython] G4_Se  # scripted group (container) (typed FeaturePython)
  Dunit = g/cm3
  Dvalue = 4.5
  Group = -> [Se_element001]
  conduct = 2
  density = 1
  expand = 3
  formula = Se
  name = G4_Se
  specific = 4
FEATURE [App::DocumentObjectGroupPython] Br_element007  label="Br_element : 004"  # scripted group (container) (typed FeaturePython)
  n = 1
  ref = Br_element
FEATURE [App::DocumentObjectGroupPython] G4_Br  # scripted group (container) (typed FeaturePython)
  Dunit = g/cm3
  Dvalue = 0.0070721
  Group = -> [Br_element007]
  conduct = 2
  density = 1
  expand = 3
  formula = Br
  name = G4_Br
  specific = 4
FEATURE [App::DocumentObjectGroupPython] Kr_element001  label="Kr_element : 1"  # scripted group (container) (typed FeaturePython)
  n = 1
  ref = Kr_element
FEATURE [App::DocumentObjectGroupPython] G4_Kr  # scripted group (container) (typed FeaturePython)
  Dunit = g/cm3
  Dvalue = 0.00347832
  Group = -> [Kr_element001]
  conduct = 2
  density = 1
  expand = 3
  formula = Kr
  name = G4_Kr
  specific = 4
FEATURE [App::DocumentObjectGroupPython] Rb_element001  label="Rb_element : 1"  # scripted group (container) (typed FeaturePython)
  n = 1
  ref = Rb_element
FEATURE [App::DocumentObjectGroupPython] G4_Rb  # scripted group (container) (typed FeaturePython)
  Dunit = g/cm3
  Dvalue = 1.532
  Group = -> [Rb_element001]
  conduct = 2
  density = 1
  expand = 3
  formula = Rb
  name = G4_Rb
  specific = 4
FEATURE [App::DocumentObjectGroupPython] Sr_element001  label="Sr_element : 1"  # scripted group (container) (typed FeaturePython)
  n = 1
  ref = Sr_element
FEATURE [App::DocumentObjectGroupPython] G4_Sr  # scripted group (container) (typed FeaturePython)
  Dunit = g/cm3
  Dvalue = 2.54
  Group = -> [Sr_element001]
  conduct = 2
  density = 1
  expand = 3
  formula = Sr
  name = G4_Sr
  specific = 4
FEATURE [App::DocumentObjectGroupPython] Y_element001  label="Y_element : 1"  # scripted group (container) (typed FeaturePython)
  n = 1
  ref = Y_element
FEATURE [App::DocumentObjectGroupPython] G4_Y  # scripted group (container) (typed FeaturePython)
  Dunit = g/cm3
  Dvalue = 4.469
  Group = -> [Y_element001]
  conduct = 2
  density = 1
  expand = 3
  formula = Y
  name = G4_Y
  specific = 4
FEATURE [App::DocumentObjectGroupPython] Zr_element001  label="Zr_element : 1"  # scripted group (container) (typed FeaturePython)
  n = 1
  ref = Zr_element
FEATURE [App::DocumentObjectGroupPython] G4_Zr  # scripted group (container) (typed FeaturePython)
  Dunit = g/cm3
  Dvalue = 6.506
  Group = -> [Zr_element001]
  conduct = 2
  density = 1
  expand = 3
  formula = Zr
  name = G4_Zr
  specific = 4
FEATURE [App::DocumentObjectGroupPython] Nb_element001  label="Nb_element : 1"  # scripted group (container) (typed FeaturePython)
  n = 1
  ref = Nb_element
FEATURE [App::DocumentObjectGroupPython] G4_Nb  # scripted group (container) (typed FeaturePython)
  Dunit = g/cm3
  Dvalue = 8.57
  Group = -> [Nb_element001]
  conduct = 2
  density = 1
  expand = 3
  formula = Nb
  name = G4_Nb
  specific = 4
FEATURE [App::DocumentObjectGroupPython] Mo_element001  label="Mo_element : 1"  # scripted group (container) (typed FeaturePython)
  n = 1
  ref = Mo_element
FEATURE [App::DocumentObjectGroupPython] G4_Mo  # scripted group (container) (typed FeaturePython)
  Dunit = g/cm3
  Dvalue = 10.22
  Group = -> [Mo_element001]
  conduct = 2
  density = 1
  expand = 3
  formula = Mo
  name = G4_Mo
  specific = 4
FEATURE [App::DocumentObjectGroupPython] Tc_element001  label="Tc_element : 1"  # scripted group (container) (typed FeaturePython)
  n = 1
  ref = Tc_element
FEATURE [App::DocumentObjectGroupPython] G4_Tc  # scripted group (container) (typed FeaturePython)
  Dunit = g/cm3
  Dvalue = 11.5
  Group = -> [Tc_element001]
  conduct = 2
  density = 1
  expand = 3
  formula = Tc
  name = G4_Tc
  specific = 4
FEATURE [App::DocumentObjectGroupPython] Ru_element001  label="Ru_element : 1"  # scripted group (container) (typed FeaturePython)
  n = 1
  ref = Ru_element
FEATURE [App::DocumentObjectGroupPython] G4_Ru  # scripted group (container) (typed FeaturePython)
  Dunit = g/cm3
  Dvalue = 12.41
  Group = -> [Ru_element001]
  conduct = 2
  density = 1
  expand = 3
  formula = Ru
  name = G4_Ru
  specific = 4
FEATURE [App::DocumentObjectGroupPython] Rh_element001  label="Rh_element : 1"  # scripted group (container) (typed FeaturePython)
  n = 1
  ref = Rh_element
FEATURE [App::DocumentObjectGroupPython] G4_Rh  # scripted group (container) (typed FeaturePython)
  Dunit = g/cm3
  Dvalue = 12.41
  Group = -> [Rh_element001]
  conduct = 2
  density = 1
  expand = 3
  formula = Rh
  name = G4_Rh
  specific = 4
FEATURE [App::DocumentObjectGroupPython] Pd_element001  label="Pd_element : 1"  # scripted group (container) (typed FeaturePython)
  n = 1
  ref = Pd_element
FEATURE [App::DocumentObjectGroupPython] G4_Pd  # scripted group (container) (typed FeaturePython)
  Dunit = g/cm3
  Dvalue = 12.02
  Group = -> [Pd_element001]
  conduct = 2
  density = 1
  expand = 3
  formula = Pd
  name = G4_Pd
  specific = 4
FEATURE [App::DocumentObjectGroupPython] Ag_element006  label="Ag_element : 004"  # scripted group (container) (typed FeaturePython)
  n = 1
  ref = Ag_element
FEATURE [App::DocumentObjectGroupPython] G4_Ag  # scripted group (container) (typed FeaturePython)
  Dunit = g/cm3
  Dvalue = 10.5
  Group = -> [Ag_element006]
  conduct = 2
  density = 1
  expand = 3
  formula = Ag
  name = G4_Ag
  specific = 4
FEATURE [App::DocumentObjectGroupPython] Cd_element003  label="Cd_element : 003"  # scripted group (container) (typed FeaturePython)
  n = 1
  ref = Cd_element
FEATURE [App::DocumentObjectGroupPython] G4_Cd  # scripted group (container) (typed FeaturePython)
  Dunit = g/cm3
  Dvalue = 8.65
  Group = -> [Cd_element003]
  conduct = 2
  density = 1
  expand = 3
  formula = Cd
  name = G4_Cd
  specific = 4
FEATURE [App::DocumentObjectGroupPython] In_element001  label="In_element : 1"  # scripted group (container) (typed FeaturePython)
  n = 1
  ref = In_element
FEATURE [App::DocumentObjectGroupPython] G4_In  # scripted group (container) (typed FeaturePython)
  Dunit = g/cm3
  Dvalue = 7.31
  Group = -> [In_element001]
  conduct = 2
  density = 1
  expand = 3
  formula = In
  name = G4_In
  specific = 4
FEATURE [App::DocumentObjectGroupPython] Sn_element001  label="Sn_element : 1"  # scripted group (container) (typed FeaturePython)
  n = 1
  ref = Sn_element
FEATURE [App::DocumentObjectGroupPython] G4_Sn  # scripted group (container) (typed FeaturePython)
  Dunit = g/cm3
  Dvalue = 7.31
  Group = -> [Sn_element001]
  conduct = 2
  density = 1
  expand = 3
  formula = Sn
  name = G4_Sn
  specific = 4
FEATURE [App::DocumentObjectGroupPython] Sb_element001  label="Sb_element : 1"  # scripted group (container) (typed FeaturePython)
  n = 1
  ref = Sb_element
FEATURE [App::DocumentObjectGroupPython] G4_Sb  # scripted group (container) (typed FeaturePython)
  Dunit = g/cm3
  Dvalue = 6.691
  Group = -> [Sb_element001]
  conduct = 2
  density = 1
  expand = 3
  formula = Sb
  name = G4_Sb
  specific = 4
FEATURE [App::DocumentObjectGroupPython] Te_element002  label="Te_element : 002"  # scripted group (container) (typed FeaturePython)
  n = 1
  ref = Te_element
FEATURE [App::DocumentObjectGroupPython] G4_Te  # scripted group (container) (typed FeaturePython)
  Dunit = g/cm3
  Dvalue = 6.24
  Group = -> [Te_element002]
  conduct = 2
  density = 1
  expand = 3
  formula = Te
  name = G4_Te
  specific = 4
FEATURE [App::DocumentObjectGroupPython] I_element010  label="I_element : 006"  # scripted group (container) (typed FeaturePython)
  n = 1
  ref = I_element
FEATURE [App::DocumentObjectGroupPython] G4_I  # scripted group (container) (typed FeaturePython)
  Dunit = g/cm3
  Dvalue = 4.93
  Group = -> [I_element010]
  conduct = 2
  density = 1
  expand = 3
  formula = I
  name = G4_I
  specific = 4
FEATURE [App::DocumentObjectGroupPython] Xe_element001  label="Xe_element : 1"  # scripted group (container) (typed FeaturePython)
  n = 1
  ref = Xe_element
FEATURE [App::DocumentObjectGroupPython] G4_Xe  # scripted group (container) (typed FeaturePython)
  Dunit = g/cm3
  Dvalue = 0.00548536
  Group = -> [Xe_element001]
  conduct = 2
  density = 1
  expand = 3
  formula = Xe
  name = G4_Xe
  specific = 4
FEATURE [App::DocumentObjectGroupPython] Cs_element003  label="Cs_element : 003"  # scripted group (container) (typed FeaturePython)
  n = 1
  ref = Cs_element
FEATURE [App::DocumentObjectGroupPython] G4_Cs  # scripted group (container) (typed FeaturePython)
  Dunit = g/cm3
  Dvalue = 1.873
  Group = -> [Cs_element003]
  conduct = 2
  density = 1
  expand = 3
  formula = Cs
  name = G4_Cs
  specific = 4
FEATURE [App::DocumentObjectGroupPython] Ba_element003  label="Ba_element : 003"  # scripted group (container) (typed FeaturePython)
  n = 1
  ref = Ba_element
FEATURE [App::DocumentObjectGroupPython] G4_Ba  # scripted group (container) (typed FeaturePython)
  Dunit = g/cm3
  Dvalue = 3.5
  Group = -> [Ba_element003]
  conduct = 2
  density = 1
  expand = 3
  formula = Ba
  name = G4_Ba
  specific = 4
FEATURE [App::DocumentObjectGroupPython] La_element003  label="La_element : 003"  # scripted group (container) (typed FeaturePython)
  n = 1
  ref = La_element
FEATURE [App::DocumentObjectGroupPython] G4_La  # scripted group (container) (typed FeaturePython)
  Dunit = g/cm3
  Dvalue = 6.154
  Group = -> [La_element003]
  conduct = 2
  density = 1
  expand = 3
  formula = La
  name = G4_La
  specific = 4
FEATURE [App::DocumentObjectGroupPython] Ce_element002  label="Ce_element : 1"  # scripted group (container) (typed FeaturePython)
  n = 1
  ref = Ce_element
FEATURE [App::DocumentObjectGroupPython] G4_Ce  # scripted group (container) (typed FeaturePython)
  Dunit = g/cm3
  Dvalue = 6.657
  Group = -> [Ce_element002]
  conduct = 2
  density = 1
  expand = 3
  formula = Ce
  name = G4_Ce
  specific = 4
FEATURE [App::DocumentObjectGroupPython] Pr_element001  label="Pr_element : 1"  # scripted group (container) (typed FeaturePython)
  n = 1
  ref = Pr_element
FEATURE [App::DocumentObjectGroupPython] G4_Pr  # scripted group (container) (typed FeaturePython)
  Dunit = g/cm3
  Dvalue = 6.71
  Group = -> [Pr_element001]
  conduct = 2
  density = 1
  expand = 3
  formula = Pr
  name = G4_Pr
  specific = 4
FEATURE [App::DocumentObjectGroupPython] Nd_element001  label="Nd_element : 1"  # scripted group (container) (typed FeaturePython)
  n = 1
  ref = Nd_element
FEATURE [App::DocumentObjectGroupPython] G4_Nd  # scripted group (container) (typed FeaturePython)
  Dunit = g/cm3
  Dvalue = 6.9
  Group = -> [Nd_element001]
  conduct = 2
  density = 1
  expand = 3
  formula = Nd
  name = G4_Nd
  specific = 4
FEATURE [App::DocumentObjectGroupPython] Pm_element001  label="Pm_element : 1"  # scripted group (container) (typed FeaturePython)
  n = 1
  ref = Pm_element
FEATURE [App::DocumentObjectGroupPython] G4_Pm  # scripted group (container) (typed FeaturePython)
  Dunit = g/cm3
  Dvalue = 7.22
  Group = -> [Pm_element001]
  conduct = 2
  density = 1
  expand = 3
  formula = Pm
  name = G4_Pm
  specific = 4
FEATURE [App::DocumentObjectGroupPython] Sm_element001  label="Sm_element : 1"  # scripted group (container) (typed FeaturePython)
  n = 1
  ref = Sm_element
FEATURE [App::DocumentObjectGroupPython] G4_Sm  # scripted group (container) (typed FeaturePython)
  Dunit = g/cm3
  Dvalue = 7.46
  Group = -> [Sm_element001]
  conduct = 2
  density = 1
  expand = 3
  formula = Sm
  name = G4_Sm
  specific = 4
FEATURE [App::DocumentObjectGroupPython] Eu_element001  label="Eu_element : 1"  # scripted group (container) (typed FeaturePython)
  n = 1
  ref = Eu_element
FEATURE [App::DocumentObjectGroupPython] G4_Eu  # scripted group (container) (typed FeaturePython)
  Dunit = g/cm3
  Dvalue = 5.243
  Group = -> [Eu_element001]
  conduct = 2
  density = 1
  expand = 3
  formula = Eu
  name = G4_Eu
  specific = 4
FEATURE [App::DocumentObjectGroupPython] Gd_element002  label="Gd_element : 1"  # scripted group (container) (typed FeaturePython)
  n = 1
  ref = Gd_element
FEATURE [App::DocumentObjectGroupPython] G4_Gd  # scripted group (container) (typed FeaturePython)
  Dunit = g/cm3
  Dvalue = 7.9004
  Group = -> [Gd_element002]
  conduct = 2
  density = 1
  expand = 3
  formula = Gd
  name = G4_Gd
  specific = 4
FEATURE [App::DocumentObjectGroupPython] Tb_element001  label="Tb_element : 1"  # scripted group (container) (typed FeaturePython)
  n = 1
  ref = Tb_element
FEATURE [App::DocumentObjectGroupPython] G4_Tb  # scripted group (container) (typed FeaturePython)
  Dunit = g/cm3
  Dvalue = 8.229
  Group = -> [Tb_element001]
  conduct = 2
  density = 1
  expand = 3
  formula = Tb
  name = G4_Tb
  specific = 4
FEATURE [App::DocumentObjectGroupPython] Dy_element001  label="Dy_element : 1"  # scripted group (container) (typed FeaturePython)
  n = 1
  ref = Dy_element
FEATURE [App::DocumentObjectGroupPython] G4_Dy  # scripted group (container) (typed FeaturePython)
  Dunit = g/cm3
  Dvalue = 8.55
  Group = -> [Dy_element001]
  conduct = 2
  density = 1
  expand = 3
  formula = Dy
  name = G4_Dy
  specific = 4
FEATURE [App::DocumentObjectGroupPython] Ho_element001  label="Ho_element : 1"  # scripted group (container) (typed FeaturePython)
  n = 1
  ref = Ho_element
FEATURE [App::DocumentObjectGroupPython] G4_Ho  # scripted group (container) (typed FeaturePython)
  Dunit = g/cm3
  Dvalue = 8.795
  Group = -> [Ho_element001]
  conduct = 2
  density = 1
  expand = 3
  formula = Ho
  name = G4_Ho
  specific = 4
FEATURE [App::DocumentObjectGroupPython] Er_element001  label="Er_element : 1"  # scripted group (container) (typed FeaturePython)
  n = 1
  ref = Er_element
FEATURE [App::DocumentObjectGroupPython] G4_Er  # scripted group (container) (typed FeaturePython)
  Dunit = g/cm3
  Dvalue = 9.066
  Group = -> [Er_element001]
  conduct = 2
  density = 1
  expand = 3
  formula = Er
  name = G4_Er
  specific = 4
FEATURE [App::DocumentObjectGroupPython] Tm_element001  label="Tm_element : 1"  # scripted group (container) (typed FeaturePython)
  n = 1
  ref = Tm_element
FEATURE [App::DocumentObjectGroupPython] G4_Tm  # scripted group (container) (typed FeaturePython)
  Dunit = g/cm3
  Dvalue = 9.321
  Group = -> [Tm_element001]
  conduct = 2
  density = 1
  expand = 3
  formula = Tm
  name = G4_Tm
  specific = 4
FEATURE [App::DocumentObjectGroupPython] Yb_element001  label="Yb_element : 1"  # scripted group (container) (typed FeaturePython)
  n = 1
  ref = Yb_element
FEATURE [App::DocumentObjectGroupPython] G4_Yb  # scripted group (container) (typed FeaturePython)
  Dunit = g/cm3
  Dvalue = 6.73
  Group = -> [Yb_element001]
  conduct = 2
  density = 1
  expand = 3
  formula = Yb
  name = G4_Yb
  specific = 4
FEATURE [App::DocumentObjectGroupPython] Lu_element001  label="Lu_element : 1"  # scripted group (container) (typed FeaturePython)
  n = 1
  ref = Lu_element
FEATURE [App::DocumentObjectGroupPython] G4_Lu  # scripted group (container) (typed FeaturePython)
  Dunit = g/cm3
  Dvalue = 9.84
  Group = -> [Lu_element001]
  conduct = 2
  density = 1
  expand = 3
  formula = Lu
  name = G4_Lu
  specific = 4
FEATURE [App::DocumentObjectGroupPython] Hf_element001  label="Hf_element : 1"  # scripted group (container) (typed FeaturePython)
  n = 1
  ref = Hf_element
FEATURE [App::DocumentObjectGroupPython] G4_Hf  # scripted group (container) (typed FeaturePython)
  Dunit = g/cm3
  Dvalue = 13.31
  Group = -> [Hf_element001]
  conduct = 2
  density = 1
  expand = 3
  formula = Hf
  name = G4_Hf
  specific = 4
FEATURE [App::DocumentObjectGroupPython] Ta_element001  label="Ta_element : 1"  # scripted group (container) (typed FeaturePython)
  n = 1
  ref = Ta_element
FEATURE [App::DocumentObjectGroupPython] G4_Ta  # scripted group (container) (typed FeaturePython)
  Dunit = g/cm3
  Dvalue = 16.654
  Group = -> [Ta_element001]
  conduct = 2
  density = 1
  expand = 3
  formula = Ta
  name = G4_Ta
  specific = 4
FEATURE [App::DocumentObjectGroupPython] W_element004  label="W_element : 004"  # scripted group (container) (typed FeaturePython)
  n = 1
  ref = W_element
FEATURE [App::DocumentObjectGroupPython] G4_W  # scripted group (container) (typed FeaturePython)
  Dunit = g/cm3
  Dvalue = 19.3
  Group = -> [W_element004]
  conduct = 2
  density = 1
  expand = 3
  formula = W
  name = G4_W
  specific = 4
FEATURE [App::DocumentObjectGroupPython] Re_element001  label="Re_element : 1"  # scripted group (container) (typed FeaturePython)
  n = 1
  ref = Re_element
FEATURE [App::DocumentObjectGroupPython] G4_Re  # scripted group (container) (typed FeaturePython)
  Dunit = g/cm3
  Dvalue = 21.02
  Group = -> [Re_element001]
  conduct = 2
  density = 1
  expand = 3
  formula = Re
  name = G4_Re
  specific = 4
FEATURE [App::DocumentObjectGroupPython] Os_element001  label="Os_element : 1"  # scripted group (container) (typed FeaturePython)
  n = 1
  ref = Os_element
FEATURE [App::DocumentObjectGroupPython] G4_Os  # scripted group (container) (typed FeaturePython)
  Dunit = g/cm3
  Dvalue = 22.57
  Group = -> [Os_element001]
  conduct = 2
  density = 1
  expand = 3
  formula = Os
  name = G4_Os
  specific = 4
FEATURE [App::DocumentObjectGroupPython] Ir_element001  label="Ir_element : 1"  # scripted group (container) (typed FeaturePython)
  n = 1
  ref = Ir_element
FEATURE [App::DocumentObjectGroupPython] G4_Ir  # scripted group (container) (typed FeaturePython)
  Dunit = g/cm3
  Dvalue = 22.42
  Group = -> [Ir_element001]
  conduct = 2
  density = 1
  expand = 3
  formula = Ir
  name = G4_Ir
  specific = 4
FEATURE [App::DocumentObjectGroupPython] Pt_element001  label="Pt_element : 1"  # scripted group (container) (typed FeaturePython)
  n = 1
  ref = Pt_element
FEATURE [App::DocumentObjectGroupPython] G4_Pt  # scripted group (container) (typed FeaturePython)
  Dunit = g/cm3
  Dvalue = 21.45
  Group = -> [Pt_element001]
  conduct = 2
  density = 1
  expand = 3
  formula = Pt
  name = G4_Pt
  specific = 4
FEATURE [App::DocumentObjectGroupPython] Au_element001  label="Au_element : 1"  # scripted group (container) (typed FeaturePython)
  n = 1
  ref = Au_element
FEATURE [App::DocumentObjectGroupPython] G4_Au  # scripted group (container) (typed FeaturePython)
  Dunit = g/cm3
  Dvalue = 19.32
  Group = -> [Au_element001]
  conduct = 2
  density = 1
  expand = 3
  formula = Au
  name = G4_Au
  specific = 4
FEATURE [App::DocumentObjectGroupPython] Hg_element002  label="Hg_element : 002"  # scripted group (container) (typed FeaturePython)
  n = 1
  ref = Hg_element
FEATURE [App::DocumentObjectGroupPython] G4_Hg  # scripted group (container) (typed FeaturePython)
  Dunit = g/cm3
  Dvalue = 13.546
  Group = -> [Hg_element002]
  conduct = 2
  density = 1
  expand = 3
  formula = Hg
  name = G4_Hg
  specific = 4
FEATURE [App::DocumentObjectGroupPython] Tl_element002  label="Tl_element : 002"  # scripted group (container) (typed FeaturePython)
  n = 1
  ref = Tl_element
FEATURE [App::DocumentObjectGroupPython] G4_Tl  # scripted group (container) (typed FeaturePython)
  Dunit = g/cm3
  Dvalue = 11.72
  Group = -> [Tl_element002]
  conduct = 2
  density = 1
  expand = 3
  formula = Tl
  name = G4_Tl
  specific = 4
FEATURE [App::DocumentObjectGroupPython] Pb_element003  label="Pb_element : 1"  # scripted group (container) (typed FeaturePython)
  n = 1
  ref = Pb_element
FEATURE [App::DocumentObjectGroupPython] G4_Pb  # scripted group (container) (typed FeaturePython)
  Dunit = g/cm3
  Dvalue = 11.35
  Group = -> [Pb_element003]
  conduct = 2
  density = 1
  expand = 3
  formula = Pb
  name = G4_Pb
  specific = 4
FEATURE [App::DocumentObjectGroupPython] Bi_element002  label="Bi_element : 1"  # scripted group (container) (typed FeaturePython)
  n = 1
  ref = Bi_element
FEATURE [App::DocumentObjectGroupPython] G4_Bi  # scripted group (container) (typed FeaturePython)
  Dunit = g/cm3
  Dvalue = 9.747
  Group = -> [Bi_element002]
  conduct = 2
  density = 1
  expand = 3
  formula = Bi
  name = G4_Bi
  specific = 4
FEATURE [App::DocumentObjectGroupPython] Po_element001  label="Po_element : 1"  # scripted group (container) (typed FeaturePython)
  n = 1
  ref = Po_element
FEATURE [App::DocumentObjectGroupPython] G4_Po  # scripted group (container) (typed FeaturePython)
  Dunit = g/cm3
  Dvalue = 9.32
  Group = -> [Po_element001]
  conduct = 2
  density = 1
  expand = 3
  formula = Po
  name = G4_Po
  specific = 4
FEATURE [App::DocumentObjectGroupPython] At_element001  label="At_element : 1"  # scripted group (container) (typed FeaturePython)
  n = 1
  ref = At_element
FEATURE [App::DocumentObjectGroupPython] G4_At  # scripted group (container) (typed FeaturePython)
  Dunit = g/cm3
  Dvalue = 9.32
  Group = -> [At_element001]
  conduct = 2
  density = 1
  expand = 3
  formula = At
  name = G4_At
  specific = 4
FEATURE [App::DocumentObjectGroupPython] Rn_element001  label="Rn_element : 1"  # scripted group (container) (typed FeaturePython)
  n = 1
  ref = Rn_element
FEATURE [App::DocumentObjectGroupPython] G4_Rn  # scripted group (container) (typed FeaturePython)
  Dunit = g/cm3
  Dvalue = 0.00900662
  Group = -> [Rn_element001]
  conduct = 2
  density = 1
  expand = 3
  formula = Rn
  name = G4_Rn
  specific = 4
FEATURE [App::DocumentObjectGroupPython] Fr_element001  label="Fr_element : 1"  # scripted group (container) (typed FeaturePython)
  n = 1
  ref = Fr_element
FEATURE [App::DocumentObjectGroupPython] G4_Fr  # scripted group (container) (typed FeaturePython)
  Dunit = g/cm3
  Dvalue = 1
  Group = -> [Fr_element001]
  conduct = 2
  density = 1
  expand = 3
  formula = Fr
  name = G4_Fr
  specific = 4
FEATURE [App::DocumentObjectGroupPython] Ra_element001  label="Ra_element : 1"  # scripted group (container) (typed FeaturePython)
  n = 1
  ref = Ra_element
FEATURE [App::DocumentObjectGroupPython] G4_Ra  # scripted group (container) (typed FeaturePython)
  Dunit = g/cm3
  Dvalue = 5
  Group = -> [Ra_element001]
  conduct = 2
  density = 1
  expand = 3
  formula = Ra
  name = G4_Ra
  specific = 4
FEATURE [App::DocumentObjectGroupPython] Ac_element001  label="Ac_element : 1"  # scripted group (container) (typed FeaturePython)
  n = 1
  ref = Ac_element
FEATURE [App::DocumentObjectGroupPython] G4_Ac  # scripted group (container) (typed FeaturePython)
  Dunit = g/cm3
  Dvalue = 10.07
  Group = -> [Ac_element001]
  conduct = 2
  density = 1
  expand = 3
  formula = Ac
  name = G4_Ac
  specific = 4
FEATURE [App::DocumentObjectGroupPython] Th_element001  label="Th_element : 1"  # scripted group (container) (typed FeaturePython)
  n = 1
  ref = Th_element
FEATURE [App::DocumentObjectGroupPython] G4_Th  # scripted group (container) (typed FeaturePython)
  Dunit = g/cm3
  Dvalue = 11.72
  Group = -> [Th_element001]
  conduct = 2
  density = 1
  expand = 3
  formula = Th
  name = G4_Th
  specific = 4
FEATURE [App::DocumentObjectGroupPython] Pa_element001  label="Pa_element : 1"  # scripted group (container) (typed FeaturePython)
  n = 1
  ref = Pa_element
FEATURE [App::DocumentObjectGroupPython] G4_Pa  # scripted group (container) (typed FeaturePython)
  Dunit = g/cm3
  Dvalue = 15.37
  Group = -> [Pa_element001]
  conduct = 2
  density = 1
  expand = 3
  formula = Pa
  name = G4_Pa
  specific = 4
FEATURE [App::DocumentObjectGroupPython] U_element004  label="U_element : 004"  # scripted group (container) (typed FeaturePython)
  n = 1
  ref = U_element
FEATURE [App::DocumentObjectGroupPython] G4_U  # scripted group (container) (typed FeaturePython)
  Dunit = g/cm3
  Dvalue = 18.95
  Group = -> [U_element004]
  conduct = 2
  density = 1
  expand = 3
  formula = U
  name = G4_U
  specific = 4
FEATURE [App::DocumentObjectGroupPython] Np_element001  label="Np_element : 1"  # scripted group (container) (typed FeaturePython)
  n = 1
  ref = Np_element
FEATURE [App::DocumentObjectGroupPython] G4_Np  # scripted group (container) (typed FeaturePython)
  Dunit = g/cm3
  Dvalue = 20.25
  Group = -> [Np_element001]
  conduct = 2
  density = 1
  expand = 3
  formula = Np
  name = G4_Np
  specific = 4
FEATURE [App::DocumentObjectGroupPython] Pu_element002  label="Pu_element : 002"  # scripted group (container) (typed FeaturePython)
  n = 1
  ref = Pu_element
FEATURE [App::DocumentObjectGroupPython] G4_Pu  # scripted group (container) (typed FeaturePython)
  Dunit = g/cm3
  Dvalue = 19.84
  Group = -> [Pu_element002]
  conduct = 2
  density = 1
  expand = 3
  formula = Pu
  name = G4_Pu
  specific = 4
FEATURE [App::DocumentObjectGroupPython] Am_element001  label="Am_element : 1"  # scripted group (container) (typed FeaturePython)
  n = 1
  ref = Am_element
FEATURE [App::DocumentObjectGroupPython] G4_Am  # scripted group (container) (typed FeaturePython)
  Dunit = g/cm3
  Dvalue = 13.67
  Group = -> [Am_element001]
  conduct = 2
  density = 1
  expand = 3
  formula = Am
  name = G4_Am
  specific = 4
FEATURE [App::DocumentObjectGroupPython] Cm_element001  label="Cm_element : 1"  # scripted group (container) (typed FeaturePython)
  n = 1
  ref = Cm_element
FEATURE [App::DocumentObjectGroupPython] G4_Cm  # scripted group (container) (typed FeaturePython)
  Dunit = g/cm3
  Dvalue = 13.51
  Group = -> [Cm_element001]
  conduct = 2
  density = 1
  expand = 3
  formula = Cm
  name = G4_Cm
  specific = 4
FEATURE [App::DocumentObjectGroupPython] Bk_element001  label="Bk_element : 1"  # scripted group (container) (typed FeaturePython)
  n = 1
  ref = Bk_element
FEATURE [App::DocumentObjectGroupPython] G4_Bk  # scripted group (container) (typed FeaturePython)
  Dunit = g/cm3
  Dvalue = 14
  Group = -> [Bk_element001]
  conduct = 2
  density = 1
  expand = 3
  formula = Bk
  name = G4_Bk
  specific = 4
FEATURE [App::DocumentObjectGroupPython] Cf_element001  label="Cf_element : 1"  # scripted group (container) (typed FeaturePython)
  n = 1
  ref = Cf_element
FEATURE [App::DocumentObjectGroupPython] G4_Cf  # scripted group (container) (typed FeaturePython)
  Dunit = g/cm3
  Dvalue = 10
  Group = -> [Cf_element001]
  conduct = 2
  density = 1
  expand = 3
  formula = Cf
  name = G4_Cf
  specific = 4
FEATURE [App::DocumentObjectGroupPython] Element  # scripted group (container) (typed FeaturePython)
  Group = -> [G4_H,G4_He,G4_Li,G4_Be,G4_B,G4_C,G4_N,G4_O,G4_F,G4_Ne,G4_Na,G4_Mg,G4_Al,G4_Si,G4_P,G4_S,G4_Cl,G4_Ar,G4_K,G4_Ca,G4_Sc,G4_Ti,G4_V,G4_Cr,G4_Mn,G4_Fe,G4_Co,G4_Ni,G4_Cu,G4_Zn,G4_Ga,G4_Ge,G4_As,G4_Se,G4_Br,G4_Kr,G4_Rb,G4_Sr,G4_Y,G4_Zr,G4_Nb,G4_Mo,G4_Tc,G4_Ru,G4_Rh,G4_Pd,G4_Ag,G4_Cd,G4_In,G4_Sn,G4_Sb,G4_Te,G4_I,G4_Xe,G4_Cs,G4_Ba,G4_La,G4_Ce,G4_Pr,G4_Nd,G4_Pm,G4_Sm,G4_Eu,G4_Gd,G4_Tb,G4_Dy,G4_Ho,G4_Er,+30 more]
FEATURE [App::DocumentObjectGroupPython] H_element114  label="H_element : 063"  # scripted group (container) (typed FeaturePython)
  n = 2
  ref = H_element
FEATURE [App::DocumentObjectGroupPython] G4_lH2  # scripted group (container) (typed FeaturePython)
  Dunit = g/cm3
  Dvalue = 0.0708
  Group = -> [H_element114]
  conduct = 2
  density = 1
  expand = 3
  formula = G4_lH2
  name = G4_lH2
  specific = 4
FEATURE [App::DocumentObjectGroupPython] N_element049  label="N_element : 022"  # scripted group (container) (typed FeaturePython)
  n = 2
  ref = N_element
FEATURE [App::DocumentObjectGroupPython] G4_lN2  # scripted group (container) (typed FeaturePython)
  Dunit = g/cm3
  Dvalue = 0.807
  Group = -> [N_element049]
  conduct = 2
  density = 1
  expand = 3
  formula = G4_lN2
  name = G4_lN2
  specific = 4
FEATURE [App::DocumentObjectGroupPython] O_element106  label="O_element : 060"  # scripted group (container) (typed FeaturePython)
  n = 2
  ref = O_element
FEATURE [App::DocumentObjectGroupPython] G4_lO2  # scripted group (container) (typed FeaturePython)
  Dunit = g/cm3
  Dvalue = 1.141
  Group = -> [O_element106]
  conduct = 2
  density = 1
  expand = 3
  formula = G4_lO2
  name = G4_lO2
  specific = 4
FEATURE [App::DocumentObjectGroupPython] Ar  label="Ar : 1"  # scripted group (container) (typed FeaturePython)
  n = 1
  ref = Ar
FEATURE [App::DocumentObjectGroupPython] G4_lAr  # scripted group (container) (typed FeaturePython)
  Dunit = g/cm3
  Dvalue = 1.396
  Group = -> [Ar]
  conduct = 2
  density = 1
  expand = 3
  formula = G4_lAr
  name = G4_lAr
  specific = 4
FEATURE [App::DocumentObjectGroupPython] Br  label="Br : 1"  # scripted group (container) (typed FeaturePython)
  n = 1
  ref = Br
FEATURE [App::DocumentObjectGroupPython] G4_lBr  # scripted group (container) (typed FeaturePython)
  Dunit = g/cm3
  Dvalue = 3.1028
  Group = -> [Br]
  conduct = 2
  density = 1
  expand = 3
  formula = G4_lBr
  name = G4_lBr
  specific = 4
FEATURE [App::DocumentObjectGroupPython] Kr  label="Kr : 1"  # scripted group (container) (typed FeaturePython)
  n = 1
  ref = Kr
FEATURE [App::DocumentObjectGroupPython] G4_lKr  # scripted group (container) (typed FeaturePython)
  Dunit = g/cm3
  Dvalue = 2.418
  Group = -> [Kr]
  conduct = 2
  density = 1
  expand = 3
  formula = G4_lKr
  name = G4_lKr
  specific = 4
FEATURE [App::DocumentObjectGroupPython] Xe  label="Xe : 1"  # scripted group (container) (typed FeaturePython)
  n = 1
  ref = Xe
FEATURE [App::DocumentObjectGroupPython] G4_lXe  # scripted group (container) (typed FeaturePython)
  Dunit = g/cm3
  Dvalue = 2.953
  Group = -> [Xe]
  conduct = 2
  density = 1
  expand = 3
  formula = G4_lXe
  name = G4_lXe
  specific = 4
FEATURE [App::DocumentObjectGroupPython] O_element107  label="O_element : 061"  # scripted group (container) (typed FeaturePython)
  n = 4
  ref = O_element
FEATURE [App::DocumentObjectGroupPython] Pb_element004  label="Pb_element : 002"  # scripted group (container) (typed FeaturePython)
  n = 1
  ref = Pb_element
FEATURE [App::DocumentObjectGroupPython] W_element005  label="W_element : 005"  # scripted group (container) (typed FeaturePython)
  n = 1
  ref = W_element
FEATURE [App::DocumentObjectGroupPython] G4_PbWO4  # scripted group (container) (typed FeaturePython)
  Dunit = g/cm3
  Dvalue = 8.28
  Group = -> [O_element107,Pb_element004,W_element005]
  conduct = 2
  density = 1
  expand = 3
  formula = G4_PbWO4
  name = G4_PbWO4
  specific = 4
FEATURE [App::DocumentObjectGroupPython] alactic  label="alactic : 1"  # scripted group (container) (typed FeaturePython)
  n = 1
  ref = alactic
FEATURE [App::DocumentObjectGroupPython] G4_Galactic  # scripted group (container) (typed FeaturePython)
  Dunit = g/cm3
  Dvalue = 0
  Group = -> [alactic]
  conduct = 2
  density = 1
  expand = 3
  formula = G4_Galactic
  name = G4_Galactic
  specific = 4
FEATURE [App::DocumentObjectGroupPython] RAPHITE_POROUS  label="RAPHITE_POROUS : 1"  # scripted group (container) (typed FeaturePython)
  n = 1
  ref = RAPHITE_POROUS
FEATURE [App::DocumentObjectGroupPython] G4_GRAPHITE_POROUS  # scripted group (container) (typed FeaturePython)
  Dunit = g/cm3
  Dvalue = 1.7
  Group = -> [RAPHITE_POROUS]
  conduct = 2
  density = 1
  expand = 3
  formula = G4_GRAPHITE_POROUS
  name = G4_GRAPHITE_POROUS
  specific = 4
FEATURE [App::DocumentObjectGroupPython] H_element115  label="H_element : 0.150"  # scripted group (container) (typed FeaturePython)
  n = 0.080538
FEATURE [App::DocumentObjectGroupPython] C_element125  label="C_element : 0.600"  # scripted group (container) (typed FeaturePython)
  n = 0.599848
FEATURE [App::DocumentObjectGroupPython] O_element108  label="O_element : 0.320"  # scripted group (container) (typed FeaturePython)
  n = 0.319614
FEATURE [App::DocumentObjectGroupPython] G4_LUCITE  # scripted group (container) (typed FeaturePython)
  Dunit = g/cm3
  Dvalue = 1.19
  Group = -> [H_element115,C_element125,O_element108]
  conduct = 2
  density = 1
  expand = 3
  formula = G4_LUCITE
  name = G4_LUCITE
  specific = 4
FEATURE [App::DocumentObjectGroupPython] Cu_element002  label="Cu_element : 62"  # scripted group (container) (typed FeaturePython)
  n = 62
  ref = Cu_element
FEATURE [App::DocumentObjectGroupPython] Zn_element002  label="Zn_element : 35"  # scripted group (container) (typed FeaturePython)
  n = 35
  ref = Zn_element
FEATURE [App::DocumentObjectGroupPython] Pb_element005  label="Pb_element : 3"  # scripted group (container) (typed FeaturePython)
  n = 3
  ref = Pb_element
FEATURE [App::DocumentObjectGroupPython] G4_BRASS  # scripted group (container) (typed FeaturePython)
  Dunit = g/cm3
  Dvalue = 8.52
  Group = -> [Cu_element002,Zn_element002,Pb_element005]
  conduct = 2
  density = 1
  expand = 3
  formula = G4_BRASS
  name = G4_BRASS
  specific = 4
FEATURE [App::DocumentObjectGroupPython] Cu_element003  label="Cu_element : 89"  # scripted group (container) (typed FeaturePython)
  n = 89
  ref = Cu_element
FEATURE [App::DocumentObjectGroupPython] Zn_element003  label="Zn_element : 9"  # scripted group (container) (typed FeaturePython)
  n = 9
  ref = Zn_element
FEATURE [App::DocumentObjectGroupPython] Pb_element006  label="Pb_element : 2"  # scripted group (container) (typed FeaturePython)
  n = 2
  ref = Pb_element
FEATURE [App::DocumentObjectGroupPython] G4_BRONZE  # scripted group (container) (typed FeaturePython)
  Dunit = g/cm3
  Dvalue = 8.82
  Group = -> [Cu_element003,Zn_element003,Pb_element006]
  conduct = 2
  density = 1
  expand = 3
  formula = G4_BRONZE
  name = G4_BRONZE
  specific = 4
FEATURE [App::DocumentObjectGroupPython] Fe_element008  label="Fe_element : 74"  # scripted group (container) (typed FeaturePython)
  n = 74
  ref = Fe_element
FEATURE [App::DocumentObjectGroupPython] Cr_element002  label="Cr_element : 18"  # scripted group (container) (typed FeaturePython)
  n = 18
  ref = Cr_element
FEATURE [App::DocumentObjectGroupPython] Ni_element002  label="Ni_element : 8"  # scripted group (container) (typed FeaturePython)
  n = 8
  ref = Ni_element
FEATURE [App::DocumentObjectGroupPython] G4_STAINLESS_STEEL  label="G4_STAINLESS-STEEL"  # scripted group (container) (typed FeaturePython)
  Dunit = g/cm3
  Dvalue = 8
  Group = -> [Fe_element008,Cr_element002,Ni_element002]
  conduct = 2
  density = 1
  expand = 3
  formula = G4_STAINLESS-STEEL
  name = G4_STAINLESS-STEEL
  specific = 4
FEATURE [App::DocumentObjectGroupPython] H_element116  label="H_element : 064"  # scripted group (container) (typed FeaturePython)
  n = 18
  ref = H_element
FEATURE [App::DocumentObjectGroupPython] C_element126  label="C_element : 071"  # scripted group (container) (typed FeaturePython)
  n = 12
  ref = C_element
FEATURE [App::DocumentObjectGroupPython] O_element109  label="O_element : 062"  # scripted group (container) (typed FeaturePython)
  n = 7
  ref = O_element
FEATURE [App::DocumentObjectGroupPython] G4_CR39  # scripted group (container) (typed FeaturePython)
  Dunit = g/cm3
  Dvalue = 1.32
  Group = -> [H_element116,C_element126,O_element109]
  conduct = 2
  density = 1
  expand = 3
  formula = G4_CR39
  name = G4_CR39
  specific = 4
FEATURE [App::DocumentObjectGroupPython] H_element117  label="H_element : 38"  # scripted group (container) (typed FeaturePython)
  n = 38
  ref = H_element
FEATURE [App::DocumentObjectGroupPython] C_element127  label="C_element : 072"  # scripted group (container) (typed FeaturePython)
  n = 18
  ref = C_element
FEATURE [App::DocumentObjectGroupPython] O_element110  label="O_element : 063"  # scripted group (container) (typed FeaturePython)
  n = 1
  ref = O_element
FEATURE [App::DocumentObjectGroupPython] G4_OCTADECANOL  # scripted group (container) (typed FeaturePython)
  Dunit = g/cm3
  Dvalue = 0.812
  Group = -> [H_element117,C_element127,O_element110]
  conduct = 2
  density = 1
  expand = 3
  formula = G4_OCTADECANOL
  name = G4_OCTADECANOL
  specific = 4
FEATURE [App::DocumentObjectGroupPython] HEP  # scripted group (container) (typed FeaturePython)
  Group = -> [G4_lH2,G4_lN2,G4_lO2,G4_lAr,G4_lBr,G4_lKr,G4_lXe,G4_PbWO4,G4_Galactic,G4_GRAPHITE_POROUS,G4_LUCITE,G4_BRASS,G4_BRONZE,G4_STAINLESS_STEEL,G4_CR39,G4_OCTADECANOL]
FEATURE [App::DocumentObjectGroupPython] C_element128  label="C_element : 073"  # scripted group (container) (typed FeaturePython)
  n = 14
  ref = C_element
FEATURE [App::DocumentObjectGroupPython] H_element118  label="H_element : 065"  # scripted group (container) (typed FeaturePython)
  n = 10
  ref = H_element
FEATURE [App::DocumentObjectGroupPython] O_element111  label="O_element : 064"  # scripted group (container) (typed FeaturePython)
  n = 2
  ref = O_element
FEATURE [App::DocumentObjectGroupPython] N_element050  label="N_element : 023"  # scripted group (container) (typed FeaturePython)
  n = 2
  ref = N_element
FEATURE [App::DocumentObjectGroupPython] G4_KEVLAR  # scripted group (container) (typed FeaturePython)
  Dunit = g/cm3
  Dvalue = 1.44
  Group = -> [C_element128,H_element118,O_element111,N_element050]
  conduct = 2
  density = 1
  expand = 3
  formula = G4_KEVLAR
  name = G4_KEVLAR
  specific = 4
FEATURE [App::DocumentObjectGroupPython] C_element129  label="C_element : 074"  # scripted group (container) (typed FeaturePython)
  n = 10
  ref = C_element
FEATURE [App::DocumentObjectGroupPython] H_element119  label="H_element : 066"  # scripted group (container) (typed FeaturePython)
  n = 8
  ref = H_element
FEATURE [App::DocumentObjectGroupPython] O_element112  label="O_element : 065"  # scripted group (container) (typed FeaturePython)
  n = 4
  ref = O_element
FEATURE [App::DocumentObjectGroupPython] G4_DACRON  # scripted group (container) (typed FeaturePython)
  Dunit = g/cm3
  Dvalue = 1.4
  Group = -> [C_element129,H_element119,O_element112]
  conduct = 2
  density = 1
  expand = 3
  formula = G4_DACRON
  name = G4_DACRON
  specific = 4
FEATURE [App::DocumentObjectGroupPython] C_element130  label="C_element : 075"  # scripted group (container) (typed FeaturePython)
  n = 4
  ref = C_element
FEATURE [App::DocumentObjectGroupPython] H_element120  label="H_element : 067"  # scripted group (container) (typed FeaturePython)
  n = 5
  ref = H_element
FEATURE [App::DocumentObjectGroupPython] Cl_element030  label="Cl_element : 016"  # scripted group (container) (typed FeaturePython)
  n = 1
  ref = Cl_element
FEATURE [App::DocumentObjectGroupPython] G4_NEOPRENE  # scripted group (container) (typed FeaturePython)
  Dunit = g/cm3
  Dvalue = 1.23
  Group = -> [C_element130,H_element120,Cl_element030]
  conduct = 2
  density = 1
  expand = 3
  formula = G4_NEOPRENE
  name = G4_NEOPRENE
  specific = 4
FEATURE [App::DocumentObjectGroupPython] Space  # scripted group (container) (typed FeaturePython)
  Group = -> [G4_KEVLAR,G4_DACRON,G4_NEOPRENE]
FEATURE [App::DocumentObjectGroupPython] H_element121  label="H_element : 068"  # scripted group (container) (typed FeaturePython)
  n = 5
  ref = H_element
FEATURE [App::DocumentObjectGroupPython] C_element131  label="C_element : 076"  # scripted group (container) (typed FeaturePython)
  n = 4
  ref = C_element
FEATURE [App::DocumentObjectGroupPython] N_element051  label="N_element : 3"  # scripted group (container) (typed FeaturePython)
  n = 3
  ref = N_element
FEATURE [App::DocumentObjectGroupPython] O_element113  label="O_element : 066"  # scripted group (container) (typed FeaturePython)
  n = 1
  ref = O_element
FEATURE [App::DocumentObjectGroupPython] G4_CYTOSINE  # scripted group (container) (typed FeaturePython)
  Dunit = g/cm3
  Dvalue = 1.55
  Group = -> [H_element121,C_element131,N_element051,O_element113]
  conduct = 2
  density = 1
  expand = 3
  formula = G4_CYTOSINE
  name = G4_CYTOSINE
  specific = 4
FEATURE [App::DocumentObjectGroupPython] H_element122  label="H_element : 069"  # scripted group (container) (typed FeaturePython)
  n = 6
  ref = H_element
FEATURE [App::DocumentObjectGroupPython] C_element132  label="C_element : 077"  # scripted group (container) (typed FeaturePython)
  n = 5
  ref = C_element
FEATURE [App::DocumentObjectGroupPython] N_element052  label="N_element : 024"  # scripted group (container) (typed FeaturePython)
  n = 2
  ref = N_element
FEATURE [App::DocumentObjectGroupPython] O_element114  label="O_element : 067"  # scripted group (container) (typed FeaturePython)
  n = 2
  ref = O_element
FEATURE [App::DocumentObjectGroupPython] G4_THYMINE  # scripted group (container) (typed FeaturePython)
  Dunit = g/cm3
  Dvalue = 1.23
  Group = -> [H_element122,C_element132,N_element052,O_element114]
  conduct = 2
  density = 1
  expand = 3
  formula = G4_THYMINE
  name = G4_THYMINE
  specific = 4
FEATURE [App::DocumentObjectGroupPython] H_element123  label="H_element : 070"  # scripted group (container) (typed FeaturePython)
  n = 4
  ref = H_element
FEATURE [App::DocumentObjectGroupPython] C_element133  label="C_element : 078"  # scripted group (container) (typed FeaturePython)
  n = 4
  ref = C_element
FEATURE [App::DocumentObjectGroupPython] N_element053  label="N_element : 025"  # scripted group (container) (typed FeaturePython)
  n = 2
  ref = N_element
FEATURE [App::DocumentObjectGroupPython] O_element115  label="O_element : 068"  # scripted group (container) (typed FeaturePython)
  n = 2
  ref = O_element
FEATURE [App::DocumentObjectGroupPython] G4_URACIL  # scripted group (container) (typed FeaturePython)
  Dunit = g/cm3
  Dvalue = 1.32
  Group = -> [H_element123,C_element133,N_element053,O_element115]
  conduct = 2
  density = 1
  expand = 3
  formula = G4_URACIL
  name = G4_URACIL
  specific = 4
FEATURE [App::DocumentObjectGroupPython] H_element124  label="H_element : 071"  # scripted group (container) (typed FeaturePython)
  n = 4
  ref = H_element
FEATURE [App::DocumentObjectGroupPython] C_element134  label="C_element : 079"  # scripted group (container) (typed FeaturePython)
  n = 5
  ref = C_element
FEATURE [App::DocumentObjectGroupPython] N_element054  label="N_element : 026"  # scripted group (container) (typed FeaturePython)
  n = 5
  ref = N_element
FEATURE [App::DocumentObjectGroupPython] G4_DNA_ADENINE  # scripted group (container) (typed FeaturePython)
  Dunit = g/cm3
  Dvalue = 1
  Group = -> [H_element124,C_element134,N_element054]
  conduct = 2
  density = 1
  expand = 3
  formula = G4_DNA_ADENINE
  name = G4_DNA_ADENINE
  specific = 4
FEATURE [App::DocumentObjectGroupPython] H_element125  label="H_element : 072"  # scripted group (container) (typed FeaturePython)
  n = 4
  ref = H_element
FEATURE [App::DocumentObjectGroupPython] C_element135  label="C_element : 080"  # scripted group (container) (typed FeaturePython)
  n = 5
  ref = C_element
FEATURE [App::DocumentObjectGroupPython] N_element055  label="N_element : 027"  # scripted group (container) (typed FeaturePython)
  n = 5
  ref = N_element
FEATURE [App::DocumentObjectGroupPython] O_element116  label="O_element : 069"  # scripted group (container) (typed FeaturePython)
  n = 1
  ref = O_element
FEATURE [App::DocumentObjectGroupPython] G4_DNA_GUANINE  # scripted group (container) (typed FeaturePython)
  Dunit = g/cm3
  Dvalue = 1
  Group = -> [H_element125,C_element135,N_element055,O_element116]
  conduct = 2
  density = 1
  expand = 3
  formula = G4_DNA_GUANINE
  name = G4_DNA_GUANINE
  specific = 4
FEATURE [App::DocumentObjectGroupPython] H_element126  label="H_element : 073"  # scripted group (container) (typed FeaturePython)
  n = 4
  ref = H_element
FEATURE [App::DocumentObjectGroupPython] C_element136  label="C_element : 081"  # scripted group (container) (typed FeaturePython)
  n = 4
  ref = C_element
FEATURE [App::DocumentObjectGroupPython] N_element056  label="N_element : 028"  # scripted group (container) (typed FeaturePython)
  n = 3
  ref = N_element
FEATURE [App::DocumentObjectGroupPython] O_element117  label="O_element : 070"  # scripted group (container) (typed FeaturePython)
  n = 1
  ref = O_element
FEATURE [App::DocumentObjectGroupPython] G4_DNA_CYTOSINE  # scripted group (container) (typed FeaturePython)
  Dunit = g/cm3
  Dvalue = 1
  Group = -> [H_element126,C_element136,N_element056,O_element117]
  conduct = 2
  density = 1
  expand = 3
  formula = G4_DNA_CYTOSINE
  name = G4_DNA_CYTOSINE
  specific = 4
FEATURE [App::DocumentObjectGroupPython] H_element127  label="H_element : 074"  # scripted group (container) (typed FeaturePython)
  n = 5
  ref = H_element
FEATURE [App::DocumentObjectGroupPython] C_element137  label="C_element : 082"  # scripted group (container) (typed FeaturePython)
  n = 5
  ref = C_element
FEATURE [App::DocumentObjectGroupPython] N_element057  label="N_element : 029"  # scripted group (container) (typed FeaturePython)
  n = 2
  ref = N_element
FEATURE [App::DocumentObjectGroupPython] O_element118  label="O_element : 071"  # scripted group (container) (typed FeaturePython)
  n = 2
  ref = O_element
FEATURE [App::DocumentObjectGroupPython] G4_DNA_THYMINE  # scripted group (container) (typed FeaturePython)
  Dunit = g/cm3
  Dvalue = 1
  Group = -> [H_element127,C_element137,N_element057,O_element118]
  conduct = 2
  density = 1
  expand = 3
  formula = G4_DNA_THYMINE
  name = G4_DNA_THYMINE
  specific = 4
FEATURE [App::DocumentObjectGroupPython] H_element128  label="H_element : 075"  # scripted group (container) (typed FeaturePython)
  n = 3
  ref = H_element
FEATURE [App::DocumentObjectGroupPython] C_element138  label="C_element : 083"  # scripted group (container) (typed FeaturePython)
  n = 4
  ref = C_element
FEATURE [App::DocumentObjectGroupPython] N_element058  label="N_element : 030"  # scripted group (container) (typed FeaturePython)
  n = 2
  ref = N_element
FEATURE [App::DocumentObjectGroupPython] O_element119  label="O_element : 072"  # scripted group (container) (typed FeaturePython)
  n = 2
  ref = O_element
FEATURE [App::DocumentObjectGroupPython] G4_DNA_URACIL  # scripted group (container) (typed FeaturePython)
  Dunit = g/cm3
  Dvalue = 1
  Group = -> [H_element128,C_element138,N_element058,O_element119]
  conduct = 2
  density = 1
  expand = 3
  formula = G4_DNA_URACIL
  name = G4_DNA_URACIL
  specific = 4
FEATURE [App::DocumentObjectGroupPython] H_element129  label="H_element : 076"  # scripted group (container) (typed FeaturePython)
  n = 10
  ref = H_element
FEATURE [App::DocumentObjectGroupPython] C_element139  label="C_element : 084"  # scripted group (container) (typed FeaturePython)
  n = 10
  ref = C_element
FEATURE [App::DocumentObjectGroupPython] N_element059  label="N_element : 031"  # scripted group (container) (typed FeaturePython)
  n = 5
  ref = N_element
FEATURE [App::DocumentObjectGroupPython] O_element120  label="O_element : 073"  # scripted group (container) (typed FeaturePython)
  n = 4
  ref = O_element
FEATURE [App::DocumentObjectGroupPython] G4_DNA_ADENOSINE  # scripted group (container) (typed FeaturePython)
  Dunit = g/cm3
  Dvalue = 1
  Group = -> [H_element129,C_element139,N_element059,O_element120]
  conduct = 2
  density = 1
  expand = 3
  formula = G4_DNA_ADENOSINE
  name = G4_DNA_ADENOSINE
  specific = 4
FEATURE [App::DocumentObjectGroupPython] H_element130  label="H_element : 077"  # scripted group (container) (typed FeaturePython)
  n = 10
  ref = H_element
FEATURE [App::DocumentObjectGroupPython] C_element140  label="C_element : 085"  # scripted group (container) (typed FeaturePython)
  n = 10
  ref = C_element
FEATURE [App::DocumentObjectGroupPython] N_element060  label="N_element : 032"  # scripted group (container) (typed FeaturePython)
  n = 5
  ref = N_element
FEATURE [App::DocumentObjectGroupPython] O_element121  label="O_element : 074"  # scripted group (container) (typed FeaturePython)
  n = 5
  ref = O_element
FEATURE [App::DocumentObjectGroupPython] G4_DNA_GUANOSINE  # scripted group (container) (typed FeaturePython)
  Dunit = g/cm3
  Dvalue = 1
  Group = -> [H_element130,C_element140,N_element060,O_element121]
  conduct = 2
  density = 1
  expand = 3
  formula = G4_DNA_GUANOSINE
  name = G4_DNA_GUANOSINE
  specific = 4
FEATURE [App::DocumentObjectGroupPython] H_element131  label="H_element : 078"  # scripted group (container) (typed FeaturePython)
  n = 10
  ref = H_element
FEATURE [App::DocumentObjectGroupPython] C_element141  label="C_element : 086"  # scripted group (container) (typed FeaturePython)
  n = 9
  ref = C_element
FEATURE [App::DocumentObjectGroupPython] N_element061  label="N_element : 033"  # scripted group (container) (typed FeaturePython)
  n = 3
  ref = N_element
FEATURE [App::DocumentObjectGroupPython] O_element122  label="O_element : 075"  # scripted group (container) (typed FeaturePython)
  n = 5
  ref = O_element
FEATURE [App::DocumentObjectGroupPython] G4_DNA_CYTIDINE  # scripted group (container) (typed FeaturePython)
  Dunit = g/cm3
  Dvalue = 1
  Group = -> [H_element131,C_element141,N_element061,O_element122]
  conduct = 2
  density = 1
  expand = 3
  formula = G4_DNA_CYTIDINE
  name = G4_DNA_CYTIDINE
  specific = 4
FEATURE [App::DocumentObjectGroupPython] H_element132  label="H_element : 079"  # scripted group (container) (typed FeaturePython)
  n = 9
  ref = H_element
FEATURE [App::DocumentObjectGroupPython] C_element142  label="C_element : 087"  # scripted group (container) (typed FeaturePython)
  n = 9
  ref = C_element
FEATURE [App::DocumentObjectGroupPython] N_element062  label="N_element : 034"  # scripted group (container) (typed FeaturePython)
  n = 2
  ref = N_element
FEATURE [App::DocumentObjectGroupPython] O_element123  label="O_element : 076"  # scripted group (container) (typed FeaturePython)
  n = 6
  ref = O_element
FEATURE [App::DocumentObjectGroupPython] G4_DNA_URIDINE  # scripted group (container) (typed FeaturePython)
  Dunit = g/cm3
  Dvalue = 1
  Group = -> [H_element132,C_element142,N_element062,O_element123]
  conduct = 2
  density = 1
  expand = 3
  formula = G4_DNA_URIDINE
  name = G4_DNA_URIDINE
  specific = 4
FEATURE [App::DocumentObjectGroupPython] H_element133  label="H_element : 080"  # scripted group (container) (typed FeaturePython)
  n = 11
  ref = H_element
FEATURE [App::DocumentObjectGroupPython] C_element143  label="C_element : 088"  # scripted group (container) (typed FeaturePython)
  n = 10
  ref = C_element
FEATURE [App::DocumentObjectGroupPython] N_element063  label="N_element : 035"  # scripted group (container) (typed FeaturePython)
  n = 2
  ref = N_element
FEATURE [App::DocumentObjectGroupPython] O_element124  label="O_element : 077"  # scripted group (container) (typed FeaturePython)
  n = 6
  ref = O_element
FEATURE [App::DocumentObjectGroupPython] G4_DNA_METHYLURIDINE  # scripted group (container) (typed FeaturePython)
  Dunit = g/cm3
  Dvalue = 1
  Group = -> [H_element133,C_element143,N_element063,O_element124]
  conduct = 2
  density = 1
  expand = 3
  formula = G4_DNA_METHYLURIDINE
  name = G4_DNA_METHYLURIDINE
  specific = 4
FEATURE [App::DocumentObjectGroupPython] P_element014  label="P_element : 003"  # scripted group (container) (typed FeaturePython)
  n = 1
  ref = P_element
FEATURE [App::DocumentObjectGroupPython] O_element125  label="O_element : 078"  # scripted group (container) (typed FeaturePython)
  n = 3
  ref = O_element
FEATURE [App::DocumentObjectGroupPython] G4_DNA_MONOPHOSPHATE  # scripted group (container) (typed FeaturePython)
  Dunit = g/cm3
  Dvalue = 1
  Group = -> [P_element014,O_element125]
  conduct = 2
  density = 1
  expand = 3
  formula = G4_DNA_MONOPHOSPHATE
  name = G4_DNA_MONOPHOSPHATE
  specific = 4
FEATURE [App::DocumentObjectGroupPython] H_element134  label="H_element : 081"  # scripted group (container) (typed FeaturePython)
  n = 10
  ref = H_element
FEATURE [App::DocumentObjectGroupPython] C_element144  label="C_element : 089"  # scripted group (container) (typed FeaturePython)
  n = 10
  ref = C_element
FEATURE [App::DocumentObjectGroupPython] N_element064  label="N_element : 036"  # scripted group (container) (typed FeaturePython)
  n = 5
  ref = N_element
FEATURE [App::DocumentObjectGroupPython] O_element126  label="O_element : 079"  # scripted group (container) (typed FeaturePython)
  n = 7
  ref = O_element
FEATURE [App::DocumentObjectGroupPython] P_element015  label="P_element : 004"  # scripted group (container) (typed FeaturePython)
  n = 1
  ref = P_element
FEATURE [App::DocumentObjectGroupPython] G4_DNA_A  # scripted group (container) (typed FeaturePython)
  Dunit = g/cm3
  Dvalue = 1
  Group = -> [H_element134,C_element144,N_element064,O_element126,P_element015]
  conduct = 2
  density = 1
  expand = 3
  formula = G4_DNA_A
  name = G4_DNA_A
  specific = 4
FEATURE [App::DocumentObjectGroupPython] H_element135  label="H_element : 082"  # scripted group (container) (typed FeaturePython)
  n = 10
  ref = H_element
FEATURE [App::DocumentObjectGroupPython] C_element145  label="C_element : 090"  # scripted group (container) (typed FeaturePython)
  n = 10
  ref = C_element
FEATURE [App::DocumentObjectGroupPython] N_element065  label="N_element : 037"  # scripted group (container) (typed FeaturePython)
  n = 5
  ref = N_element
FEATURE [App::DocumentObjectGroupPython] O_element127  label="O_element : 8"  # scripted group (container) (typed FeaturePython)
  n = 8
  ref = O_element
FEATURE [App::DocumentObjectGroupPython] P_element016  label="P_element : 005"  # scripted group (container) (typed FeaturePython)
  n = 1
  ref = P_element
FEATURE [App::DocumentObjectGroupPython] G4_DNA_G  # scripted group (container) (typed FeaturePython)
  Dunit = g/cm3
  Dvalue = 1
  Group = -> [H_element135,C_element145,N_element065,O_element127,P_element016]
  conduct = 2
  density = 1
  expand = 3
  formula = G4_DNA_G
  name = G4_DNA_G
  specific = 4
FEATURE [App::DocumentObjectGroupPython] H_element136  label="H_element : 083"  # scripted group (container) (typed FeaturePython)
  n = 10
  ref = H_element
FEATURE [App::DocumentObjectGroupPython] C_element146  label="C_element : 091"  # scripted group (container) (typed FeaturePython)
  n = 9
  ref = C_element
FEATURE [App::DocumentObjectGroupPython] N_element066  label="N_element : 038"  # scripted group (container) (typed FeaturePython)
  n = 3
  ref = N_element
FEATURE [App::DocumentObjectGroupPython] O_element128  label="O_element : 080"  # scripted group (container) (typed FeaturePython)
  n = 8
  ref = O_element
FEATURE [App::DocumentObjectGroupPython] P_element017  label="P_element : 006"  # scripted group (container) (typed FeaturePython)
  n = 1
  ref = P_element
FEATURE [App::DocumentObjectGroupPython] G4_DNA_C  # scripted group (container) (typed FeaturePython)
  Dunit = g/cm3
  Dvalue = 1
  Group = -> [H_element136,C_element146,N_element066,O_element128,P_element017]
  conduct = 2
  density = 1
  expand = 3
  formula = G4_DNA_C
  name = G4_DNA_C
  specific = 4
FEATURE [App::DocumentObjectGroupPython] H_element137  label="H_element : 084"  # scripted group (container) (typed FeaturePython)
  n = 9
  ref = H_element
FEATURE [App::DocumentObjectGroupPython] C_element147  label="C_element : 092"  # scripted group (container) (typed FeaturePython)
  n = 9
  ref = C_element
FEATURE [App::DocumentObjectGroupPython] N_element067  label="N_element : 039"  # scripted group (container) (typed FeaturePython)
  n = 2
  ref = N_element
FEATURE [App::DocumentObjectGroupPython] O_element129  label="O_element : 9"  # scripted group (container) (typed FeaturePython)
  n = 9
  ref = O_element
FEATURE [App::DocumentObjectGroupPython] P_element018  label="P_element : 007"  # scripted group (container) (typed FeaturePython)
  n = 1
  ref = P_element
FEATURE [App::DocumentObjectGroupPython] G4_DNA_U  # scripted group (container) (typed FeaturePython)
  Dunit = g/cm3
  Dvalue = 1
  Group = -> [H_element137,C_element147,N_element067,O_element129,P_element018]
  conduct = 2
  density = 1
  expand = 3
  formula = G4_DNA_U
  name = G4_DNA_U
  specific = 4
FEATURE [App::DocumentObjectGroupPython] H_element138  label="H_element : 085"  # scripted group (container) (typed FeaturePython)
  n = 11
  ref = H_element
FEATURE [App::DocumentObjectGroupPython] C_element148  label="C_element : 093"  # scripted group (container) (typed FeaturePython)
  n = 10
  ref = C_element
FEATURE [App::DocumentObjectGroupPython] N_element068  label="N_element : 040"  # scripted group (container) (typed FeaturePython)
  n = 2
  ref = N_element
FEATURE [App::DocumentObjectGroupPython] O_element130  label="O_element : 081"  # scripted group (container) (typed FeaturePython)
  n = 9
  ref = O_element
FEATURE [App::DocumentObjectGroupPython] P_element019  label="P_element : 008"  # scripted group (container) (typed FeaturePython)
  n = 1
  ref = P_element
FEATURE [App::DocumentObjectGroupPython] G4_DNA_MU  # scripted group (container) (typed FeaturePython)
  Dunit = g/cm3
  Dvalue = 1
  Group = -> [H_element138,C_element148,N_element068,O_element130,P_element019]
  conduct = 2
  density = 1
  expand = 3
  formula = G4_DNA_MU
  name = G4_DNA_MU
  specific = 4
FEATURE [App::DocumentObjectGroupPython] BioChemical  # scripted group (container) (typed FeaturePython)
  Group = -> [G4_CYTOSINE,G4_THYMINE,G4_URACIL,G4_DNA_ADENINE,G4_DNA_GUANINE,G4_DNA_CYTOSINE,G4_DNA_THYMINE,G4_DNA_URACIL,G4_DNA_ADENOSINE,G4_DNA_GUANOSINE,G4_DNA_CYTIDINE,G4_DNA_URIDINE,G4_DNA_METHYLURIDINE,G4_DNA_MONOPHOSPHATE,G4_DNA_A,G4_DNA_G,G4_DNA_C,G4_DNA_U,G4_DNA_MU]
FEATURE [App::DocumentObjectGroupPython] G4Materials  # scripted group (container) (typed FeaturePython)
  Group = -> [NIST,Element,HEP,Space,BioChemical]
  version = 1
FEATURE [App::DocumentObjectGroupPython] Geant4  # scripted group (container) (typed FeaturePython)
  Group = -> [G4Isotopes,G4Elements,G4Materials]
FEATURE [App::DocumentObjectGroupPython] Materials  # scripted group (container) (typed FeaturePython)
  Group = -> [Geant4]
FEATURE [Part::FeaturePython] GDMLBox_WorldBox  # WARN: FeaturePython — macro-defined, semantics opaque (R4)
  lunit = 2
  material = 5
  x = 100
  y = 100
  z = 100
FEATURE [Part::FeaturePython] GDMLBox_Box  # WARN: FeaturePython — macro-defined, semantics opaque (R4)
  lunit = 2
  material = 0
  x = 10
  y = 10
  z = 10
FEATURE [App::Part] LV_Box
  Group = -> [GDMLBox_Box]
  Origin = -> Origin002
FEATURE [App::Part] worldVOL
  Group = -> [GDMLBox_WorldBox,LV_Box]
  Origin = -> Origin
FEATURE [Part::FeaturePython] Array  # Draft array (typed FeaturePython)
  AlwaysSyncPlacement = false
  Angle = 360
  ArrayType = 0
  Axis = (0,0,1)
  Base = -> LV_Box
  Center = (0,0,0)
  Count = 4
  ExpandArray = false
  Fuse = false
  IntervalAxis = (0,0,0)
  IntervalX = (100,0,0)
  IntervalY = (0,100,0)
  IntervalZ = (0,0,100)
  NumberCircles = 3
  NumberPolar = 5
  NumberX = 2
  NumberY = 2
  NumberZ = 1
  PlacementList = 4 placements: [(0,0,0),(0,100,0),(100,0,0),(100,100,0)]
  RadialDistance = 50
  ScaleList = (4) [(1,1,1),(1,1,1),(1,1,1),(1,1,1)]
  Symmetry = 1
  TangentialDistance = 25
